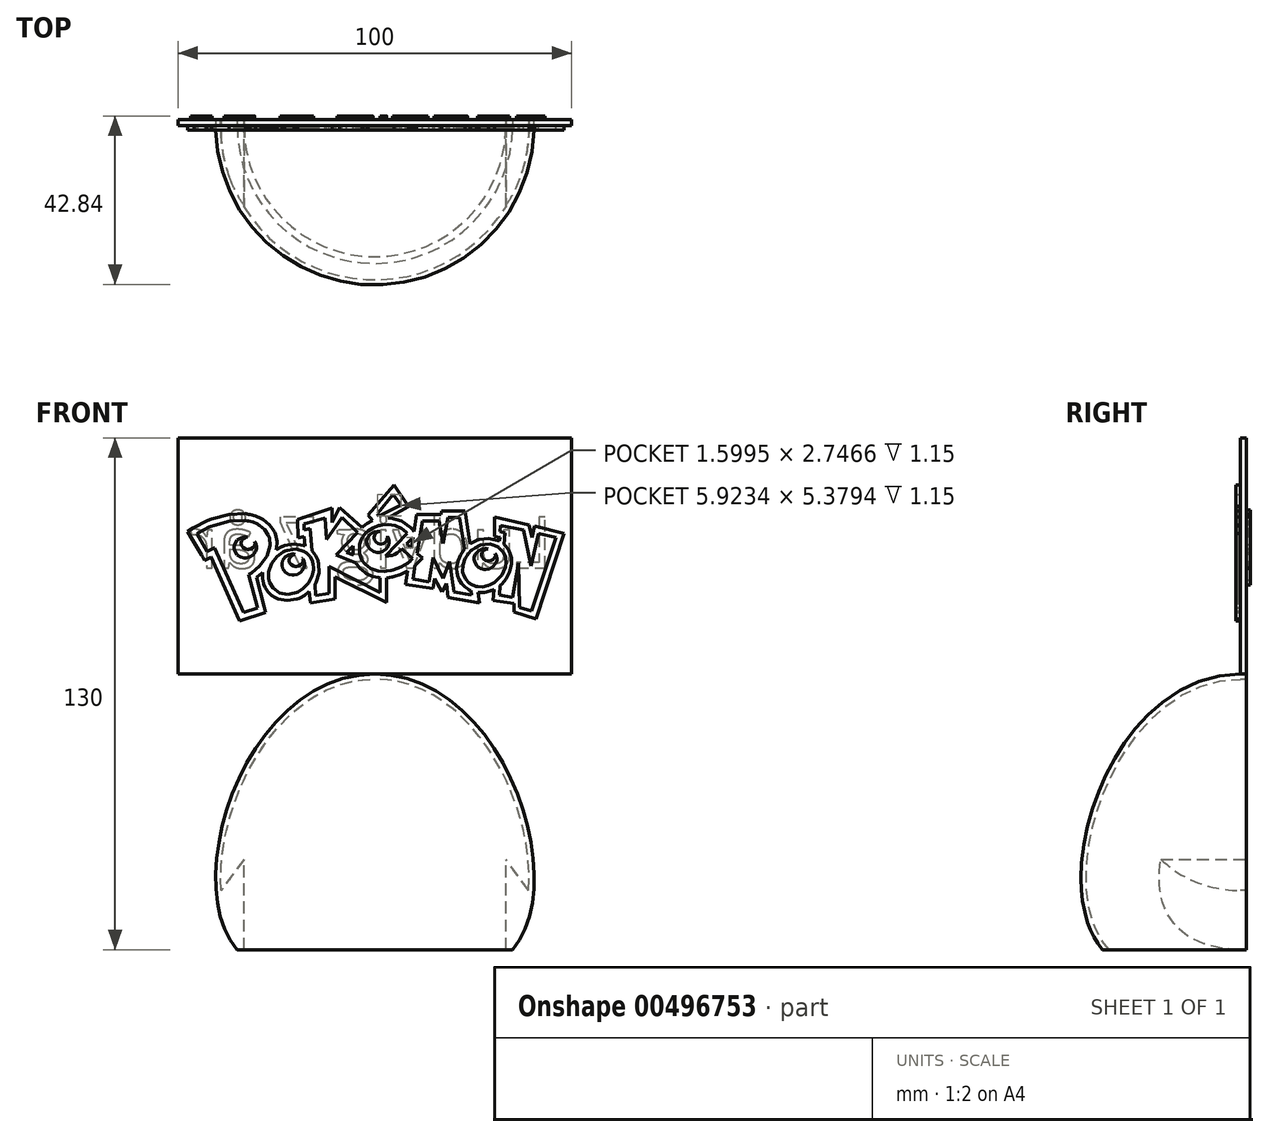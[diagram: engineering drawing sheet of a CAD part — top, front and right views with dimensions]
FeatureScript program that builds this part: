
annotation { "Feature Type Name" : "Feature", "Feature Type Description" : "" }
export const myFeature = defineFeature(function(context is Context, id is Id, definition is map)
    precondition{}
    {
        {
            var Q0;
            Q0=qCreatedBy(makeId("Front.planeOp"),FACE);
            var sketch = newSketch(context, id + "F0", { "sketchPlane" : qUnion([Q0])});
            skLineSegment(sketch, "E0.bottom", {"start": v(-50, 0) * mm, "end": v(50, 0) * mm});
            skLineSegment(sketch, "E0.top", {"start": v(-50, 130) * mm, "end": v(50, 130) * mm});
            skLineSegment(sketch, "E0.left", {"start": v(-50, 0) * mm, "end": v(-50, 130) * mm});
            skLineSegment(sketch, "E0.right", {"start": v(50, 0) * mm, "end": v(50, 130) * mm});
            skLineSegment(sketch, "E1.top", {"start": v(-50, 70) * mm, "end": v(50, 70) * mm});
            skLineSegment(sketch, "E1.left", {"start": v(-50, 0) * mm, "end": v(-50, 70) * mm});
            skLineSegment(sketch, "E1.right", {"start": v(50, 0) * mm, "end": v(50, 70) * mm});
            skPoint(sketch, "E2", {"position": v(35, 0) * mm});
            skFitSpline(sketch, "E3", {"points": [v(35, 0) * mm, v(0, 70) * mm], "startDerivative": vector(45, 52.54) * mm, "endDerivative": vector(-98.13, 0) * mm});
            skLineSegment(sketch, "E4", {"start": v(0, 70) * mm, "end": v(0, 0) * mm});
            skFitSpline(sketch, "E5.MirrorCS", {"points": [v(-35, 0) * mm, v(0, 70) * mm], "startDerivative": vector(-45, 52.54) * mm, "endDerivative": vector(98.13, 0) * mm});
            skSolve(sketch);
        }
        {
            var Q0;
            Q0=makeQuery(id+"F0.imprint","IMPRINT",FACE,{"disambiguationData":[TD([[makeQuery(id+"F0.imprint","IMPRINT",EDGE,{"derivedFrom":sQuery(id+"F0.wireOp",EDGE,"E0.top")}),-1.0]])]});
            var Q1;
            {var subQ0=sQuery(id+"F0.wireOp",EDGE,"E1.left");Q1=makeQuery(id+"F0.imprint","IMPRINT",FACE,{"disambiguationData":[TD([[makeQuery(id+"F0.imprint","IMPRINT",EDGE,{"derivedFrom":subQ0}),-1.0]])]});}
            var Q2;
            {var subQ0=sQuery(id+"F0.wireOp",EDGE,"E1.right");Q2=makeQuery(id+"F0.imprint","IMPRINT",FACE,{"disambiguationData":[TD([[makeQuery(id+"F0.imprint","IMPRINT",EDGE,{"derivedFrom":subQ0}),1.0]])]});}
            extrude(context, id + "F1", {"entities" : qUnion([Q0, Q1, Q2]), "oppositeDirection" : true, "depth" : 1.5 * mm});
        }
        {
            var Q0;
            Q0=makeQuery(id+"F1.opExtrude","CAP_FACE",FACE,{"disambiguationData":[OSD([sQuery(id+"F0.wireOp",EDGE,"E0.top"),sQuery(id+"F0.wireOp",EDGE,"E0.left"),sQuery(id+"F0.wireOp",EDGE,"E0.right"),sQuery(id+"F0.wireOp",EDGE,"E0.bottom"),sQuery(id+"F0.wireOp",EDGE,"E1.left"),sQuery(id+"F0.wireOp",EDGE,"E1.right")])],"isStart":true});
            var sketch = newSketch(context, id + "F2", { "sketchPlane" : qUnion([Q0])});
            skLineSegment(sketch, "E6", {"start": v(0.3, 95.2) * mm, "end": v(0.27, 95.07) * mm});
            skLineSegment(sketch, "E7", {"start": v(0.27, 95.07) * mm, "end": v(0.24, 95.2) * mm});
            skLineSegment(sketch, "E8", {"start": v(0.24, 95.2) * mm, "end": v(-0.14, 95.3) * mm});
            skLineSegment(sketch, "E9", {"start": v(-0.14, 95.3) * mm, "end": v(-0.14, 95.08) * mm});
            skLineSegment(sketch, "E10", {"start": v(-0.14, 95.08) * mm, "end": v(-0.08, 95.07) * mm});
            skLineSegment(sketch, "E11", {"start": v(-0.08, 95.07) * mm, "end": v(-0.08, 95.03) * mm});
            skLineSegment(sketch, "E12", {"start": v(-0.08, 95.03) * mm, "end": v(-0.08, 95.03) * mm});
            skLineSegment(sketch, "E13", {"start": v(-0.08, 95.03) * mm, "end": v(-0.09, 95.03) * mm});
            skLineSegment(sketch, "E14", {"start": v(-0.09, 95.03) * mm, "end": v(-0.09, 95.03) * mm});
            skLineSegment(sketch, "E15", {"start": v(-0.09, 95.03) * mm, "end": v(-0.1, 95.04) * mm});
            skLineSegment(sketch, "E16", {"start": v(-0.1, 95.04) * mm, "end": v(-0.2, 95.06) * mm});
            skLineSegment(sketch, "E17", {"start": v(-0.2, 95.06) * mm, "end": v(-0.3, 95.05) * mm});
            skLineSegment(sketch, "E18", {"start": v(-0.3, 95.05) * mm, "end": v(-0.33, 95.04) * mm});
            skLineSegment(sketch, "E19", {"start": v(-0.33, 95.04) * mm, "end": v(-0.34, 95.04) * mm});
            skLineSegment(sketch, "E20", {"start": v(-0.34, 95.04) * mm, "end": v(-0.4, 95) * mm});
            skLineSegment(sketch, "E21", {"start": v(-0.4, 95) * mm, "end": v(-0.4, 95) * mm});
            skLineSegment(sketch, "E22", {"start": v(-0.4, 95) * mm, "end": v(-0.47, 95.36) * mm});
            skLineSegment(sketch, "E23", {"start": v(-0.47, 95.36) * mm, "end": v(-0.72, 95.36) * mm});
            skLineSegment(sketch, "E24", {"start": v(-0.72, 95.36) * mm, "end": v(-0.73, 95.32) * mm});
            skLineSegment(sketch, "E25", {"start": v(-0.73, 95.32) * mm, "end": v(-1, 95.32) * mm});
            skLineSegment(sketch, "E26", {"start": v(-1, 95.32) * mm, "end": v(-1.03, 95.13) * mm});
            skLineSegment(sketch, "E27", {"start": v(-1.03, 95.13) * mm, "end": v(-1.05, 95.16) * mm});
            skLineSegment(sketch, "E28", {"start": v(-1.05, 95.16) * mm, "end": v(-1.07, 95.18) * mm});
            skLineSegment(sketch, "E29", {"start": v(-1.07, 95.18) * mm, "end": v(-1.17, 95.25) * mm});
            skLineSegment(sketch, "E30", {"start": v(-1.17, 95.25) * mm, "end": v(-1.3, 95.29) * mm});
            skLineSegment(sketch, "E31", {"start": v(-1.3, 95.29) * mm, "end": v(-1.32, 95.29) * mm});
            skLineSegment(sketch, "E32", {"start": v(-1.32, 95.29) * mm, "end": v(-1.09, 95.41) * mm});
            skLineSegment(sketch, "E33", {"start": v(-1.09, 95.41) * mm, "end": v(-1.25, 95.65) * mm});
            skLineSegment(sketch, "E34", {"start": v(-1.25, 95.65) * mm, "end": v(-1.53, 95.32) * mm});
            skLineSegment(sketch, "E35", {"start": v(-1.53, 95.32) * mm, "end": v(-1.49, 95.26) * mm});
            skLineSegment(sketch, "E36", {"start": v(-1.49, 95.26) * mm, "end": v(-1.5, 95.25) * mm});
            skLineSegment(sketch, "E37", {"start": v(-1.5, 95.25) * mm, "end": v(-1.55, 95.22) * mm});
            skLineSegment(sketch, "E38", {"start": v(-1.55, 95.22) * mm, "end": v(-1.6, 95.19) * mm});
            skLineSegment(sketch, "E39", {"start": v(-1.6, 95.19) * mm, "end": v(-1.6, 95.18) * mm});
            skLineSegment(sketch, "E40", {"start": v(-1.6, 95.18) * mm, "end": v(-1.85, 95.4) * mm});
            skLineSegment(sketch, "E41", {"start": v(-1.85, 95.4) * mm, "end": v(-1.94, 95.23) * mm});
            skLineSegment(sketch, "E42", {"start": v(-1.94, 95.23) * mm, "end": v(-1.93, 95.4) * mm});
            skLineSegment(sketch, "E43", {"start": v(-1.93, 95.4) * mm, "end": v(-2.32, 95.27) * mm});
            skLineSegment(sketch, "E44", {"start": v(-2.32, 95.27) * mm, "end": v(-2.3, 95.06) * mm});
            skLineSegment(sketch, "E45", {"start": v(-2.3, 95.06) * mm, "end": v(-2.24, 95.08) * mm});
            skLineSegment(sketch, "E46", {"start": v(-2.24, 95.08) * mm, "end": v(-2.23, 94.98) * mm});
            skLineSegment(sketch, "E47", {"start": v(-2.23, 94.98) * mm, "end": v(-2.25, 94.98) * mm});
            skLineSegment(sketch, "E48", {"start": v(-2.25, 94.98) * mm, "end": v(-2.35, 95) * mm});
            skLineSegment(sketch, "E49", {"start": v(-2.35, 95) * mm, "end": v(-2.46, 94.98) * mm});
            skLineSegment(sketch, "E50", {"start": v(-2.46, 94.98) * mm, "end": v(-2.48, 94.97) * mm});
            skLineSegment(sketch, "E51", {"start": v(-2.48, 94.97) * mm, "end": v(-2.49, 94.97) * mm});
            skLineSegment(sketch, "E52", {"start": v(-2.49, 94.97) * mm, "end": v(-2.55, 94.94) * mm});
            skLineSegment(sketch, "E53", {"start": v(-2.55, 94.94) * mm, "end": v(-2.55, 94.93) * mm});
            skLineSegment(sketch, "E54", {"start": v(-2.55, 94.93) * mm, "end": v(-2.55, 94.95) * mm});
            skLineSegment(sketch, "E55", {"start": v(-2.55, 94.95) * mm, "end": v(-2.54, 95.03) * mm});
            skLineSegment(sketch, "E56", {"start": v(-2.54, 95.03) * mm, "end": v(-2.56, 95.1) * mm});
            skLineSegment(sketch, "E57", {"start": v(-2.56, 95.1) * mm, "end": v(-2.56, 95.12) * mm});
            skLineSegment(sketch, "E58", {"start": v(-2.56, 95.12) * mm, "end": v(-2.57, 95.13) * mm});
            skLineSegment(sketch, "E59", {"start": v(-2.57, 95.13) * mm, "end": v(-2.59, 95.16) * mm});
            skLineSegment(sketch, "E60", {"start": v(-2.59, 95.16) * mm, "end": v(-2.62, 95.2) * mm});
            skLineSegment(sketch, "E61", {"start": v(-2.62, 95.2) * mm, "end": v(-2.66, 95.24) * mm});
            skLineSegment(sketch, "E62", {"start": v(-2.66, 95.24) * mm, "end": v(-2.7, 95.27) * mm});
            skLineSegment(sketch, "E63", {"start": v(-2.7, 95.27) * mm, "end": v(-2.7, 95.27) * mm});
            skLineSegment(sketch, "E64", {"start": v(-2.7, 95.27) * mm, "end": v(-2.72, 95.28) * mm});
            skLineSegment(sketch, "E65", {"start": v(-2.72, 95.28) * mm, "end": v(-2.78, 95.3) * mm});
            skLineSegment(sketch, "E66", {"start": v(-2.78, 95.3) * mm, "end": v(-2.84, 95.32) * mm});
            skLineSegment(sketch, "E67", {"start": v(-2.84, 95.32) * mm, "end": v(-2.86, 95.33) * mm});
            skLineSegment(sketch, "E68", {"start": v(-2.86, 95.33) * mm, "end": v(-2.89, 95.33) * mm});
            skLineSegment(sketch, "E69", {"start": v(-2.89, 95.33) * mm, "end": v(-3.07, 95.33) * mm});
            skLineSegment(sketch, "E70", {"start": v(-3.07, 95.33) * mm, "end": v(-3.27, 95.27) * mm});
            skLineSegment(sketch, "E71", {"start": v(-3.27, 95.27) * mm, "end": v(-3.3, 95.26) * mm});
            skLineSegment(sketch, "E72", {"start": v(-3.3, 95.26) * mm, "end": v(-3.32, 95.25) * mm});
            skLineSegment(sketch, "E73", {"start": v(-3.32, 95.25) * mm, "end": v(-3.46, 95.18) * mm});
            skLineSegment(sketch, "E74", {"start": v(-3.46, 95.18) * mm, "end": v(-3.47, 95.17) * mm});
            skLineSegment(sketch, "E75", {"start": v(-3.47, 95.17) * mm, "end": v(-3.53, 95.13) * mm});
            skLineSegment(sketch, "E76", {"start": v(-3.53, 95.13) * mm, "end": v(-3.5, 95.07) * mm});
            skLineSegment(sketch, "E77", {"start": v(-3.5, 95.07) * mm, "end": v(-3.38, 94.88) * mm});
            skLineSegment(sketch, "E78", {"start": v(-3.38, 94.88) * mm, "end": v(-3.37, 94.87) * mm});
            skLineSegment(sketch, "E79", {"start": v(-3.37, 94.87) * mm, "end": v(-3.36, 94.85) * mm});
            skLineSegment(sketch, "E80", {"start": v(-3.36, 94.85) * mm, "end": v(-3.35, 94.83) * mm});
            skLineSegment(sketch, "E81", {"start": v(-3.35, 94.83) * mm, "end": v(-3.34, 94.82) * mm});
            skLineSegment(sketch, "E82", {"start": v(-3.34, 94.82) * mm, "end": v(-3.34, 94.82) * mm});
            skLineSegment(sketch, "E83", {"start": v(-3.34, 94.82) * mm, "end": v(-3.28, 94.85) * mm});
            skLineSegment(sketch, "E84", {"start": v(-3.28, 94.85) * mm, "end": v(-3.27, 94.85) * mm});
            skLineSegment(sketch, "E85", {"start": v(-3.27, 94.85) * mm, "end": v(-2.98, 94.21) * mm});
            skLineSegment(sketch, "E86", {"start": v(-2.98, 94.21) * mm, "end": v(-2.96, 94.15) * mm});
            skLineSegment(sketch, "E87", {"start": v(-2.96, 94.15) * mm, "end": v(-2.9, 94.17) * mm});
            skLineSegment(sketch, "E88", {"start": v(-2.9, 94.17) * mm, "end": v(-2.74, 94.22) * mm});
            skLineSegment(sketch, "E89", {"start": v(-2.74, 94.22) * mm, "end": v(-2.67, 94.24) * mm});
            skLineSegment(sketch, "E90", {"start": v(-2.67, 94.24) * mm, "end": v(-2.69, 94.31) * mm});
            skLineSegment(sketch, "E91", {"start": v(-2.69, 94.31) * mm, "end": v(-2.77, 94.63) * mm});
            skLineSegment(sketch, "E92", {"start": v(-2.77, 94.63) * mm, "end": v(-2.76, 94.63) * mm});
            skLineSegment(sketch, "E93", {"start": v(-2.76, 94.63) * mm, "end": v(-2.7, 94.68) * mm});
            skLineSegment(sketch, "E94", {"start": v(-2.7, 94.68) * mm, "end": v(-2.7, 94.68) * mm});
            skLineSegment(sketch, "E95", {"start": v(-2.7, 94.68) * mm, "end": v(-2.7, 94.67) * mm});
            skLineSegment(sketch, "E96", {"start": v(-2.7, 94.67) * mm, "end": v(-2.7, 94.63) * mm});
            skLineSegment(sketch, "E97", {"start": v(-2.7, 94.63) * mm, "end": v(-2.7, 94.58) * mm});
            skLineSegment(sketch, "E98", {"start": v(-2.7, 94.58) * mm, "end": v(-2.7, 94.57) * mm});
            skLineSegment(sketch, "E99", {"start": v(-2.7, 94.57) * mm, "end": v(-2.69, 94.56) * mm});
            skLineSegment(sketch, "E100", {"start": v(-2.69, 94.56) * mm, "end": v(-2.67, 94.52) * mm});
            skLineSegment(sketch, "E101", {"start": v(-2.67, 94.52) * mm, "end": v(-2.64, 94.47) * mm});
            skLineSegment(sketch, "E102", {"start": v(-2.64, 94.47) * mm, "end": v(-2.6, 94.43) * mm});
            skLineSegment(sketch, "E103", {"start": v(-2.6, 94.43) * mm, "end": v(-2.56, 94.4) * mm});
            skLineSegment(sketch, "E104", {"start": v(-2.56, 94.4) * mm, "end": v(-2.55, 94.4) * mm});
            skLineSegment(sketch, "E105", {"start": v(-2.55, 94.4) * mm, "end": v(-2.53, 94.39) * mm});
            skLineSegment(sketch, "E106", {"start": v(-2.53, 94.39) * mm, "end": v(-2.43, 94.37) * mm});
            skLineSegment(sketch, "E107", {"start": v(-2.43, 94.37) * mm, "end": v(-2.32, 94.39) * mm});
            skLineSegment(sketch, "E108", {"start": v(-2.32, 94.39) * mm, "end": v(-2.3, 94.4) * mm});
            skLineSegment(sketch, "E109", {"start": v(-2.3, 94.4) * mm, "end": v(-2.29, 94.4) * mm});
            skLineSegment(sketch, "E110", {"start": v(-2.29, 94.4) * mm, "end": v(-2.24, 94.43) * mm});
            skLineSegment(sketch, "E111", {"start": v(-2.24, 94.43) * mm, "end": v(-2.2, 94.47) * mm});
            skLineSegment(sketch, "E112", {"start": v(-2.2, 94.47) * mm, "end": v(-2.19, 94.47) * mm});
            skLineSegment(sketch, "E113", {"start": v(-2.19, 94.47) * mm, "end": v(-2.17, 94.35) * mm});
            skLineSegment(sketch, "E114", {"start": v(-2.17, 94.35) * mm, "end": v(-1.9, 94.39) * mm});
            skLineSegment(sketch, "E115", {"start": v(-1.9, 94.39) * mm, "end": v(-1.9, 94.63) * mm});
            skLineSegment(sketch, "E116", {"start": v(-1.9, 94.63) * mm, "end": v(-1.33, 94.35) * mm});
            skLineSegment(sketch, "E117", {"start": v(-1.33, 94.35) * mm, "end": v(-1.33, 94.62) * mm});
            skLineSegment(sketch, "E118", {"start": v(-1.33, 94.62) * mm, "end": v(-1.33, 94.62) * mm});
            skLineSegment(sketch, "E119", {"start": v(-1.33, 94.62) * mm, "end": v(-1.27, 94.63) * mm});
            skLineSegment(sketch, "E120", {"start": v(-1.27, 94.63) * mm, "end": v(-1.26, 94.63) * mm});
            skLineSegment(sketch, "E121", {"start": v(-1.26, 94.63) * mm, "end": v(-1.25, 94.64) * mm});
            skLineSegment(sketch, "E122", {"start": v(-1.25, 94.64) * mm, "end": v(-1.18, 94.66) * mm});
            skLineSegment(sketch, "E123", {"start": v(-1.18, 94.66) * mm, "end": v(-1.11, 94.7) * mm});
            skLineSegment(sketch, "E124", {"start": v(-1.11, 94.7) * mm, "end": v(-1.1, 94.7) * mm});
            skLineSegment(sketch, "E125", {"start": v(-1.1, 94.7) * mm, "end": v(-1.12, 94.55) * mm});
            skLineSegment(sketch, "E126", {"start": v(-1.12, 94.55) * mm, "end": v(-0.82, 94.5) * mm});
            skLineSegment(sketch, "E127", {"start": v(-0.82, 94.5) * mm, "end": v(-0.8, 94.62) * mm});
            skLineSegment(sketch, "E128", {"start": v(-0.8, 94.62) * mm, "end": v(-0.72, 94.47) * mm});
            skLineSegment(sketch, "E129", {"start": v(-0.72, 94.47) * mm, "end": v(-0.67, 94.56) * mm});
            skLineSegment(sketch, "E130", {"start": v(-0.67, 94.56) * mm, "end": v(-0.65, 94.4) * mm});
            skLineSegment(sketch, "E131", {"start": v(-0.65, 94.4) * mm, "end": v(-0.3, 94.35) * mm});
            skLineSegment(sketch, "E132", {"start": v(-0.3, 94.35) * mm, "end": v(-0.32, 94.46) * mm});
            skLineSegment(sketch, "E133", {"start": v(-0.32, 94.46) * mm, "end": v(-0.31, 94.46) * mm});
            skLineSegment(sketch, "E134", {"start": v(-0.31, 94.46) * mm, "end": v(-0.25, 94.46) * mm});
            skLineSegment(sketch, "E135", {"start": v(-0.25, 94.46) * mm, "end": v(-0.2, 94.48) * mm});
            skLineSegment(sketch, "E136", {"start": v(-0.2, 94.48) * mm, "end": v(-0.18, 94.48) * mm});
            skLineSegment(sketch, "E137", {"start": v(-0.18, 94.48) * mm, "end": v(-0.18, 94.48) * mm});
            skLineSegment(sketch, "E138", {"start": v(-0.18, 94.48) * mm, "end": v(-0.15, 94.5) * mm});
            skLineSegment(sketch, "E139", {"start": v(-0.15, 94.5) * mm, "end": v(-0.14, 94.5) * mm});
            skLineSegment(sketch, "E140", {"start": v(-0.14, 94.5) * mm, "end": v(-0.16, 94.37) * mm});
            skLineSegment(sketch, "E141", {"start": v(-0.16, 94.37) * mm, "end": v(0.07, 94.34) * mm});
            skLineSegment(sketch, "E142", {"start": v(0.07, 94.34) * mm, "end": v(0.07, 94.24) * mm});
            skLineSegment(sketch, "E143", {"start": v(0.07, 94.24) * mm, "end": v(0.32, 94.17) * mm});
            skLineSegment(sketch, "E144", {"start": v(0.32, 94.17) * mm, "end": v(0.63, 95.12) * mm});
            skLineSegment(sketch, "E145", {"start": v(0.63, 95.12) * mm, "end": v(0.3, 95.2) * mm});
            skLineSegment(sketch, "E146", {"start": v(-1.06, 95.05) * mm, "end": v(-1.04, 95.07) * mm});
            skLineSegment(sketch, "E147", {"start": v(-1.04, 95.07) * mm, "end": v(-1.06, 94.95) * mm});
            skLineSegment(sketch, "E148", {"start": v(-1.06, 94.95) * mm, "end": v(-1.1, 95) * mm});
            skLineSegment(sketch, "E149", {"start": v(-1.1, 95) * mm, "end": v(-1.06, 95.05) * mm});
            skLineSegment(sketch, "E150", {"start": v(-1.26, 95.54) * mm, "end": v(-1.18, 95.43) * mm});
            skLineSegment(sketch, "E151", {"start": v(-1.18, 95.43) * mm, "end": v(-1.42, 95.3) * mm});
            skLineSegment(sketch, "E152", {"start": v(-1.42, 95.3) * mm, "end": v(-1.43, 95.33) * mm});
            skLineSegment(sketch, "E153", {"start": v(-1.43, 95.33) * mm, "end": v(-1.26, 95.54) * mm});
            skLineSegment(sketch, "E154", {"start": v(-2.85, 94.66) * mm, "end": v(-2.76, 94.3) * mm});
            skLineSegment(sketch, "E155", {"start": v(-2.76, 94.3) * mm, "end": v(-2.91, 94.24) * mm});
            skLineSegment(sketch, "E156", {"start": v(-2.91, 94.24) * mm, "end": v(-3.23, 94.95) * mm});
            skLineSegment(sketch, "E157", {"start": v(-3.23, 94.95) * mm, "end": v(-3.24, 94.95) * mm});
            skLineSegment(sketch, "E158", {"start": v(-3.24, 94.95) * mm, "end": v(-3.27, 94.94) * mm});
            skLineSegment(sketch, "E159", {"start": v(-3.27, 94.94) * mm, "end": v(-3.3, 94.92) * mm});
            skLineSegment(sketch, "E160", {"start": v(-3.3, 94.92) * mm, "end": v(-3.31, 94.92) * mm});
            skLineSegment(sketch, "E161", {"start": v(-3.31, 94.92) * mm, "end": v(-3.43, 95.11) * mm});
            skLineSegment(sketch, "E162", {"start": v(-3.43, 95.11) * mm, "end": v(-3.42, 95.12) * mm});
            skLineSegment(sketch, "E163", {"start": v(-3.42, 95.12) * mm, "end": v(-3.3, 95.18) * mm});
            skLineSegment(sketch, "E164", {"start": v(-3.3, 95.18) * mm, "end": v(-3.28, 95.19) * mm});
            skLineSegment(sketch, "E165", {"start": v(-3.28, 95.19) * mm, "end": v(-3.24, 95.2) * mm});
            skLineSegment(sketch, "E166", {"start": v(-3.24, 95.2) * mm, "end": v(-3.06, 95.25) * mm});
            skLineSegment(sketch, "E167", {"start": v(-3.06, 95.25) * mm, "end": v(-2.9, 95.26) * mm});
            skLineSegment(sketch, "E168", {"start": v(-2.9, 95.26) * mm, "end": v(-2.87, 95.25) * mm});
            skLineSegment(sketch, "E169", {"start": v(-2.87, 95.25) * mm, "end": v(-2.86, 95.25) * mm});
            skLineSegment(sketch, "E170", {"start": v(-2.86, 95.25) * mm, "end": v(-2.8, 95.24) * mm});
            skLineSegment(sketch, "E171", {"start": v(-2.8, 95.24) * mm, "end": v(-2.76, 95.22) * mm});
            skLineSegment(sketch, "E172", {"start": v(-2.76, 95.22) * mm, "end": v(-2.75, 95.2) * mm});
            skLineSegment(sketch, "E173", {"start": v(-2.75, 95.2) * mm, "end": v(-2.73, 95.2) * mm});
            skLineSegment(sketch, "E174", {"start": v(-2.73, 95.2) * mm, "end": v(-2.68, 95.16) * mm});
            skLineSegment(sketch, "E175", {"start": v(-2.68, 95.16) * mm, "end": v(-2.64, 95.1) * mm});
            skLineSegment(sketch, "E176", {"start": v(-2.64, 95.1) * mm, "end": v(-2.63, 95.09) * mm});
            skLineSegment(sketch, "E177", {"start": v(-2.63, 95.09) * mm, "end": v(-2.62, 95.06) * mm});
            skLineSegment(sketch, "E178", {"start": v(-2.62, 95.06) * mm, "end": v(-2.62, 94.98) * mm});
            skLineSegment(sketch, "E179", {"start": v(-2.62, 94.98) * mm, "end": v(-2.65, 94.87) * mm});
            skLineSegment(sketch, "E180", {"start": v(-2.65, 94.87) * mm, "end": v(-2.73, 94.76) * mm});
            skLineSegment(sketch, "E181", {"start": v(-2.73, 94.76) * mm, "end": v(-2.82, 94.68) * mm});
            skLineSegment(sketch, "E182", {"start": v(-2.82, 94.68) * mm, "end": v(-2.85, 94.66) * mm});
            skLineSegment(sketch, "E183", {"start": v(-2.14, 94.73) * mm, "end": v(-2.14, 94.71) * mm});
            skLineSegment(sketch, "E184", {"start": v(-2.14, 94.71) * mm, "end": v(-2.16, 94.64) * mm});
            skLineSegment(sketch, "E185", {"start": v(-2.16, 94.64) * mm, "end": v(-2.19, 94.58) * mm});
            skLineSegment(sketch, "E186", {"start": v(-2.19, 94.58) * mm, "end": v(-2.2, 94.57) * mm});
            skLineSegment(sketch, "E187", {"start": v(-2.2, 94.57) * mm, "end": v(-2.2, 94.56) * mm});
            skLineSegment(sketch, "E188", {"start": v(-2.2, 94.56) * mm, "end": v(-2.25, 94.5) * mm});
            skLineSegment(sketch, "E189", {"start": v(-2.25, 94.5) * mm, "end": v(-2.31, 94.47) * mm});
            skLineSegment(sketch, "E190", {"start": v(-2.31, 94.47) * mm, "end": v(-2.32, 94.46) * mm});
            skLineSegment(sketch, "E191", {"start": v(-2.32, 94.46) * mm, "end": v(-2.35, 94.45) * mm});
            skLineSegment(sketch, "E192", {"start": v(-2.35, 94.45) * mm, "end": v(-2.42, 94.44) * mm});
            skLineSegment(sketch, "E193", {"start": v(-2.42, 94.44) * mm, "end": v(-2.51, 94.46) * mm});
            skLineSegment(sketch, "E194", {"start": v(-2.51, 94.46) * mm, "end": v(-2.59, 94.51) * mm});
            skLineSegment(sketch, "E195", {"start": v(-2.59, 94.51) * mm, "end": v(-2.62, 94.57) * mm});
            skLineSegment(sketch, "E196", {"start": v(-2.62, 94.57) * mm, "end": v(-2.63, 94.6) * mm});
            skLineSegment(sketch, "E197", {"start": v(-2.63, 94.6) * mm, "end": v(-2.64, 94.61) * mm});
            skLineSegment(sketch, "E198", {"start": v(-2.64, 94.61) * mm, "end": v(-2.64, 94.69) * mm});
            skLineSegment(sketch, "E199", {"start": v(-2.64, 94.69) * mm, "end": v(-2.6, 94.78) * mm});
            skLineSegment(sketch, "E200", {"start": v(-2.6, 94.78) * mm, "end": v(-2.54, 94.86) * mm});
            skLineSegment(sketch, "E201", {"start": v(-2.54, 94.86) * mm, "end": v(-2.48, 94.9) * mm});
            skLineSegment(sketch, "E202", {"start": v(-2.48, 94.9) * mm, "end": v(-2.45, 94.92) * mm});
            skLineSegment(sketch, "E203", {"start": v(-2.45, 94.92) * mm, "end": v(-2.43, 94.93) * mm});
            skLineSegment(sketch, "E204", {"start": v(-2.43, 94.93) * mm, "end": v(-2.33, 94.94) * mm});
            skLineSegment(sketch, "E205", {"start": v(-2.33, 94.94) * mm, "end": v(-2.24, 94.92) * mm});
            skLineSegment(sketch, "E206", {"start": v(-2.24, 94.92) * mm, "end": v(-2.23, 94.9) * mm});
            skLineSegment(sketch, "E207", {"start": v(-2.23, 94.9) * mm, "end": v(-2.22, 94.9) * mm});
            skLineSegment(sketch, "E208", {"start": v(-2.22, 94.9) * mm, "end": v(-2.18, 94.86) * mm});
            skLineSegment(sketch, "E209", {"start": v(-2.18, 94.86) * mm, "end": v(-2.15, 94.8) * mm});
            skLineSegment(sketch, "E210", {"start": v(-2.15, 94.8) * mm, "end": v(-2.15, 94.8) * mm});
            skLineSegment(sketch, "E211", {"start": v(-2.15, 94.8) * mm, "end": v(-2.14, 94.78) * mm});
            skLineSegment(sketch, "E212", {"start": v(-2.14, 94.78) * mm, "end": v(-2.14, 94.78) * mm});
            skLineSegment(sketch, "E213", {"start": v(-2.14, 94.78) * mm, "end": v(-2.14, 94.73) * mm});
            skLineSegment(sketch, "E214", {"start": v(-2.14, 94.73) * mm, "end": v(-2.14, 94.73) * mm});
            skLineSegment(sketch, "E215", {"start": v(-1.4, 94.46) * mm, "end": v(-1.97, 94.75) * mm});
            skLineSegment(sketch, "E216", {"start": v(-1.97, 94.75) * mm, "end": v(-1.97, 94.45) * mm});
            skLineSegment(sketch, "E217", {"start": v(-1.97, 94.45) * mm, "end": v(-2.11, 94.43) * mm});
            skLineSegment(sketch, "E218", {"start": v(-2.11, 94.43) * mm, "end": v(-2.12, 94.55) * mm});
            skLineSegment(sketch, "E219", {"start": v(-2.12, 94.55) * mm, "end": v(-2.11, 94.57) * mm});
            skLineSegment(sketch, "E220", {"start": v(-2.11, 94.57) * mm, "end": v(-2.08, 94.68) * mm});
            skLineSegment(sketch, "E221", {"start": v(-2.08, 94.68) * mm, "end": v(-2.08, 94.78) * mm});
            skLineSegment(sketch, "E222", {"start": v(-2.08, 94.78) * mm, "end": v(-2.09, 94.8) * mm});
            skLineSegment(sketch, "E223", {"start": v(-2.09, 94.8) * mm, "end": v(-2.09, 94.82) * mm});
            skLineSegment(sketch, "E224", {"start": v(-2.09, 94.82) * mm, "end": v(-2.11, 94.87) * mm});
            skLineSegment(sketch, "E225", {"start": v(-2.11, 94.87) * mm, "end": v(-2.15, 94.91) * mm});
            skLineSegment(sketch, "E226", {"start": v(-2.15, 94.91) * mm, "end": v(-2.16, 94.92) * mm});
            skLineSegment(sketch, "E227", {"start": v(-2.16, 94.92) * mm, "end": v(-2.18, 95.17) * mm});
            skLineSegment(sketch, "E228", {"start": v(-2.18, 95.17) * mm, "end": v(-2.24, 95.15) * mm});
            skLineSegment(sketch, "E229", {"start": v(-2.24, 95.15) * mm, "end": v(-2.25, 95.22) * mm});
            skLineSegment(sketch, "E230", {"start": v(-2.25, 95.22) * mm, "end": v(-2.01, 95.29) * mm});
            skLineSegment(sketch, "E231", {"start": v(-2.01, 95.29) * mm, "end": v(-2, 95.05) * mm});
            skLineSegment(sketch, "E232", {"start": v(-2, 95.05) * mm, "end": v(-1.82, 95.29) * mm});
            skLineSegment(sketch, "E233", {"start": v(-1.82, 95.29) * mm, "end": v(-1.65, 95.13) * mm});
            skLineSegment(sketch, "E234", {"start": v(-1.65, 95.13) * mm, "end": v(-1.9, 94.88) * mm});
            skLineSegment(sketch, "E235", {"start": v(-1.9, 94.88) * mm, "end": v(-1.67, 94.8) * mm});
            skLineSegment(sketch, "E236", {"start": v(-1.67, 94.8) * mm, "end": v(-1.66, 94.78) * mm});
            skLineSegment(sketch, "E237", {"start": v(-1.66, 94.78) * mm, "end": v(-1.62, 94.73) * mm});
            skLineSegment(sketch, "E238", {"start": v(-1.62, 94.73) * mm, "end": v(-1.57, 94.68) * mm});
            skLineSegment(sketch, "E239", {"start": v(-1.57, 94.68) * mm, "end": v(-1.56, 94.67) * mm});
            skLineSegment(sketch, "E240", {"start": v(-1.56, 94.67) * mm, "end": v(-1.55, 94.67) * mm});
            skLineSegment(sketch, "E241", {"start": v(-1.55, 94.67) * mm, "end": v(-1.49, 94.64) * mm});
            skLineSegment(sketch, "E242", {"start": v(-1.49, 94.64) * mm, "end": v(-1.42, 94.63) * mm});
            skLineSegment(sketch, "E243", {"start": v(-1.42, 94.63) * mm, "end": v(-1.4, 94.62) * mm});
            skLineSegment(sketch, "E244", {"start": v(-1.4, 94.62) * mm, "end": v(-1.4, 94.46) * mm});
            skLineSegment(sketch, "E245", {"start": v(-1.7, 94.87) * mm, "end": v(-1.78, 94.9) * mm});
            skLineSegment(sketch, "E246", {"start": v(-1.78, 94.9) * mm, "end": v(-1.7, 94.98) * mm});
            skLineSegment(sketch, "E247", {"start": v(-1.7, 94.98) * mm, "end": v(-1.7, 94.97) * mm});
            skLineSegment(sketch, "E248", {"start": v(-1.7, 94.97) * mm, "end": v(-1.7, 94.88) * mm});
            skLineSegment(sketch, "E249", {"start": v(-1.7, 94.88) * mm, "end": v(-1.7, 94.87) * mm});
            skLineSegment(sketch, "E250", {"start": v(-1.08, 94.8) * mm, "end": v(-1.1, 94.79) * mm});
            skLineSegment(sketch, "E251", {"start": v(-1.1, 94.79) * mm, "end": v(-1.17, 94.74) * mm});
            skLineSegment(sketch, "E252", {"start": v(-1.17, 94.74) * mm, "end": v(-1.26, 94.71) * mm});
            skLineSegment(sketch, "E253", {"start": v(-1.26, 94.71) * mm, "end": v(-1.28, 94.7) * mm});
            skLineSegment(sketch, "E254", {"start": v(-1.28, 94.7) * mm, "end": v(-1.29, 94.7) * mm});
            skLineSegment(sketch, "E255", {"start": v(-1.29, 94.7) * mm, "end": v(-1.33, 94.7) * mm});
            skLineSegment(sketch, "E256", {"start": v(-1.33, 94.7) * mm, "end": v(-1.33, 94.7) * mm});
            skLineSegment(sketch, "E257", {"start": v(-1.33, 94.7) * mm, "end": v(-1.36, 94.7) * mm});
            skLineSegment(sketch, "E258", {"start": v(-1.36, 94.7) * mm, "end": v(-1.43, 94.7) * mm});
            skLineSegment(sketch, "E259", {"start": v(-1.43, 94.7) * mm, "end": v(-1.5, 94.73) * mm});
            skLineSegment(sketch, "E260", {"start": v(-1.5, 94.73) * mm, "end": v(-1.57, 94.78) * mm});
            skLineSegment(sketch, "E261", {"start": v(-1.57, 94.78) * mm, "end": v(-1.6, 94.82) * mm});
            skLineSegment(sketch, "E262", {"start": v(-1.6, 94.82) * mm, "end": v(-1.61, 94.84) * mm});
            skLineSegment(sketch, "E263", {"start": v(-1.61, 94.84) * mm, "end": v(-1.61, 94.84) * mm});
            skLineSegment(sketch, "E264", {"start": v(-1.61, 94.84) * mm, "end": v(-1.62, 94.87) * mm});
            skLineSegment(sketch, "E265", {"start": v(-1.62, 94.87) * mm, "end": v(-1.63, 94.88) * mm});
            skLineSegment(sketch, "E266", {"start": v(-1.63, 94.88) * mm, "end": v(-1.63, 94.9) * mm});
            skLineSegment(sketch, "E267", {"start": v(-1.63, 94.9) * mm, "end": v(-1.63, 94.94) * mm});
            skLineSegment(sketch, "E268", {"start": v(-1.63, 94.94) * mm, "end": v(-1.63, 95) * mm});
            skLineSegment(sketch, "E269", {"start": v(-1.63, 95) * mm, "end": v(-1.61, 95.04) * mm});
            skLineSegment(sketch, "E270", {"start": v(-1.61, 95.04) * mm, "end": v(-1.6, 95.08) * mm});
            skLineSegment(sketch, "E271", {"start": v(-1.6, 95.08) * mm, "end": v(-1.59, 95.09) * mm});
            skLineSegment(sketch, "E272", {"start": v(-1.59, 95.09) * mm, "end": v(-1.58, 95.1) * mm});
            skLineSegment(sketch, "E273", {"start": v(-1.58, 95.1) * mm, "end": v(-1.55, 95.13) * mm});
            skLineSegment(sketch, "E274", {"start": v(-1.55, 95.13) * mm, "end": v(-1.55, 95.13) * mm});
            skLineSegment(sketch, "E275", {"start": v(-1.55, 95.13) * mm, "end": v(-1.54, 95.14) * mm});
            skLineSegment(sketch, "E276", {"start": v(-1.54, 95.14) * mm, "end": v(-1.48, 95.18) * mm});
            skLineSegment(sketch, "E277", {"start": v(-1.48, 95.18) * mm, "end": v(-1.42, 95.2) * mm});
            skLineSegment(sketch, "E278", {"start": v(-1.42, 95.2) * mm, "end": v(-1.4, 95.2) * mm});
            skLineSegment(sketch, "E279", {"start": v(-1.4, 95.2) * mm, "end": v(-1.38, 95.2) * mm});
            skLineSegment(sketch, "E280", {"start": v(-1.38, 95.2) * mm, "end": v(-1.32, 95.21) * mm});
            skLineSegment(sketch, "E281", {"start": v(-1.32, 95.21) * mm, "end": v(-1.24, 95.2) * mm});
            skLineSegment(sketch, "E282", {"start": v(-1.24, 95.2) * mm, "end": v(-1.17, 95.17) * mm});
            skLineSegment(sketch, "E283", {"start": v(-1.17, 95.17) * mm, "end": v(-1.12, 95.13) * mm});
            skLineSegment(sketch, "E284", {"start": v(-1.12, 95.13) * mm, "end": v(-1.1, 95.11) * mm});
            skLineSegment(sketch, "E285", {"start": v(-1.1, 95.11) * mm, "end": v(-1.34, 94.86) * mm});
            skLineSegment(sketch, "E286", {"start": v(-1.34, 94.86) * mm, "end": v(-1.34, 94.86) * mm});
            skLineSegment(sketch, "E287", {"start": v(-1.34, 94.86) * mm, "end": v(-1.31, 94.86) * mm});
            skLineSegment(sketch, "E288", {"start": v(-1.31, 94.86) * mm, "end": v(-1.29, 94.87) * mm});
            skLineSegment(sketch, "E289", {"start": v(-1.29, 94.87) * mm, "end": v(-1.28, 94.87) * mm});
            skLineSegment(sketch, "E290", {"start": v(-1.28, 94.87) * mm, "end": v(-1.27, 94.87) * mm});
            skLineSegment(sketch, "E291", {"start": v(-1.27, 94.87) * mm, "end": v(-1.25, 94.88) * mm});
            skLineSegment(sketch, "E292", {"start": v(-1.25, 94.88) * mm, "end": v(-1.21, 94.9) * mm});
            skLineSegment(sketch, "E293", {"start": v(-1.21, 94.9) * mm, "end": v(-1.19, 94.92) * mm});
            skLineSegment(sketch, "E294", {"start": v(-1.19, 94.92) * mm, "end": v(-1.17, 94.94) * mm});
            skLineSegment(sketch, "E295", {"start": v(-1.17, 94.94) * mm, "end": v(-1.17, 94.95) * mm});
            skLineSegment(sketch, "E296", {"start": v(-1.17, 94.95) * mm, "end": v(-1.07, 94.86) * mm});
            skLineSegment(sketch, "E297", {"start": v(-1.07, 94.86) * mm, "end": v(-1.05, 94.84) * mm});
            skLineSegment(sketch, "E298", {"start": v(-1.05, 94.84) * mm, "end": v(-1.05, 94.83) * mm});
            skLineSegment(sketch, "E299", {"start": v(-1.05, 94.83) * mm, "end": v(-1.08, 94.8) * mm});
            skLineSegment(sketch, "E300", {"start": v(-1.08, 94.8) * mm, "end": v(-1.08, 94.8) * mm});
            skLineSegment(sketch, "E301", {"start": v(-0.59, 94.47) * mm, "end": v(-0.64, 94.8) * mm});
            skLineSegment(sketch, "E302", {"start": v(-0.64, 94.8) * mm, "end": v(-0.7, 94.62) * mm});
            skLineSegment(sketch, "E303", {"start": v(-0.7, 94.62) * mm, "end": v(-0.82, 94.85) * mm});
            skLineSegment(sketch, "E304", {"start": v(-0.82, 94.85) * mm, "end": v(-0.82, 94.85) * mm});
            skLineSegment(sketch, "E305", {"start": v(-0.82, 94.85) * mm, "end": v(-0.86, 94.58) * mm});
            skLineSegment(sketch, "E306", {"start": v(-0.86, 94.58) * mm, "end": v(-1.04, 94.61) * mm});
            skLineSegment(sketch, "E307", {"start": v(-1.04, 94.61) * mm, "end": v(-1.02, 94.76) * mm});
            skLineSegment(sketch, "E308", {"start": v(-1.02, 94.76) * mm, "end": v(-1.01, 94.76) * mm});
            skLineSegment(sketch, "E309", {"start": v(-1.01, 94.76) * mm, "end": v(-1, 94.78) * mm});
            skLineSegment(sketch, "E310", {"start": v(-1, 94.78) * mm, "end": v(-1, 94.78) * mm});
            skLineSegment(sketch, "E311", {"start": v(-1, 94.78) * mm, "end": v(-0.94, 94.84) * mm});
            skLineSegment(sketch, "E312", {"start": v(-0.94, 94.84) * mm, "end": v(-1, 94.9) * mm});
            skLineSegment(sketch, "E313", {"start": v(-1, 94.9) * mm, "end": v(-0.93, 95.25) * mm});
            skLineSegment(sketch, "E314", {"start": v(-0.93, 95.25) * mm, "end": v(-0.75, 95.25) * mm});
            skLineSegment(sketch, "E315", {"start": v(-0.75, 95.25) * mm, "end": v(-0.7, 95) * mm});
            skLineSegment(sketch, "E316", {"start": v(-0.7, 95) * mm, "end": v(-0.66, 95.3) * mm});
            skLineSegment(sketch, "E317", {"start": v(-0.66, 95.3) * mm, "end": v(-0.52, 95.3) * mm});
            skLineSegment(sketch, "E318", {"start": v(-0.52, 95.3) * mm, "end": v(-0.47, 94.94) * mm});
            skLineSegment(sketch, "E319", {"start": v(-0.47, 94.94) * mm, "end": v(-0.48, 94.93) * mm});
            skLineSegment(sketch, "E320", {"start": v(-0.48, 94.93) * mm, "end": v(-0.52, 94.88) * mm});
            skLineSegment(sketch, "E321", {"start": v(-0.52, 94.88) * mm, "end": v(-0.54, 94.8) * mm});
            skLineSegment(sketch, "E322", {"start": v(-0.54, 94.8) * mm, "end": v(-0.56, 94.73) * mm});
            skLineSegment(sketch, "E323", {"start": v(-0.56, 94.73) * mm, "end": v(-0.55, 94.68) * mm});
            skLineSegment(sketch, "E324", {"start": v(-0.55, 94.68) * mm, "end": v(-0.55, 94.66) * mm});
            skLineSegment(sketch, "E325", {"start": v(-0.55, 94.66) * mm, "end": v(-0.55, 94.65) * mm});
            skLineSegment(sketch, "E326", {"start": v(-0.55, 94.65) * mm, "end": v(-0.53, 94.6) * mm});
            skLineSegment(sketch, "E327", {"start": v(-0.53, 94.6) * mm, "end": v(-0.5, 94.56) * mm});
            skLineSegment(sketch, "E328", {"start": v(-0.5, 94.56) * mm, "end": v(-0.47, 94.52) * mm});
            skLineSegment(sketch, "E329", {"start": v(-0.47, 94.52) * mm, "end": v(-0.43, 94.5) * mm});
            skLineSegment(sketch, "E330", {"start": v(-0.43, 94.5) * mm, "end": v(-0.42, 94.5) * mm});
            skLineSegment(sketch, "E331", {"start": v(-0.42, 94.5) * mm, "end": v(-0.42, 94.5) * mm});
            skLineSegment(sketch, "E332", {"start": v(-0.42, 94.5) * mm, "end": v(-0.4, 94.48) * mm});
            skLineSegment(sketch, "E333", {"start": v(-0.4, 94.48) * mm, "end": v(-0.4, 94.48) * mm});
            skLineSegment(sketch, "E334", {"start": v(-0.4, 94.48) * mm, "end": v(-0.4, 94.44) * mm});
            skLineSegment(sketch, "E335", {"start": v(-0.4, 94.44) * mm, "end": v(-0.59, 94.47) * mm});
            skLineSegment(sketch, "E336", {"start": v(-0.14, 94.58) * mm, "end": v(-0.14, 94.57) * mm});
            skLineSegment(sketch, "E337", {"start": v(-0.14, 94.57) * mm, "end": v(-0.2, 94.54) * mm});
            skLineSegment(sketch, "E338", {"start": v(-0.2, 94.54) * mm, "end": v(-0.2, 94.54) * mm});
            skLineSegment(sketch, "E339", {"start": v(-0.2, 94.54) * mm, "end": v(-0.21, 94.54) * mm});
            skLineSegment(sketch, "E340", {"start": v(-0.21, 94.54) * mm, "end": v(-0.27, 94.52) * mm});
            skLineSegment(sketch, "E341", {"start": v(-0.27, 94.52) * mm, "end": v(-0.32, 94.53) * mm});
            skLineSegment(sketch, "E342", {"start": v(-0.32, 94.53) * mm, "end": v(-0.33, 94.53) * mm});
            skLineSegment(sketch, "E343", {"start": v(-0.33, 94.53) * mm, "end": v(-0.34, 94.53) * mm});
            skLineSegment(sketch, "E344", {"start": v(-0.34, 94.53) * mm, "end": v(-0.4, 94.56) * mm});
            skLineSegment(sketch, "E345", {"start": v(-0.4, 94.56) * mm, "end": v(-0.41, 94.56) * mm});
            skLineSegment(sketch, "E346", {"start": v(-0.41, 94.56) * mm, "end": v(-0.42, 94.57) * mm});
            skLineSegment(sketch, "E347", {"start": v(-0.42, 94.57) * mm, "end": v(-0.46, 94.6) * mm});
            skLineSegment(sketch, "E348", {"start": v(-0.46, 94.6) * mm, "end": v(-0.48, 94.66) * mm});
            skLineSegment(sketch, "E349", {"start": v(-0.48, 94.66) * mm, "end": v(-0.49, 94.67) * mm});
            skLineSegment(sketch, "E350", {"start": v(-0.49, 94.67) * mm, "end": v(-0.5, 94.69) * mm});
            skLineSegment(sketch, "E351", {"start": v(-0.5, 94.69) * mm, "end": v(-0.49, 94.76) * mm});
            skLineSegment(sketch, "E352", {"start": v(-0.49, 94.76) * mm, "end": v(-0.46, 94.84) * mm});
            skLineSegment(sketch, "E353", {"start": v(-0.46, 94.84) * mm, "end": v(-0.46, 94.85) * mm});
            skLineSegment(sketch, "E354", {"start": v(-0.46, 94.85) * mm, "end": v(-0.45, 94.86) * mm});
            skLineSegment(sketch, "E355", {"start": v(-0.45, 94.86) * mm, "end": v(-0.4, 94.92) * mm});
            skLineSegment(sketch, "E356", {"start": v(-0.4, 94.92) * mm, "end": v(-0.4, 94.92) * mm});
            skLineSegment(sketch, "E357", {"start": v(-0.4, 94.92) * mm, "end": v(-0.4, 94.93) * mm});
            skLineSegment(sketch, "E358", {"start": v(-0.4, 94.93) * mm, "end": v(-0.35, 94.96) * mm});
            skLineSegment(sketch, "E359", {"start": v(-0.35, 94.96) * mm, "end": v(-0.31, 94.98) * mm});
            skLineSegment(sketch, "E360", {"start": v(-0.31, 94.98) * mm, "end": v(-0.3, 94.98) * mm});
            skLineSegment(sketch, "E361", {"start": v(-0.3, 94.98) * mm, "end": v(-0.3, 94.99) * mm});
            skLineSegment(sketch, "E362", {"start": v(-0.3, 94.99) * mm, "end": v(-0.25, 95) * mm});
            skLineSegment(sketch, "E363", {"start": v(-0.25, 95) * mm, "end": v(-0.2, 95) * mm});
            skLineSegment(sketch, "E364", {"start": v(-0.2, 95) * mm, "end": v(-0.14, 94.98) * mm});
            skLineSegment(sketch, "E365", {"start": v(-0.14, 94.98) * mm, "end": v(-0.1, 94.97) * mm});
            skLineSegment(sketch, "E366", {"start": v(-0.1, 94.97) * mm, "end": v(-0.1, 94.96) * mm});
            skLineSegment(sketch, "E367", {"start": v(-0.1, 94.96) * mm, "end": v(-0.09, 94.96) * mm});
            skLineSegment(sketch, "E368", {"start": v(-0.09, 94.96) * mm, "end": v(-0.05, 94.91) * mm});
            skLineSegment(sketch, "E369", {"start": v(-0.05, 94.91) * mm, "end": v(-0.04, 94.9) * mm});
            skLineSegment(sketch, "E370", {"start": v(-0.04, 94.9) * mm, "end": v(-0.04, 94.9) * mm});
            skLineSegment(sketch, "E371", {"start": v(-0.04, 94.9) * mm, "end": v(-0.02, 94.85) * mm});
            skLineSegment(sketch, "E372", {"start": v(-0.02, 94.85) * mm, "end": v(-0.02, 94.85) * mm});
            skLineSegment(sketch, "E373", {"start": v(-0.02, 94.85) * mm, "end": v(-0.02, 94.84) * mm});
            skLineSegment(sketch, "E374", {"start": v(-0.02, 94.84) * mm, "end": v(-0.01, 94.8) * mm});
            skLineSegment(sketch, "E375", {"start": v(-0.01, 94.8) * mm, "end": v(-0.02, 94.74) * mm});
            skLineSegment(sketch, "E376", {"start": v(-0.02, 94.74) * mm, "end": v(-0.04, 94.7) * mm});
            skLineSegment(sketch, "E377", {"start": v(-0.04, 94.7) * mm, "end": v(-0.06, 94.66) * mm});
            skLineSegment(sketch, "E378", {"start": v(-0.06, 94.66) * mm, "end": v(-0.07, 94.64) * mm});
            skLineSegment(sketch, "E379", {"start": v(-0.07, 94.64) * mm, "end": v(-0.07, 94.64) * mm});
            skLineSegment(sketch, "E380", {"start": v(-0.07, 94.64) * mm, "end": v(-0.13, 94.58) * mm});
            skLineSegment(sketch, "E381", {"start": v(-0.13, 94.58) * mm, "end": v(-0.14, 94.58) * mm});
            skLineSegment(sketch, "E382", {"start": v(0.27, 94.26) * mm, "end": v(0.14, 94.3) * mm});
            skLineSegment(sketch, "E383", {"start": v(0.14, 94.3) * mm, "end": v(0.13, 94.79) * mm});
            skLineSegment(sketch, "E384", {"start": v(0.13, 94.79) * mm, "end": v(0.06, 94.4) * mm});
            skLineSegment(sketch, "E385", {"start": v(0.06, 94.4) * mm, "end": v(-0.09, 94.43) * mm});
            skLineSegment(sketch, "E386", {"start": v(-0.09, 94.43) * mm, "end": v(-0.08, 94.54) * mm});
            skLineSegment(sketch, "E387", {"start": v(-0.08, 94.54) * mm, "end": v(-0.06, 94.56) * mm});
            skLineSegment(sketch, "E388", {"start": v(-0.06, 94.56) * mm, "end": v(-0.01, 94.6) * mm});
            skLineSegment(sketch, "E389", {"start": v(-0.01, 94.6) * mm, "end": v(0.03, 94.69) * mm});
            skLineSegment(sketch, "E390", {"start": v(0.03, 94.69) * mm, "end": v(0.05, 94.78) * mm});
            skLineSegment(sketch, "E391", {"start": v(0.05, 94.78) * mm, "end": v(0.05, 94.84) * mm});
            skLineSegment(sketch, "E392", {"start": v(0.05, 94.84) * mm, "end": v(0.04, 94.86) * mm});
            skLineSegment(sketch, "E393", {"start": v(0.04, 94.86) * mm, "end": v(0.04, 94.88) * mm});
            skLineSegment(sketch, "E394", {"start": v(0.04, 94.88) * mm, "end": v(0.01, 94.93) * mm});
            skLineSegment(sketch, "E395", {"start": v(0.01, 94.93) * mm, "end": v(-0.02, 94.98) * mm});
            skLineSegment(sketch, "E396", {"start": v(-0.02, 94.98) * mm, "end": v(-0.03, 95) * mm});
            skLineSegment(sketch, "E397", {"start": v(-0.03, 95) * mm, "end": v(-0.02, 95.12) * mm});
            skLineSegment(sketch, "E398", {"start": v(-0.02, 95.12) * mm, "end": v(-0.08, 95.14) * mm});
            skLineSegment(sketch, "E399", {"start": v(-0.08, 95.14) * mm, "end": v(-0.07, 95.2) * mm});
            skLineSegment(sketch, "E400", {"start": v(-0.07, 95.2) * mm, "end": v(0.18, 95.15) * mm});
            skLineSegment(sketch, "E401", {"start": v(0.18, 95.15) * mm, "end": v(0.26, 94.75) * mm});
            skLineSegment(sketch, "E402", {"start": v(0.26, 94.75) * mm, "end": v(0.35, 95.11) * mm});
            skLineSegment(sketch, "E403", {"start": v(0.35, 95.11) * mm, "end": v(0.54, 95.07) * mm});
            skLineSegment(sketch, "E404", {"start": v(0.54, 95.07) * mm, "end": v(0.27, 94.26) * mm});
            skLineSegment(sketch, "E405", {"start": v(-0.13, 94.9) * mm, "end": v(-0.13, 94.9) * mm});
            skLineSegment(sketch, "E406", {"start": v(-0.13, 94.9) * mm, "end": v(-0.13, 94.88) * mm});
            skLineSegment(sketch, "E407", {"start": v(-0.13, 94.88) * mm, "end": v(-0.13, 94.87) * mm});
            skLineSegment(sketch, "E408", {"start": v(-0.13, 94.87) * mm, "end": v(-0.13, 94.87) * mm});
            skLineSegment(sketch, "E409", {"start": v(-0.13, 94.87) * mm, "end": v(-0.14, 94.85) * mm});
            skLineSegment(sketch, "E410", {"start": v(-0.14, 94.85) * mm, "end": v(-0.15, 94.83) * mm});
            skLineSegment(sketch, "E411", {"start": v(-0.15, 94.83) * mm, "end": v(-0.18, 94.81) * mm});
            skLineSegment(sketch, "E412", {"start": v(-0.18, 94.81) * mm, "end": v(-0.2, 94.8) * mm});
            skLineSegment(sketch, "E413", {"start": v(-0.2, 94.8) * mm, "end": v(-0.2, 94.8) * mm});
            skLineSegment(sketch, "E414", {"start": v(-0.2, 94.8) * mm, "end": v(-0.22, 94.8) * mm});
            skLineSegment(sketch, "E415", {"start": v(-0.22, 94.8) * mm, "end": v(-0.24, 94.82) * mm});
            skLineSegment(sketch, "E416", {"start": v(-0.24, 94.82) * mm, "end": v(-0.26, 94.83) * mm});
            skLineSegment(sketch, "E417", {"start": v(-0.26, 94.83) * mm, "end": v(-0.28, 94.85) * mm});
            skLineSegment(sketch, "E418", {"start": v(-0.28, 94.85) * mm, "end": v(-0.28, 94.87) * mm});
            skLineSegment(sketch, "E419", {"start": v(-0.28, 94.87) * mm, "end": v(-0.28, 94.88) * mm});
            skLineSegment(sketch, "E420", {"start": v(-0.28, 94.88) * mm, "end": v(-0.28, 94.89) * mm});
            skLineSegment(sketch, "E421", {"start": v(-0.28, 94.89) * mm, "end": v(-0.28, 94.9) * mm});
            skLineSegment(sketch, "E422", {"start": v(-0.28, 94.9) * mm, "end": v(-0.26, 94.92) * mm});
            skLineSegment(sketch, "E423", {"start": v(-0.26, 94.92) * mm, "end": v(-0.24, 94.94) * mm});
            skLineSegment(sketch, "E424", {"start": v(-0.24, 94.94) * mm, "end": v(-0.22, 94.94) * mm});
            skLineSegment(sketch, "E425", {"start": v(-0.22, 94.94) * mm, "end": v(-0.21, 94.94) * mm});
            skLineSegment(sketch, "E426", {"start": v(-0.21, 94.94) * mm, "end": v(-0.21, 94.94) * mm});
            skLineSegment(sketch, "E427", {"start": v(-0.21, 94.94) * mm, "end": v(-0.23, 94.95) * mm});
            skLineSegment(sketch, "E428", {"start": v(-0.23, 94.95) * mm, "end": v(-0.23, 94.95) * mm});
            skLineSegment(sketch, "E429", {"start": v(-0.23, 94.95) * mm, "end": v(-0.25, 94.95) * mm});
            skLineSegment(sketch, "E430", {"start": v(-0.25, 94.95) * mm, "end": v(-0.28, 94.94) * mm});
            skLineSegment(sketch, "E431", {"start": v(-0.28, 94.94) * mm, "end": v(-0.32, 94.92) * mm});
            skLineSegment(sketch, "E432", {"start": v(-0.32, 94.92) * mm, "end": v(-0.35, 94.88) * mm});
            skLineSegment(sketch, "E433", {"start": v(-0.35, 94.88) * mm, "end": v(-0.36, 94.85) * mm});
            skLineSegment(sketch, "E434", {"start": v(-0.36, 94.85) * mm, "end": v(-0.36, 94.84) * mm});
            skLineSegment(sketch, "E435", {"start": v(-0.36, 94.84) * mm, "end": v(-0.36, 94.83) * mm});
            skLineSegment(sketch, "E436", {"start": v(-0.36, 94.83) * mm, "end": v(-0.36, 94.8) * mm});
            skLineSegment(sketch, "E437", {"start": v(-0.36, 94.8) * mm, "end": v(-0.33, 94.75) * mm});
            skLineSegment(sketch, "E438", {"start": v(-0.33, 94.75) * mm, "end": v(-0.3, 94.73) * mm});
            skLineSegment(sketch, "E439", {"start": v(-0.3, 94.73) * mm, "end": v(-0.26, 94.72) * mm});
            skLineSegment(sketch, "E440", {"start": v(-0.26, 94.72) * mm, "end": v(-0.24, 94.72) * mm});
            skLineSegment(sketch, "E441", {"start": v(-0.24, 94.72) * mm, "end": v(-0.23, 94.72) * mm});
            skLineSegment(sketch, "E442", {"start": v(-0.23, 94.72) * mm, "end": v(-0.2, 94.72) * mm});
            skLineSegment(sketch, "E443", {"start": v(-0.2, 94.72) * mm, "end": v(-0.15, 94.75) * mm});
            skLineSegment(sketch, "E444", {"start": v(-0.15, 94.75) * mm, "end": v(-0.13, 94.78) * mm});
            skLineSegment(sketch, "E445", {"start": v(-0.13, 94.78) * mm, "end": v(-0.11, 94.82) * mm});
            skLineSegment(sketch, "E446", {"start": v(-0.11, 94.82) * mm, "end": v(-0.11, 94.83) * mm});
            skLineSegment(sketch, "E447", {"start": v(-0.11, 94.83) * mm, "end": v(-0.11, 94.83) * mm});
            skLineSegment(sketch, "E448", {"start": v(-0.11, 94.83) * mm, "end": v(-0.12, 94.86) * mm});
            skLineSegment(sketch, "E449", {"start": v(-0.12, 94.86) * mm, "end": v(-0.13, 94.89) * mm});
            skLineSegment(sketch, "E450", {"start": v(-0.13, 94.89) * mm, "end": v(-0.13, 94.9) * mm});
            skLineSegment(sketch, "E451", {"start": v(-2.26, 94.82) * mm, "end": v(-2.26, 94.8) * mm});
            skLineSegment(sketch, "E452", {"start": v(-2.26, 94.8) * mm, "end": v(-2.26, 94.8) * mm});
            skLineSegment(sketch, "E453", {"start": v(-2.26, 94.8) * mm, "end": v(-2.28, 94.77) * mm});
            skLineSegment(sketch, "E454", {"start": v(-2.28, 94.77) * mm, "end": v(-2.3, 94.75) * mm});
            skLineSegment(sketch, "E455", {"start": v(-2.3, 94.75) * mm, "end": v(-2.33, 94.75) * mm});
            skLineSegment(sketch, "E456", {"start": v(-2.33, 94.75) * mm, "end": v(-2.33, 94.75) * mm});
            skLineSegment(sketch, "E457", {"start": v(-2.33, 94.75) * mm, "end": v(-2.34, 94.75) * mm});
            skLineSegment(sketch, "E458", {"start": v(-2.34, 94.75) * mm, "end": v(-2.36, 94.75) * mm});
            skLineSegment(sketch, "E459", {"start": v(-2.36, 94.75) * mm, "end": v(-2.39, 94.77) * mm});
            skLineSegment(sketch, "E460", {"start": v(-2.39, 94.77) * mm, "end": v(-2.4, 94.8) * mm});
            skLineSegment(sketch, "E461", {"start": v(-2.4, 94.8) * mm, "end": v(-2.4, 94.8) * mm});
            skLineSegment(sketch, "E462", {"start": v(-2.4, 94.8) * mm, "end": v(-2.4, 94.82) * mm});
            skLineSegment(sketch, "E463", {"start": v(-2.4, 94.82) * mm, "end": v(-2.4, 94.82) * mm});
            skLineSegment(sketch, "E464", {"start": v(-2.4, 94.82) * mm, "end": v(-2.4, 94.84) * mm});
            skLineSegment(sketch, "E465", {"start": v(-2.4, 94.84) * mm, "end": v(-2.39, 94.86) * mm});
            skLineSegment(sketch, "E466", {"start": v(-2.39, 94.86) * mm, "end": v(-2.37, 94.88) * mm});
            skLineSegment(sketch, "E467", {"start": v(-2.37, 94.88) * mm, "end": v(-2.35, 94.88) * mm});
            skLineSegment(sketch, "E468", {"start": v(-2.35, 94.88) * mm, "end": v(-2.34, 94.88) * mm});
            skLineSegment(sketch, "E469", {"start": v(-2.34, 94.88) * mm, "end": v(-2.34, 94.88) * mm});
            skLineSegment(sketch, "E470", {"start": v(-2.34, 94.88) * mm, "end": v(-2.36, 94.89) * mm});
            skLineSegment(sketch, "E471", {"start": v(-2.36, 94.89) * mm, "end": v(-2.36, 94.89) * mm});
            skLineSegment(sketch, "E472", {"start": v(-2.36, 94.89) * mm, "end": v(-2.38, 94.89) * mm});
            skLineSegment(sketch, "E473", {"start": v(-2.38, 94.89) * mm, "end": v(-2.41, 94.88) * mm});
            skLineSegment(sketch, "E474", {"start": v(-2.41, 94.88) * mm, "end": v(-2.45, 94.85) * mm});
            skLineSegment(sketch, "E475", {"start": v(-2.45, 94.85) * mm, "end": v(-2.48, 94.82) * mm});
            skLineSegment(sketch, "E476", {"start": v(-2.48, 94.82) * mm, "end": v(-2.49, 94.78) * mm});
            skLineSegment(sketch, "E477", {"start": v(-2.49, 94.78) * mm, "end": v(-2.49, 94.77) * mm});
            skLineSegment(sketch, "E478", {"start": v(-2.49, 94.77) * mm, "end": v(-2.49, 94.76) * mm});
            skLineSegment(sketch, "E479", {"start": v(-2.49, 94.76) * mm, "end": v(-2.48, 94.73) * mm});
            skLineSegment(sketch, "E480", {"start": v(-2.48, 94.73) * mm, "end": v(-2.45, 94.69) * mm});
            skLineSegment(sketch, "E481", {"start": v(-2.45, 94.69) * mm, "end": v(-2.41, 94.66) * mm});
            skLineSegment(sketch, "E482", {"start": v(-2.41, 94.66) * mm, "end": v(-2.38, 94.65) * mm});
            skLineSegment(sketch, "E483", {"start": v(-2.38, 94.65) * mm, "end": v(-2.36, 94.65) * mm});
            skLineSegment(sketch, "E484", {"start": v(-2.36, 94.65) * mm, "end": v(-2.35, 94.65) * mm});
            skLineSegment(sketch, "E485", {"start": v(-2.35, 94.65) * mm, "end": v(-2.32, 94.66) * mm});
            skLineSegment(sketch, "E486", {"start": v(-2.32, 94.66) * mm, "end": v(-2.28, 94.69) * mm});
            skLineSegment(sketch, "E487", {"start": v(-2.28, 94.69) * mm, "end": v(-2.25, 94.73) * mm});
            skLineSegment(sketch, "E488", {"start": v(-2.25, 94.73) * mm, "end": v(-2.24, 94.76) * mm});
            skLineSegment(sketch, "E489", {"start": v(-2.24, 94.76) * mm, "end": v(-2.24, 94.77) * mm});
            skLineSegment(sketch, "E490", {"start": v(-2.24, 94.77) * mm, "end": v(-2.24, 94.78) * mm});
            skLineSegment(sketch, "E491", {"start": v(-2.24, 94.78) * mm, "end": v(-2.24, 94.8) * mm});
            skLineSegment(sketch, "E492", {"start": v(-2.24, 94.8) * mm, "end": v(-2.26, 94.83) * mm});
            skLineSegment(sketch, "E493", {"start": v(-2.26, 94.83) * mm, "end": v(-2.26, 94.83) * mm});
            skLineSegment(sketch, "E494", {"start": v(-2.26, 94.83) * mm, "end": v(-2.26, 94.82) * mm});
            skLineSegment(sketch, "E495", {"start": v(-2.26, 94.82) * mm, "end": v(-2.26, 94.82) * mm});
            skLineSegment(sketch, "E496", {"start": v(-1.2, 94.91) * mm, "end": v(-1.2, 94.91) * mm});
            skLineSegment(sketch, "E497", {"start": v(-1.2, 94.91) * mm, "end": v(-1.2, 94.9) * mm});
            skLineSegment(sketch, "E498", {"start": v(-1.2, 94.9) * mm, "end": v(-1.2, 94.9) * mm});
            skLineSegment(sketch, "E499", {"start": v(-1.2, 94.9) * mm, "end": v(-1.2, 94.91) * mm});
            skLineSegment(sketch, "E500", {"start": v(-1.78, 94.9) * mm, "end": v(-1.78, 94.9) * mm});
            skLineSegment(sketch, "E501", {"start": v(-1.32, 95.07) * mm, "end": v(-1.32, 95.06) * mm});
            skLineSegment(sketch, "E502", {"start": v(-1.32, 95.06) * mm, "end": v(-1.33, 95.04) * mm});
            skLineSegment(sketch, "E503", {"start": v(-1.33, 95.04) * mm, "end": v(-1.34, 95.02) * mm});
            skLineSegment(sketch, "E504", {"start": v(-1.34, 95.02) * mm, "end": v(-1.37, 95) * mm});
            skLineSegment(sketch, "E505", {"start": v(-1.37, 95) * mm, "end": v(-1.39, 95) * mm});
            skLineSegment(sketch, "E506", {"start": v(-1.39, 95) * mm, "end": v(-1.4, 95) * mm});
            skLineSegment(sketch, "E507", {"start": v(-1.4, 95) * mm, "end": v(-1.4, 95) * mm});
            skLineSegment(sketch, "E508", {"start": v(-1.4, 95) * mm, "end": v(-1.43, 95) * mm});
            skLineSegment(sketch, "E509", {"start": v(-1.43, 95) * mm, "end": v(-1.45, 95.02) * mm});
            skLineSegment(sketch, "E510", {"start": v(-1.45, 95.02) * mm, "end": v(-1.47, 95.04) * mm});
            skLineSegment(sketch, "E511", {"start": v(-1.47, 95.04) * mm, "end": v(-1.47, 95.06) * mm});
            skLineSegment(sketch, "E512", {"start": v(-1.47, 95.06) * mm, "end": v(-1.47, 95.07) * mm});
            skLineSegment(sketch, "E513", {"start": v(-1.47, 95.07) * mm, "end": v(-1.47, 95.07) * mm});
            skLineSegment(sketch, "E514", {"start": v(-1.47, 95.07) * mm, "end": v(-1.47, 95.1) * mm});
            skLineSegment(sketch, "E515", {"start": v(-1.47, 95.1) * mm, "end": v(-1.45, 95.11) * mm});
            skLineSegment(sketch, "E516", {"start": v(-1.45, 95.11) * mm, "end": v(-1.43, 95.13) * mm});
            skLineSegment(sketch, "E517", {"start": v(-1.43, 95.13) * mm, "end": v(-1.41, 95.13) * mm});
            skLineSegment(sketch, "E518", {"start": v(-1.41, 95.13) * mm, "end": v(-1.4, 95.14) * mm});
            skLineSegment(sketch, "E519", {"start": v(-1.4, 95.14) * mm, "end": v(-1.4, 95.14) * mm});
            skLineSegment(sketch, "E520", {"start": v(-1.4, 95.14) * mm, "end": v(-1.42, 95.14) * mm});
            skLineSegment(sketch, "E521", {"start": v(-1.42, 95.14) * mm, "end": v(-1.43, 95.14) * mm});
            skLineSegment(sketch, "E522", {"start": v(-1.43, 95.14) * mm, "end": v(-1.44, 95.14) * mm});
            skLineSegment(sketch, "E523", {"start": v(-1.44, 95.14) * mm, "end": v(-1.48, 95.13) * mm});
            skLineSegment(sketch, "E524", {"start": v(-1.48, 95.13) * mm, "end": v(-1.52, 95.1) * mm});
            skLineSegment(sketch, "E525", {"start": v(-1.52, 95.1) * mm, "end": v(-1.54, 95.07) * mm});
            skLineSegment(sketch, "E526", {"start": v(-1.54, 95.07) * mm, "end": v(-1.55, 95.03) * mm});
            skLineSegment(sketch, "E527", {"start": v(-1.55, 95.03) * mm, "end": v(-1.55, 95.02) * mm});
            skLineSegment(sketch, "E528", {"start": v(-1.55, 95.02) * mm, "end": v(-1.55, 95.01) * mm});
            skLineSegment(sketch, "E529", {"start": v(-1.55, 95.01) * mm, "end": v(-1.54, 94.98) * mm});
            skLineSegment(sketch, "E530", {"start": v(-1.54, 94.98) * mm, "end": v(-1.52, 94.94) * mm});
            skLineSegment(sketch, "E531", {"start": v(-1.52, 94.94) * mm, "end": v(-1.48, 94.91) * mm});
            skLineSegment(sketch, "E532", {"start": v(-1.48, 94.91) * mm, "end": v(-1.44, 94.9) * mm});
            skLineSegment(sketch, "E533", {"start": v(-1.44, 94.9) * mm, "end": v(-1.43, 94.9) * mm});
            skLineSegment(sketch, "E534", {"start": v(-1.43, 94.9) * mm, "end": v(-1.42, 94.9) * mm});
            skLineSegment(sketch, "E535", {"start": v(-1.42, 94.9) * mm, "end": v(-1.38, 94.91) * mm});
            skLineSegment(sketch, "E536", {"start": v(-1.38, 94.91) * mm, "end": v(-1.34, 94.94) * mm});
            skLineSegment(sketch, "E537", {"start": v(-1.34, 94.94) * mm, "end": v(-1.31, 94.98) * mm});
            skLineSegment(sketch, "E538", {"start": v(-1.31, 94.98) * mm, "end": v(-1.3, 95.01) * mm});
            skLineSegment(sketch, "E539", {"start": v(-1.3, 95.01) * mm, "end": v(-1.3, 95.02) * mm});
            skLineSegment(sketch, "E540", {"start": v(-1.3, 95.02) * mm, "end": v(-1.3, 95.03) * mm});
            skLineSegment(sketch, "E541", {"start": v(-1.3, 95.03) * mm, "end": v(-1.3, 95.06) * mm});
            skLineSegment(sketch, "E542", {"start": v(-1.3, 95.06) * mm, "end": v(-1.32, 95.08) * mm});
            skLineSegment(sketch, "E543", {"start": v(-1.32, 95.08) * mm, "end": v(-1.32, 95.09) * mm});
            skLineSegment(sketch, "E544", {"start": v(-1.32, 95.09) * mm, "end": v(-1.32, 95.08) * mm});
            skLineSegment(sketch, "E545", {"start": v(-1.32, 95.08) * mm, "end": v(-1.32, 95.07) * mm});
            skLineSegment(sketch, "E546", {"start": v(-1.32, 95.07) * mm, "end": v(-1.32, 95.07) * mm});
            skLineSegment(sketch, "E547", {"start": v(-2.79, 95) * mm, "end": v(-2.79, 95) * mm});
            skLineSegment(sketch, "E548", {"start": v(-2.79, 95) * mm, "end": v(-2.8, 94.98) * mm});
            skLineSegment(sketch, "E549", {"start": v(-2.8, 94.98) * mm, "end": v(-2.8, 94.96) * mm});
            skLineSegment(sketch, "E550", {"start": v(-2.8, 94.96) * mm, "end": v(-2.83, 94.94) * mm});
            skLineSegment(sketch, "E551", {"start": v(-2.83, 94.94) * mm, "end": v(-2.85, 94.94) * mm});
            skLineSegment(sketch, "E552", {"start": v(-2.85, 94.94) * mm, "end": v(-2.86, 94.94) * mm});
            skLineSegment(sketch, "E553", {"start": v(-2.86, 94.94) * mm, "end": v(-2.87, 94.94) * mm});
            skLineSegment(sketch, "E554", {"start": v(-2.87, 94.94) * mm, "end": v(-2.9, 94.94) * mm});
            skLineSegment(sketch, "E555", {"start": v(-2.9, 94.94) * mm, "end": v(-2.92, 94.96) * mm});
            skLineSegment(sketch, "E556", {"start": v(-2.92, 94.96) * mm, "end": v(-2.93, 94.98) * mm});
            skLineSegment(sketch, "E557", {"start": v(-2.93, 94.98) * mm, "end": v(-2.94, 95) * mm});
            skLineSegment(sketch, "E558", {"start": v(-2.94, 95) * mm, "end": v(-2.94, 95) * mm});
            skLineSegment(sketch, "E559", {"start": v(-2.94, 95) * mm, "end": v(-2.94, 95.01) * mm});
            skLineSegment(sketch, "E560", {"start": v(-2.94, 95.01) * mm, "end": v(-2.93, 95.03) * mm});
            skLineSegment(sketch, "E561", {"start": v(-2.93, 95.03) * mm, "end": v(-2.92, 95.05) * mm});
            skLineSegment(sketch, "E562", {"start": v(-2.92, 95.05) * mm, "end": v(-2.9, 95.07) * mm});
            skLineSegment(sketch, "E563", {"start": v(-2.9, 95.07) * mm, "end": v(-2.88, 95.07) * mm});
            skLineSegment(sketch, "E564", {"start": v(-2.88, 95.07) * mm, "end": v(-2.87, 95.07) * mm});
            skLineSegment(sketch, "E565", {"start": v(-2.87, 95.07) * mm, "end": v(-2.87, 95.07) * mm});
            skLineSegment(sketch, "E566", {"start": v(-2.87, 95.07) * mm, "end": v(-2.89, 95.08) * mm});
            skLineSegment(sketch, "E567", {"start": v(-2.89, 95.08) * mm, "end": v(-2.9, 95.08) * mm});
            skLineSegment(sketch, "E568", {"start": v(-2.9, 95.08) * mm, "end": v(-2.9, 95.08) * mm});
            skLineSegment(sketch, "E569", {"start": v(-2.9, 95.08) * mm, "end": v(-2.94, 95.07) * mm});
            skLineSegment(sketch, "E570", {"start": v(-2.94, 95.07) * mm, "end": v(-2.98, 95.04) * mm});
            skLineSegment(sketch, "E571", {"start": v(-2.98, 95.04) * mm, "end": v(-3, 95) * mm});
            skLineSegment(sketch, "E572", {"start": v(-3, 95) * mm, "end": v(-3.02, 94.97) * mm});
            skLineSegment(sketch, "E573", {"start": v(-3.02, 94.97) * mm, "end": v(-3.02, 94.96) * mm});
            skLineSegment(sketch, "E574", {"start": v(-3.02, 94.96) * mm, "end": v(-3.02, 94.95) * mm});
            skLineSegment(sketch, "E575", {"start": v(-3.02, 94.95) * mm, "end": v(-3, 94.92) * mm});
            skLineSegment(sketch, "E576", {"start": v(-3, 94.92) * mm, "end": v(-2.98, 94.88) * mm});
            skLineSegment(sketch, "E577", {"start": v(-2.98, 94.88) * mm, "end": v(-2.94, 94.85) * mm});
            skLineSegment(sketch, "E578", {"start": v(-2.94, 94.85) * mm, "end": v(-2.9, 94.84) * mm});
            skLineSegment(sketch, "E579", {"start": v(-2.9, 94.84) * mm, "end": v(-2.9, 94.84) * mm});
            skLineSegment(sketch, "E580", {"start": v(-2.9, 94.84) * mm, "end": v(-2.88, 94.84) * mm});
            skLineSegment(sketch, "E581", {"start": v(-2.88, 94.84) * mm, "end": v(-2.84, 94.85) * mm});
            skLineSegment(sketch, "E582", {"start": v(-2.84, 94.85) * mm, "end": v(-2.8, 94.88) * mm});
            skLineSegment(sketch, "E583", {"start": v(-2.8, 94.88) * mm, "end": v(-2.78, 94.92) * mm});
            skLineSegment(sketch, "E584", {"start": v(-2.78, 94.92) * mm, "end": v(-2.77, 94.95) * mm});
            skLineSegment(sketch, "E585", {"start": v(-2.77, 94.95) * mm, "end": v(-2.77, 94.96) * mm});
            skLineSegment(sketch, "E586", {"start": v(-2.77, 94.96) * mm, "end": v(-2.77, 94.97) * mm});
            skLineSegment(sketch, "E587", {"start": v(-2.77, 94.97) * mm, "end": v(-2.77, 95) * mm});
            skLineSegment(sketch, "E588", {"start": v(-2.77, 95) * mm, "end": v(-2.79, 95.02) * mm});
            skLineSegment(sketch, "E589", {"start": v(-2.79, 95.02) * mm, "end": v(-2.79, 95.02) * mm});
            skLineSegment(sketch, "E590", {"start": v(-2.79, 95.02) * mm, "end": v(-2.79, 95.01) * mm});
            skLineSegment(sketch, "E591", {"start": v(-2.79, 95.01) * mm, "end": v(-2.79, 95) * mm});
            skSolve(sketch);
        }
        {
            var Q0;
            Q0=makeQuery(id+"F2.imprint","IMPRINT",FACE,{"disambiguationData":[TD([[makeQuery(id+"F2.imprint","IMPRINT",EDGE,{"derivedFrom":sQuery(id+"F2.wireOp",EDGE,"E6")}),1.0]])]});
            var Q1;
            Q1=makeQuery(id+"F2.imprint","IMPRINT",FACE,{"disambiguationData":[TD([[makeQuery(id+"F2.imprint","IMPRINT",EDGE,{"derivedFrom":sQuery(id+"F2.wireOp",EDGE,"E451")}),1.0]])]});
            var Q2;
            Q2=makeQuery(id+"F2.imprint","IMPRINT",FACE,{"disambiguationData":[TD([[makeQuery(id+"F2.imprint","IMPRINT",EDGE,{"derivedFrom":sQuery(id+"F2.wireOp",EDGE,"E501")}),1.0]])]});
            var Q3;
            Q3=makeQuery(id+"F2.imprint","IMPRINT",FACE,{"disambiguationData":[TD([[makeQuery(id+"F2.imprint","IMPRINT",EDGE,{"derivedFrom":sQuery(id+"F2.wireOp",EDGE,"E405")}),1.0]])]});
            var Q4;
            Q4=makeQuery(id+"F2.imprint","IMPRINT",FACE,{"disambiguationData":[TD([[makeQuery(id+"F2.imprint","IMPRINT",EDGE,{"derivedFrom":sQuery(id+"F2.wireOp",EDGE,"E547")}),1.0]])]});
            extrude(context, id + "F3", {"entities" : qUnion([Q0, Q1, Q2, Q3, Q4]), "depth" : 0.05 * mm});
        }
        {
            var Q0;
            Q0=makeQuery(id+"F3.opExtrude","SWEPT_BODY",BODY,{"disambiguationData":[OSD([sQuery(id+"F2.wireOp",EDGE,"E6"),sQuery(id+"F2.wireOp",EDGE,"E7"),sQuery(id+"F2.wireOp",EDGE,"E8"),sQuery(id+"F2.wireOp",EDGE,"E9"),sQuery(id+"F2.wireOp",EDGE,"E10"),sQuery(id+"F2.wireOp",EDGE,"E11"),sQuery(id+"F2.wireOp",EDGE,"E12"),sQuery(id+"F2.wireOp",EDGE,"E13"),sQuery(id+"F2.wireOp",EDGE,"E15"),sQuery(id+"F2.wireOp",EDGE,"E16"),sQuery(id+"F2.wireOp",EDGE,"E17"),sQuery(id+"F2.wireOp",EDGE,"E18"),sQuery(id+"F2.wireOp",EDGE,"E19"),sQuery(id+"F2.wireOp",EDGE,"E20"),sQuery(id+"F2.wireOp",EDGE,"E21"),sQuery(id+"F2.wireOp",EDGE,"E22"),sQuery(id+"F2.wireOp",EDGE,"E23"),sQuery(id+"F2.wireOp",EDGE,"E24"),sQuery(id+"F2.wireOp",EDGE,"E25"),sQuery(id+"F2.wireOp",EDGE,"E26"),sQuery(id+"F2.wireOp",EDGE,"E27"),sQuery(id+"F2.wireOp",EDGE,"E28"),sQuery(id+"F2.wireOp",EDGE,"E29"),sQuery(id+"F2.wireOp",EDGE,"E30"),sQuery(id+"F2.wireOp",EDGE,"E31"),sQuery(id+"F2.wireOp",EDGE,"E32"),sQuery(id+"F2.wireOp",EDGE,"E33"),sQuery(id+"F2.wireOp",EDGE,"E34"),sQuery(id+"F2.wireOp",EDGE,"E35"),sQuery(id+"F2.wireOp",EDGE,"E36"),sQuery(id+"F2.wireOp",EDGE,"E37"),sQuery(id+"F2.wireOp",EDGE,"E38"),sQuery(id+"F2.wireOp",EDGE,"E39"),sQuery(id+"F2.wireOp",EDGE,"E40"),sQuery(id+"F2.wireOp",EDGE,"E41"),sQuery(id+"F2.wireOp",EDGE,"E42"),sQuery(id+"F2.wireOp",EDGE,"E43"),sQuery(id+"F2.wireOp",EDGE,"E44"),sQuery(id+"F2.wireOp",EDGE,"E45"),sQuery(id+"F2.wireOp",EDGE,"E46"),sQuery(id+"F2.wireOp",EDGE,"E47"),sQuery(id+"F2.wireOp",EDGE,"E48"),sQuery(id+"F2.wireOp",EDGE,"E49"),sQuery(id+"F2.wireOp",EDGE,"E50"),sQuery(id+"F2.wireOp",EDGE,"E51"),sQuery(id+"F2.wireOp",EDGE,"E52"),sQuery(id+"F2.wireOp",EDGE,"E53"),sQuery(id+"F2.wireOp",EDGE,"E54"),sQuery(id+"F2.wireOp",EDGE,"E55"),sQuery(id+"F2.wireOp",EDGE,"E56"),sQuery(id+"F2.wireOp",EDGE,"E57"),sQuery(id+"F2.wireOp",EDGE,"E58"),sQuery(id+"F2.wireOp",EDGE,"E59"),sQuery(id+"F2.wireOp",EDGE,"E60"),sQuery(id+"F2.wireOp",EDGE,"E61"),sQuery(id+"F2.wireOp",EDGE,"E62"),sQuery(id+"F2.wireOp",EDGE,"E63"),sQuery(id+"F2.wireOp",EDGE,"E64"),sQuery(id+"F2.wireOp",EDGE,"E65"),sQuery(id+"F2.wireOp",EDGE,"E66"),sQuery(id+"F2.wireOp",EDGE,"E67"),sQuery(id+"F2.wireOp",EDGE,"E68"),sQuery(id+"F2.wireOp",EDGE,"E69"),sQuery(id+"F2.wireOp",EDGE,"E70"),sQuery(id+"F2.wireOp",EDGE,"E71"),sQuery(id+"F2.wireOp",EDGE,"E72"),sQuery(id+"F2.wireOp",EDGE,"E73"),sQuery(id+"F2.wireOp",EDGE,"E74"),sQuery(id+"F2.wireOp",EDGE,"E75"),sQuery(id+"F2.wireOp",EDGE,"E76"),sQuery(id+"F2.wireOp",EDGE,"E77"),sQuery(id+"F2.wireOp",EDGE,"E78"),sQuery(id+"F2.wireOp",EDGE,"E79"),sQuery(id+"F2.wireOp",EDGE,"E80"),sQuery(id+"F2.wireOp",EDGE,"E81"),sQuery(id+"F2.wireOp",EDGE,"E83"),sQuery(id+"F2.wireOp",EDGE,"E84"),sQuery(id+"F2.wireOp",EDGE,"E85"),sQuery(id+"F2.wireOp",EDGE,"E86"),sQuery(id+"F2.wireOp",EDGE,"E87"),sQuery(id+"F2.wireOp",EDGE,"E88"),sQuery(id+"F2.wireOp",EDGE,"E89"),sQuery(id+"F2.wireOp",EDGE,"E90"),sQuery(id+"F2.wireOp",EDGE,"E91"),sQuery(id+"F2.wireOp",EDGE,"E92"),sQuery(id+"F2.wireOp",EDGE,"E93"),sQuery(id+"F2.wireOp",EDGE,"E94"),sQuery(id+"F2.wireOp",EDGE,"E95"),sQuery(id+"F2.wireOp",EDGE,"E96"),sQuery(id+"F2.wireOp",EDGE,"E97"),sQuery(id+"F2.wireOp",EDGE,"E98"),sQuery(id+"F2.wireOp",EDGE,"E99"),sQuery(id+"F2.wireOp",EDGE,"E100"),sQuery(id+"F2.wireOp",EDGE,"E101"),sQuery(id+"F2.wireOp",EDGE,"E102"),sQuery(id+"F2.wireOp",EDGE,"E103"),sQuery(id+"F2.wireOp",EDGE,"E104"),sQuery(id+"F2.wireOp",EDGE,"E105"),sQuery(id+"F2.wireOp",EDGE,"E106"),sQuery(id+"F2.wireOp",EDGE,"E107"),sQuery(id+"F2.wireOp",EDGE,"E108"),sQuery(id+"F2.wireOp",EDGE,"E109"),sQuery(id+"F2.wireOp",EDGE,"E110"),sQuery(id+"F2.wireOp",EDGE,"E111"),sQuery(id+"F2.wireOp",EDGE,"E112"),sQuery(id+"F2.wireOp",EDGE,"E113"),sQuery(id+"F2.wireOp",EDGE,"E114"),sQuery(id+"F2.wireOp",EDGE,"E115"),sQuery(id+"F2.wireOp",EDGE,"E116"),sQuery(id+"F2.wireOp",EDGE,"E117"),sQuery(id+"F2.wireOp",EDGE,"E118"),sQuery(id+"F2.wireOp",EDGE,"E119"),sQuery(id+"F2.wireOp",EDGE,"E120"),sQuery(id+"F2.wireOp",EDGE,"E121"),sQuery(id+"F2.wireOp",EDGE,"E122"),sQuery(id+"F2.wireOp",EDGE,"E123"),sQuery(id+"F2.wireOp",EDGE,"E124"),sQuery(id+"F2.wireOp",EDGE,"E125"),sQuery(id+"F2.wireOp",EDGE,"E126"),sQuery(id+"F2.wireOp",EDGE,"E127"),sQuery(id+"F2.wireOp",EDGE,"E128"),sQuery(id+"F2.wireOp",EDGE,"E129"),sQuery(id+"F2.wireOp",EDGE,"E130"),sQuery(id+"F2.wireOp",EDGE,"E131"),sQuery(id+"F2.wireOp",EDGE,"E132"),sQuery(id+"F2.wireOp",EDGE,"E133"),sQuery(id+"F2.wireOp",EDGE,"E134"),sQuery(id+"F2.wireOp",EDGE,"E135"),sQuery(id+"F2.wireOp",EDGE,"E136"),sQuery(id+"F2.wireOp",EDGE,"E137"),sQuery(id+"F2.wireOp",EDGE,"E138"),sQuery(id+"F2.wireOp",EDGE,"E139"),sQuery(id+"F2.wireOp",EDGE,"E140"),sQuery(id+"F2.wireOp",EDGE,"E141"),sQuery(id+"F2.wireOp",EDGE,"E142"),sQuery(id+"F2.wireOp",EDGE,"E143"),sQuery(id+"F2.wireOp",EDGE,"E144"),sQuery(id+"F2.wireOp",EDGE,"E145"),sQuery(id+"F2.wireOp",EDGE,"E146"),sQuery(id+"F2.wireOp",EDGE,"E147"),sQuery(id+"F2.wireOp",EDGE,"E148"),sQuery(id+"F2.wireOp",EDGE,"E149"),sQuery(id+"F2.wireOp",EDGE,"E150"),sQuery(id+"F2.wireOp",EDGE,"E151"),sQuery(id+"F2.wireOp",EDGE,"E152"),sQuery(id+"F2.wireOp",EDGE,"E153"),sQuery(id+"F2.wireOp",EDGE,"E154"),sQuery(id+"F2.wireOp",EDGE,"E155"),sQuery(id+"F2.wireOp",EDGE,"E156"),sQuery(id+"F2.wireOp",EDGE,"E157"),sQuery(id+"F2.wireOp",EDGE,"E158"),sQuery(id+"F2.wireOp",EDGE,"E159"),sQuery(id+"F2.wireOp",EDGE,"E160"),sQuery(id+"F2.wireOp",EDGE,"E161"),sQuery(id+"F2.wireOp",EDGE,"E162"),sQuery(id+"F2.wireOp",EDGE,"E163"),sQuery(id+"F2.wireOp",EDGE,"E164"),sQuery(id+"F2.wireOp",EDGE,"E165"),sQuery(id+"F2.wireOp",EDGE,"E166"),sQuery(id+"F2.wireOp",EDGE,"E167"),sQuery(id+"F2.wireOp",EDGE,"E168"),sQuery(id+"F2.wireOp",EDGE,"E169"),sQuery(id+"F2.wireOp",EDGE,"E170"),sQuery(id+"F2.wireOp",EDGE,"E171"),sQuery(id+"F2.wireOp",EDGE,"E172"),sQuery(id+"F2.wireOp",EDGE,"E173"),sQuery(id+"F2.wireOp",EDGE,"E174"),sQuery(id+"F2.wireOp",EDGE,"E175"),sQuery(id+"F2.wireOp",EDGE,"E176"),sQuery(id+"F2.wireOp",EDGE,"E177"),sQuery(id+"F2.wireOp",EDGE,"E178"),sQuery(id+"F2.wireOp",EDGE,"E179"),sQuery(id+"F2.wireOp",EDGE,"E180"),sQuery(id+"F2.wireOp",EDGE,"E181"),sQuery(id+"F2.wireOp",EDGE,"E182"),sQuery(id+"F2.wireOp",EDGE,"E183"),sQuery(id+"F2.wireOp",EDGE,"E184"),sQuery(id+"F2.wireOp",EDGE,"E185"),sQuery(id+"F2.wireOp",EDGE,"E186"),sQuery(id+"F2.wireOp",EDGE,"E187"),sQuery(id+"F2.wireOp",EDGE,"E188"),sQuery(id+"F2.wireOp",EDGE,"E189"),sQuery(id+"F2.wireOp",EDGE,"E190"),sQuery(id+"F2.wireOp",EDGE,"E191"),sQuery(id+"F2.wireOp",EDGE,"E192"),sQuery(id+"F2.wireOp",EDGE,"E193"),sQuery(id+"F2.wireOp",EDGE,"E194"),sQuery(id+"F2.wireOp",EDGE,"E195"),sQuery(id+"F2.wireOp",EDGE,"E196"),sQuery(id+"F2.wireOp",EDGE,"E197"),sQuery(id+"F2.wireOp",EDGE,"E198"),sQuery(id+"F2.wireOp",EDGE,"E199"),sQuery(id+"F2.wireOp",EDGE,"E200"),sQuery(id+"F2.wireOp",EDGE,"E201"),sQuery(id+"F2.wireOp",EDGE,"E202"),sQuery(id+"F2.wireOp",EDGE,"E203"),sQuery(id+"F2.wireOp",EDGE,"E204"),sQuery(id+"F2.wireOp",EDGE,"E205"),sQuery(id+"F2.wireOp",EDGE,"E206"),sQuery(id+"F2.wireOp",EDGE,"E207"),sQuery(id+"F2.wireOp",EDGE,"E208"),sQuery(id+"F2.wireOp",EDGE,"E209"),sQuery(id+"F2.wireOp",EDGE,"E210"),sQuery(id+"F2.wireOp",EDGE,"E210"),sQuery(id+"F2.wireOp",EDGE,"E211"),sQuery(id+"F2.wireOp",EDGE,"E212"),sQuery(id+"F2.wireOp",EDGE,"E212"),sQuery(id+"F2.wireOp",EDGE,"E213"),sQuery(id+"F2.wireOp",EDGE,"E214"),sQuery(id+"F2.wireOp",EDGE,"E215"),sQuery(id+"F2.wireOp",EDGE,"E216"),sQuery(id+"F2.wireOp",EDGE,"E217"),sQuery(id+"F2.wireOp",EDGE,"E218"),sQuery(id+"F2.wireOp",EDGE,"E219"),sQuery(id+"F2.wireOp",EDGE,"E220"),sQuery(id+"F2.wireOp",EDGE,"E221"),sQuery(id+"F2.wireOp",EDGE,"E222"),sQuery(id+"F2.wireOp",EDGE,"E223"),sQuery(id+"F2.wireOp",EDGE,"E224"),sQuery(id+"F2.wireOp",EDGE,"E225"),sQuery(id+"F2.wireOp",EDGE,"E226"),sQuery(id+"F2.wireOp",EDGE,"E227"),sQuery(id+"F2.wireOp",EDGE,"E228"),sQuery(id+"F2.wireOp",EDGE,"E229"),sQuery(id+"F2.wireOp",EDGE,"E230"),sQuery(id+"F2.wireOp",EDGE,"E231"),sQuery(id+"F2.wireOp",EDGE,"E232"),sQuery(id+"F2.wireOp",EDGE,"E233"),sQuery(id+"F2.wireOp",EDGE,"E234"),sQuery(id+"F2.wireOp",EDGE,"E235"),sQuery(id+"F2.wireOp",EDGE,"E236"),sQuery(id+"F2.wireOp",EDGE,"E237"),sQuery(id+"F2.wireOp",EDGE,"E238"),sQuery(id+"F2.wireOp",EDGE,"E239"),sQuery(id+"F2.wireOp",EDGE,"E240"),sQuery(id+"F2.wireOp",EDGE,"E241"),sQuery(id+"F2.wireOp",EDGE,"E242"),sQuery(id+"F2.wireOp",EDGE,"E243"),sQuery(id+"F2.wireOp",EDGE,"E244"),sQuery(id+"F2.wireOp",EDGE,"E245"),sQuery(id+"F2.wireOp",EDGE,"E246"),sQuery(id+"F2.wireOp",EDGE,"E247"),sQuery(id+"F2.wireOp",EDGE,"E248"),sQuery(id+"F2.wireOp",EDGE,"E249"),sQuery(id+"F2.wireOp",EDGE,"E250"),sQuery(id+"F2.wireOp",EDGE,"E251"),sQuery(id+"F2.wireOp",EDGE,"E252"),sQuery(id+"F2.wireOp",EDGE,"E253"),sQuery(id+"F2.wireOp",EDGE,"E254"),sQuery(id+"F2.wireOp",EDGE,"E255"),sQuery(id+"F2.wireOp",EDGE,"E256"),sQuery(id+"F2.wireOp",EDGE,"E257"),sQuery(id+"F2.wireOp",EDGE,"E258"),sQuery(id+"F2.wireOp",EDGE,"E259"),sQuery(id+"F2.wireOp",EDGE,"E260"),sQuery(id+"F2.wireOp",EDGE,"E261"),sQuery(id+"F2.wireOp",EDGE,"E262"),sQuery(id+"F2.wireOp",EDGE,"E263"),sQuery(id+"F2.wireOp",EDGE,"E264"),sQuery(id+"F2.wireOp",EDGE,"E265"),sQuery(id+"F2.wireOp",EDGE,"E266"),sQuery(id+"F2.wireOp",EDGE,"E267"),sQuery(id+"F2.wireOp",EDGE,"E268"),sQuery(id+"F2.wireOp",EDGE,"E269"),sQuery(id+"F2.wireOp",EDGE,"E270"),sQuery(id+"F2.wireOp",EDGE,"E271"),sQuery(id+"F2.wireOp",EDGE,"E272"),sQuery(id+"F2.wireOp",EDGE,"E273"),sQuery(id+"F2.wireOp",EDGE,"E274"),sQuery(id+"F2.wireOp",EDGE,"E275"),sQuery(id+"F2.wireOp",EDGE,"E276"),sQuery(id+"F2.wireOp",EDGE,"E277"),sQuery(id+"F2.wireOp",EDGE,"E278"),sQuery(id+"F2.wireOp",EDGE,"E279"),sQuery(id+"F2.wireOp",EDGE,"E280"),sQuery(id+"F2.wireOp",EDGE,"E281"),sQuery(id+"F2.wireOp",EDGE,"E282"),sQuery(id+"F2.wireOp",EDGE,"E283"),sQuery(id+"F2.wireOp",EDGE,"E284"),sQuery(id+"F2.wireOp",EDGE,"E285"),sQuery(id+"F2.wireOp",EDGE,"E286"),sQuery(id+"F2.wireOp",EDGE,"E287"),sQuery(id+"F2.wireOp",EDGE,"E288"),sQuery(id+"F2.wireOp",EDGE,"E289"),sQuery(id+"F2.wireOp",EDGE,"E290"),sQuery(id+"F2.wireOp",EDGE,"E291"),sQuery(id+"F2.wireOp",EDGE,"E292"),sQuery(id+"F2.wireOp",EDGE,"E293"),sQuery(id+"F2.wireOp",EDGE,"E294"),sQuery(id+"F2.wireOp",EDGE,"E295"),sQuery(id+"F2.wireOp",EDGE,"E296"),sQuery(id+"F2.wireOp",EDGE,"E297"),sQuery(id+"F2.wireOp",EDGE,"E298"),sQuery(id+"F2.wireOp",EDGE,"E299"),sQuery(id+"F2.wireOp",EDGE,"E300"),sQuery(id+"F2.wireOp",EDGE,"E301"),sQuery(id+"F2.wireOp",EDGE,"E302"),sQuery(id+"F2.wireOp",EDGE,"E303"),sQuery(id+"F2.wireOp",EDGE,"E304"),sQuery(id+"F2.wireOp",EDGE,"E305"),sQuery(id+"F2.wireOp",EDGE,"E306"),sQuery(id+"F2.wireOp",EDGE,"E307"),sQuery(id+"F2.wireOp",EDGE,"E308"),sQuery(id+"F2.wireOp",EDGE,"E309"),sQuery(id+"F2.wireOp",EDGE,"E310"),sQuery(id+"F2.wireOp",EDGE,"E311"),sQuery(id+"F2.wireOp",EDGE,"E312"),sQuery(id+"F2.wireOp",EDGE,"E313"),sQuery(id+"F2.wireOp",EDGE,"E314"),sQuery(id+"F2.wireOp",EDGE,"E315"),sQuery(id+"F2.wireOp",EDGE,"E316"),sQuery(id+"F2.wireOp",EDGE,"E317"),sQuery(id+"F2.wireOp",EDGE,"E318"),sQuery(id+"F2.wireOp",EDGE,"E319"),sQuery(id+"F2.wireOp",EDGE,"E320"),sQuery(id+"F2.wireOp",EDGE,"E321"),sQuery(id+"F2.wireOp",EDGE,"E322"),sQuery(id+"F2.wireOp",EDGE,"E323"),sQuery(id+"F2.wireOp",EDGE,"E324"),sQuery(id+"F2.wireOp",EDGE,"E325"),sQuery(id+"F2.wireOp",EDGE,"E326"),sQuery(id+"F2.wireOp",EDGE,"E327"),sQuery(id+"F2.wireOp",EDGE,"E328"),sQuery(id+"F2.wireOp",EDGE,"E329"),sQuery(id+"F2.wireOp",EDGE,"E330"),sQuery(id+"F2.wireOp",EDGE,"E331"),sQuery(id+"F2.wireOp",EDGE,"E332"),sQuery(id+"F2.wireOp",EDGE,"E333"),sQuery(id+"F2.wireOp",EDGE,"E334"),sQuery(id+"F2.wireOp",EDGE,"E335"),sQuery(id+"F2.wireOp",EDGE,"E336"),sQuery(id+"F2.wireOp",EDGE,"E337"),sQuery(id+"F2.wireOp",EDGE,"E338"),sQuery(id+"F2.wireOp",EDGE,"E339"),sQuery(id+"F2.wireOp",EDGE,"E340"),sQuery(id+"F2.wireOp",EDGE,"E341"),sQuery(id+"F2.wireOp",EDGE,"E342"),sQuery(id+"F2.wireOp",EDGE,"E343"),sQuery(id+"F2.wireOp",EDGE,"E344"),sQuery(id+"F2.wireOp",EDGE,"E345"),sQuery(id+"F2.wireOp",EDGE,"E346"),sQuery(id+"F2.wireOp",EDGE,"E347"),sQuery(id+"F2.wireOp",EDGE,"E348"),sQuery(id+"F2.wireOp",EDGE,"E349"),sQuery(id+"F2.wireOp",EDGE,"E350"),sQuery(id+"F2.wireOp",EDGE,"E351"),sQuery(id+"F2.wireOp",EDGE,"E352"),sQuery(id+"F2.wireOp",EDGE,"E353"),sQuery(id+"F2.wireOp",EDGE,"E354"),sQuery(id+"F2.wireOp",EDGE,"E355"),sQuery(id+"F2.wireOp",EDGE,"E356"),sQuery(id+"F2.wireOp",EDGE,"E357"),sQuery(id+"F2.wireOp",EDGE,"E358"),sQuery(id+"F2.wireOp",EDGE,"E359"),sQuery(id+"F2.wireOp",EDGE,"E360"),sQuery(id+"F2.wireOp",EDGE,"E361"),sQuery(id+"F2.wireOp",EDGE,"E362"),sQuery(id+"F2.wireOp",EDGE,"E363"),sQuery(id+"F2.wireOp",EDGE,"E364"),sQuery(id+"F2.wireOp",EDGE,"E365"),sQuery(id+"F2.wireOp",EDGE,"E366"),sQuery(id+"F2.wireOp",EDGE,"E367"),sQuery(id+"F2.wireOp",EDGE,"E368"),sQuery(id+"F2.wireOp",EDGE,"E369"),sQuery(id+"F2.wireOp",EDGE,"E370"),sQuery(id+"F2.wireOp",EDGE,"E371"),sQuery(id+"F2.wireOp",EDGE,"E372"),sQuery(id+"F2.wireOp",EDGE,"E373"),sQuery(id+"F2.wireOp",EDGE,"E374"),sQuery(id+"F2.wireOp",EDGE,"E375"),sQuery(id+"F2.wireOp",EDGE,"E376"),sQuery(id+"F2.wireOp",EDGE,"E377"),sQuery(id+"F2.wireOp",EDGE,"E378"),sQuery(id+"F2.wireOp",EDGE,"E379"),sQuery(id+"F2.wireOp",EDGE,"E380"),sQuery(id+"F2.wireOp",EDGE,"E381"),sQuery(id+"F2.wireOp",EDGE,"E382"),sQuery(id+"F2.wireOp",EDGE,"E383"),sQuery(id+"F2.wireOp",EDGE,"E384"),sQuery(id+"F2.wireOp",EDGE,"E385"),sQuery(id+"F2.wireOp",EDGE,"E386"),sQuery(id+"F2.wireOp",EDGE,"E387"),sQuery(id+"F2.wireOp",EDGE,"E388"),sQuery(id+"F2.wireOp",EDGE,"E389"),sQuery(id+"F2.wireOp",EDGE,"E390"),sQuery(id+"F2.wireOp",EDGE,"E391"),sQuery(id+"F2.wireOp",EDGE,"E392"),sQuery(id+"F2.wireOp",EDGE,"E393"),sQuery(id+"F2.wireOp",EDGE,"E394"),sQuery(id+"F2.wireOp",EDGE,"E395"),sQuery(id+"F2.wireOp",EDGE,"E396"),sQuery(id+"F2.wireOp",EDGE,"E397"),sQuery(id+"F2.wireOp",EDGE,"E398"),sQuery(id+"F2.wireOp",EDGE,"E399"),sQuery(id+"F2.wireOp",EDGE,"E400"),sQuery(id+"F2.wireOp",EDGE,"E401"),sQuery(id+"F2.wireOp",EDGE,"E402"),sQuery(id+"F2.wireOp",EDGE,"E403"),sQuery(id+"F2.wireOp",EDGE,"E404"),sQuery(id+"F2.wireOp",EDGE,"E500")])]});
            var Q1;
            Q1=makeQuery(id+"F3.opExtrude","SWEPT_BODY",BODY,{"disambiguationData":[OSD([sQuery(id+"F2.wireOp",EDGE,"E547"),sQuery(id+"F2.wireOp",EDGE,"E548"),sQuery(id+"F2.wireOp",EDGE,"E549"),sQuery(id+"F2.wireOp",EDGE,"E550"),sQuery(id+"F2.wireOp",EDGE,"E551"),sQuery(id+"F2.wireOp",EDGE,"E552"),sQuery(id+"F2.wireOp",EDGE,"E553"),sQuery(id+"F2.wireOp",EDGE,"E554"),sQuery(id+"F2.wireOp",EDGE,"E555"),sQuery(id+"F2.wireOp",EDGE,"E556"),sQuery(id+"F2.wireOp",EDGE,"E557"),sQuery(id+"F2.wireOp",EDGE,"E558"),sQuery(id+"F2.wireOp",EDGE,"E559"),sQuery(id+"F2.wireOp",EDGE,"E560"),sQuery(id+"F2.wireOp",EDGE,"E561"),sQuery(id+"F2.wireOp",EDGE,"E562"),sQuery(id+"F2.wireOp",EDGE,"E563"),sQuery(id+"F2.wireOp",EDGE,"E564"),sQuery(id+"F2.wireOp",EDGE,"E565"),sQuery(id+"F2.wireOp",EDGE,"E566"),sQuery(id+"F2.wireOp",EDGE,"E567"),sQuery(id+"F2.wireOp",EDGE,"E568"),sQuery(id+"F2.wireOp",EDGE,"E569"),sQuery(id+"F2.wireOp",EDGE,"E570"),sQuery(id+"F2.wireOp",EDGE,"E571"),sQuery(id+"F2.wireOp",EDGE,"E572"),sQuery(id+"F2.wireOp",EDGE,"E573"),sQuery(id+"F2.wireOp",EDGE,"E574"),sQuery(id+"F2.wireOp",EDGE,"E575"),sQuery(id+"F2.wireOp",EDGE,"E576"),sQuery(id+"F2.wireOp",EDGE,"E577"),sQuery(id+"F2.wireOp",EDGE,"E578"),sQuery(id+"F2.wireOp",EDGE,"E579"),sQuery(id+"F2.wireOp",EDGE,"E580"),sQuery(id+"F2.wireOp",EDGE,"E581"),sQuery(id+"F2.wireOp",EDGE,"E582"),sQuery(id+"F2.wireOp",EDGE,"E583"),sQuery(id+"F2.wireOp",EDGE,"E584"),sQuery(id+"F2.wireOp",EDGE,"E585"),sQuery(id+"F2.wireOp",EDGE,"E586"),sQuery(id+"F2.wireOp",EDGE,"E587"),sQuery(id+"F2.wireOp",EDGE,"E588"),sQuery(id+"F2.wireOp",EDGE,"E589"),sQuery(id+"F2.wireOp",EDGE,"E589"),sQuery(id+"F2.wireOp",EDGE,"E590"),sQuery(id+"F2.wireOp",EDGE,"E591")])]});
            var Q2;
            Q2=makeQuery(id+"F3.opExtrude","SWEPT_BODY",BODY,{"disambiguationData":[OSD([sQuery(id+"F2.wireOp",EDGE,"E451"),sQuery(id+"F2.wireOp",EDGE,"E452"),sQuery(id+"F2.wireOp",EDGE,"E453"),sQuery(id+"F2.wireOp",EDGE,"E454"),sQuery(id+"F2.wireOp",EDGE,"E455"),sQuery(id+"F2.wireOp",EDGE,"E456"),sQuery(id+"F2.wireOp",EDGE,"E457"),sQuery(id+"F2.wireOp",EDGE,"E458"),sQuery(id+"F2.wireOp",EDGE,"E459"),sQuery(id+"F2.wireOp",EDGE,"E460"),sQuery(id+"F2.wireOp",EDGE,"E461"),sQuery(id+"F2.wireOp",EDGE,"E462"),sQuery(id+"F2.wireOp",EDGE,"E463"),sQuery(id+"F2.wireOp",EDGE,"E464"),sQuery(id+"F2.wireOp",EDGE,"E465"),sQuery(id+"F2.wireOp",EDGE,"E466"),sQuery(id+"F2.wireOp",EDGE,"E467"),sQuery(id+"F2.wireOp",EDGE,"E468"),sQuery(id+"F2.wireOp",EDGE,"E469"),sQuery(id+"F2.wireOp",EDGE,"E470"),sQuery(id+"F2.wireOp",EDGE,"E471"),sQuery(id+"F2.wireOp",EDGE,"E472"),sQuery(id+"F2.wireOp",EDGE,"E473"),sQuery(id+"F2.wireOp",EDGE,"E474"),sQuery(id+"F2.wireOp",EDGE,"E475"),sQuery(id+"F2.wireOp",EDGE,"E476"),sQuery(id+"F2.wireOp",EDGE,"E477"),sQuery(id+"F2.wireOp",EDGE,"E478"),sQuery(id+"F2.wireOp",EDGE,"E479"),sQuery(id+"F2.wireOp",EDGE,"E480"),sQuery(id+"F2.wireOp",EDGE,"E481"),sQuery(id+"F2.wireOp",EDGE,"E482"),sQuery(id+"F2.wireOp",EDGE,"E483"),sQuery(id+"F2.wireOp",EDGE,"E484"),sQuery(id+"F2.wireOp",EDGE,"E485"),sQuery(id+"F2.wireOp",EDGE,"E486"),sQuery(id+"F2.wireOp",EDGE,"E487"),sQuery(id+"F2.wireOp",EDGE,"E488"),sQuery(id+"F2.wireOp",EDGE,"E489"),sQuery(id+"F2.wireOp",EDGE,"E490"),sQuery(id+"F2.wireOp",EDGE,"E491"),sQuery(id+"F2.wireOp",EDGE,"E492"),sQuery(id+"F2.wireOp",EDGE,"E493"),sQuery(id+"F2.wireOp",EDGE,"E493"),sQuery(id+"F2.wireOp",EDGE,"E494"),sQuery(id+"F2.wireOp",EDGE,"E495")])]});
            var Q3;
            Q3=makeQuery(id+"F3.opExtrude","SWEPT_BODY",BODY,{"disambiguationData":[OSD([sQuery(id+"F2.wireOp",EDGE,"E501"),sQuery(id+"F2.wireOp",EDGE,"E502"),sQuery(id+"F2.wireOp",EDGE,"E503"),sQuery(id+"F2.wireOp",EDGE,"E504"),sQuery(id+"F2.wireOp",EDGE,"E505"),sQuery(id+"F2.wireOp",EDGE,"E506"),sQuery(id+"F2.wireOp",EDGE,"E507"),sQuery(id+"F2.wireOp",EDGE,"E508"),sQuery(id+"F2.wireOp",EDGE,"E509"),sQuery(id+"F2.wireOp",EDGE,"E510"),sQuery(id+"F2.wireOp",EDGE,"E511"),sQuery(id+"F2.wireOp",EDGE,"E512"),sQuery(id+"F2.wireOp",EDGE,"E513"),sQuery(id+"F2.wireOp",EDGE,"E514"),sQuery(id+"F2.wireOp",EDGE,"E515"),sQuery(id+"F2.wireOp",EDGE,"E516"),sQuery(id+"F2.wireOp",EDGE,"E517"),sQuery(id+"F2.wireOp",EDGE,"E518"),sQuery(id+"F2.wireOp",EDGE,"E519"),sQuery(id+"F2.wireOp",EDGE,"E520"),sQuery(id+"F2.wireOp",EDGE,"E521"),sQuery(id+"F2.wireOp",EDGE,"E522"),sQuery(id+"F2.wireOp",EDGE,"E523"),sQuery(id+"F2.wireOp",EDGE,"E524"),sQuery(id+"F2.wireOp",EDGE,"E525"),sQuery(id+"F2.wireOp",EDGE,"E526"),sQuery(id+"F2.wireOp",EDGE,"E527"),sQuery(id+"F2.wireOp",EDGE,"E528"),sQuery(id+"F2.wireOp",EDGE,"E529"),sQuery(id+"F2.wireOp",EDGE,"E530"),sQuery(id+"F2.wireOp",EDGE,"E531"),sQuery(id+"F2.wireOp",EDGE,"E532"),sQuery(id+"F2.wireOp",EDGE,"E533"),sQuery(id+"F2.wireOp",EDGE,"E534"),sQuery(id+"F2.wireOp",EDGE,"E535"),sQuery(id+"F2.wireOp",EDGE,"E536"),sQuery(id+"F2.wireOp",EDGE,"E537"),sQuery(id+"F2.wireOp",EDGE,"E538"),sQuery(id+"F2.wireOp",EDGE,"E539"),sQuery(id+"F2.wireOp",EDGE,"E540"),sQuery(id+"F2.wireOp",EDGE,"E541"),sQuery(id+"F2.wireOp",EDGE,"E542"),sQuery(id+"F2.wireOp",EDGE,"E543"),sQuery(id+"F2.wireOp",EDGE,"E544"),sQuery(id+"F2.wireOp",EDGE,"E545"),sQuery(id+"F2.wireOp",EDGE,"E546")])]});
            var Q4;
            Q4=makeQuery(id+"F3.opExtrude","SWEPT_BODY",BODY,{"disambiguationData":[OSD([sQuery(id+"F2.wireOp",EDGE,"E405"),sQuery(id+"F2.wireOp",EDGE,"E406"),sQuery(id+"F2.wireOp",EDGE,"E407"),sQuery(id+"F2.wireOp",EDGE,"E408"),sQuery(id+"F2.wireOp",EDGE,"E409"),sQuery(id+"F2.wireOp",EDGE,"E410"),sQuery(id+"F2.wireOp",EDGE,"E411"),sQuery(id+"F2.wireOp",EDGE,"E412"),sQuery(id+"F2.wireOp",EDGE,"E413"),sQuery(id+"F2.wireOp",EDGE,"E414"),sQuery(id+"F2.wireOp",EDGE,"E415"),sQuery(id+"F2.wireOp",EDGE,"E416"),sQuery(id+"F2.wireOp",EDGE,"E417"),sQuery(id+"F2.wireOp",EDGE,"E418"),sQuery(id+"F2.wireOp",EDGE,"E419"),sQuery(id+"F2.wireOp",EDGE,"E420"),sQuery(id+"F2.wireOp",EDGE,"E421"),sQuery(id+"F2.wireOp",EDGE,"E422"),sQuery(id+"F2.wireOp",EDGE,"E423"),sQuery(id+"F2.wireOp",EDGE,"E424"),sQuery(id+"F2.wireOp",EDGE,"E425"),sQuery(id+"F2.wireOp",EDGE,"E426"),sQuery(id+"F2.wireOp",EDGE,"E427"),sQuery(id+"F2.wireOp",EDGE,"E428"),sQuery(id+"F2.wireOp",EDGE,"E429"),sQuery(id+"F2.wireOp",EDGE,"E430"),sQuery(id+"F2.wireOp",EDGE,"E431"),sQuery(id+"F2.wireOp",EDGE,"E432"),sQuery(id+"F2.wireOp",EDGE,"E433"),sQuery(id+"F2.wireOp",EDGE,"E434"),sQuery(id+"F2.wireOp",EDGE,"E435"),sQuery(id+"F2.wireOp",EDGE,"E436"),sQuery(id+"F2.wireOp",EDGE,"E437"),sQuery(id+"F2.wireOp",EDGE,"E438"),sQuery(id+"F2.wireOp",EDGE,"E439"),sQuery(id+"F2.wireOp",EDGE,"E440"),sQuery(id+"F2.wireOp",EDGE,"E441"),sQuery(id+"F2.wireOp",EDGE,"E442"),sQuery(id+"F2.wireOp",EDGE,"E443"),sQuery(id+"F2.wireOp",EDGE,"E444"),sQuery(id+"F2.wireOp",EDGE,"E445"),sQuery(id+"F2.wireOp",EDGE,"E446"),sQuery(id+"F2.wireOp",EDGE,"E447"),sQuery(id+"F2.wireOp",EDGE,"E448"),sQuery(id+"F2.wireOp",EDGE,"E449"),sQuery(id+"F2.wireOp",EDGE,"E450")])]});
            var Q5;
            Q5=makeQuery(id+"F3.opExtrude","CAP_VERTEX",VERTEX,{"disambiguationData":[OSD([sQuery(id+"F2.wireOp",EDGE,"E543"),sQuery(id+"F2.wireOp",EDGE,"E544")])],"isStart":true});
            transform(context, id + "F4", {"entities" : qUnion([Q0, Q1, Q2, Q3, Q4]), "transformType" : TransformType.SCALE_UNIFORMLY, "scale" : 23, "scalePoint" : qUnion([Q5]), "makeCopy" : false});
        }
        {
            var Q0;
            Q0=makeQuery(id+"F3.opExtrude","SWEPT_BODY",BODY,{"disambiguationData":[OSD([sQuery(id+"F2.wireOp",EDGE,"E6"),sQuery(id+"F2.wireOp",EDGE,"E7"),sQuery(id+"F2.wireOp",EDGE,"E8"),sQuery(id+"F2.wireOp",EDGE,"E9"),sQuery(id+"F2.wireOp",EDGE,"E10"),sQuery(id+"F2.wireOp",EDGE,"E11"),sQuery(id+"F2.wireOp",EDGE,"E12"),sQuery(id+"F2.wireOp",EDGE,"E13"),sQuery(id+"F2.wireOp",EDGE,"E15"),sQuery(id+"F2.wireOp",EDGE,"E16"),sQuery(id+"F2.wireOp",EDGE,"E17"),sQuery(id+"F2.wireOp",EDGE,"E18"),sQuery(id+"F2.wireOp",EDGE,"E19"),sQuery(id+"F2.wireOp",EDGE,"E20"),sQuery(id+"F2.wireOp",EDGE,"E21"),sQuery(id+"F2.wireOp",EDGE,"E22"),sQuery(id+"F2.wireOp",EDGE,"E23"),sQuery(id+"F2.wireOp",EDGE,"E24"),sQuery(id+"F2.wireOp",EDGE,"E25"),sQuery(id+"F2.wireOp",EDGE,"E26"),sQuery(id+"F2.wireOp",EDGE,"E27"),sQuery(id+"F2.wireOp",EDGE,"E28"),sQuery(id+"F2.wireOp",EDGE,"E29"),sQuery(id+"F2.wireOp",EDGE,"E30"),sQuery(id+"F2.wireOp",EDGE,"E31"),sQuery(id+"F2.wireOp",EDGE,"E32"),sQuery(id+"F2.wireOp",EDGE,"E33"),sQuery(id+"F2.wireOp",EDGE,"E34"),sQuery(id+"F2.wireOp",EDGE,"E35"),sQuery(id+"F2.wireOp",EDGE,"E36"),sQuery(id+"F2.wireOp",EDGE,"E37"),sQuery(id+"F2.wireOp",EDGE,"E38"),sQuery(id+"F2.wireOp",EDGE,"E39"),sQuery(id+"F2.wireOp",EDGE,"E40"),sQuery(id+"F2.wireOp",EDGE,"E41"),sQuery(id+"F2.wireOp",EDGE,"E42"),sQuery(id+"F2.wireOp",EDGE,"E43"),sQuery(id+"F2.wireOp",EDGE,"E44"),sQuery(id+"F2.wireOp",EDGE,"E45"),sQuery(id+"F2.wireOp",EDGE,"E46"),sQuery(id+"F2.wireOp",EDGE,"E47"),sQuery(id+"F2.wireOp",EDGE,"E48"),sQuery(id+"F2.wireOp",EDGE,"E49"),sQuery(id+"F2.wireOp",EDGE,"E50"),sQuery(id+"F2.wireOp",EDGE,"E51"),sQuery(id+"F2.wireOp",EDGE,"E52"),sQuery(id+"F2.wireOp",EDGE,"E53"),sQuery(id+"F2.wireOp",EDGE,"E54"),sQuery(id+"F2.wireOp",EDGE,"E55"),sQuery(id+"F2.wireOp",EDGE,"E56"),sQuery(id+"F2.wireOp",EDGE,"E57"),sQuery(id+"F2.wireOp",EDGE,"E58"),sQuery(id+"F2.wireOp",EDGE,"E59"),sQuery(id+"F2.wireOp",EDGE,"E60"),sQuery(id+"F2.wireOp",EDGE,"E61"),sQuery(id+"F2.wireOp",EDGE,"E62"),sQuery(id+"F2.wireOp",EDGE,"E63"),sQuery(id+"F2.wireOp",EDGE,"E64"),sQuery(id+"F2.wireOp",EDGE,"E65"),sQuery(id+"F2.wireOp",EDGE,"E66"),sQuery(id+"F2.wireOp",EDGE,"E67"),sQuery(id+"F2.wireOp",EDGE,"E68"),sQuery(id+"F2.wireOp",EDGE,"E69"),sQuery(id+"F2.wireOp",EDGE,"E70"),sQuery(id+"F2.wireOp",EDGE,"E71"),sQuery(id+"F2.wireOp",EDGE,"E72"),sQuery(id+"F2.wireOp",EDGE,"E73"),sQuery(id+"F2.wireOp",EDGE,"E74"),sQuery(id+"F2.wireOp",EDGE,"E75"),sQuery(id+"F2.wireOp",EDGE,"E76"),sQuery(id+"F2.wireOp",EDGE,"E77"),sQuery(id+"F2.wireOp",EDGE,"E78"),sQuery(id+"F2.wireOp",EDGE,"E79"),sQuery(id+"F2.wireOp",EDGE,"E80"),sQuery(id+"F2.wireOp",EDGE,"E81"),sQuery(id+"F2.wireOp",EDGE,"E83"),sQuery(id+"F2.wireOp",EDGE,"E84"),sQuery(id+"F2.wireOp",EDGE,"E85"),sQuery(id+"F2.wireOp",EDGE,"E86"),sQuery(id+"F2.wireOp",EDGE,"E87"),sQuery(id+"F2.wireOp",EDGE,"E88"),sQuery(id+"F2.wireOp",EDGE,"E89"),sQuery(id+"F2.wireOp",EDGE,"E90"),sQuery(id+"F2.wireOp",EDGE,"E91"),sQuery(id+"F2.wireOp",EDGE,"E92"),sQuery(id+"F2.wireOp",EDGE,"E93"),sQuery(id+"F2.wireOp",EDGE,"E94"),sQuery(id+"F2.wireOp",EDGE,"E95"),sQuery(id+"F2.wireOp",EDGE,"E96"),sQuery(id+"F2.wireOp",EDGE,"E97"),sQuery(id+"F2.wireOp",EDGE,"E98"),sQuery(id+"F2.wireOp",EDGE,"E99"),sQuery(id+"F2.wireOp",EDGE,"E100"),sQuery(id+"F2.wireOp",EDGE,"E101"),sQuery(id+"F2.wireOp",EDGE,"E102"),sQuery(id+"F2.wireOp",EDGE,"E103"),sQuery(id+"F2.wireOp",EDGE,"E104"),sQuery(id+"F2.wireOp",EDGE,"E105"),sQuery(id+"F2.wireOp",EDGE,"E106"),sQuery(id+"F2.wireOp",EDGE,"E107"),sQuery(id+"F2.wireOp",EDGE,"E108"),sQuery(id+"F2.wireOp",EDGE,"E109"),sQuery(id+"F2.wireOp",EDGE,"E110"),sQuery(id+"F2.wireOp",EDGE,"E111"),sQuery(id+"F2.wireOp",EDGE,"E112"),sQuery(id+"F2.wireOp",EDGE,"E113"),sQuery(id+"F2.wireOp",EDGE,"E114"),sQuery(id+"F2.wireOp",EDGE,"E115"),sQuery(id+"F2.wireOp",EDGE,"E116"),sQuery(id+"F2.wireOp",EDGE,"E117"),sQuery(id+"F2.wireOp",EDGE,"E118"),sQuery(id+"F2.wireOp",EDGE,"E119"),sQuery(id+"F2.wireOp",EDGE,"E120"),sQuery(id+"F2.wireOp",EDGE,"E121"),sQuery(id+"F2.wireOp",EDGE,"E122"),sQuery(id+"F2.wireOp",EDGE,"E123"),sQuery(id+"F2.wireOp",EDGE,"E124"),sQuery(id+"F2.wireOp",EDGE,"E125"),sQuery(id+"F2.wireOp",EDGE,"E126"),sQuery(id+"F2.wireOp",EDGE,"E127"),sQuery(id+"F2.wireOp",EDGE,"E128"),sQuery(id+"F2.wireOp",EDGE,"E129"),sQuery(id+"F2.wireOp",EDGE,"E130"),sQuery(id+"F2.wireOp",EDGE,"E131"),sQuery(id+"F2.wireOp",EDGE,"E132"),sQuery(id+"F2.wireOp",EDGE,"E133"),sQuery(id+"F2.wireOp",EDGE,"E134"),sQuery(id+"F2.wireOp",EDGE,"E135"),sQuery(id+"F2.wireOp",EDGE,"E136"),sQuery(id+"F2.wireOp",EDGE,"E137"),sQuery(id+"F2.wireOp",EDGE,"E138"),sQuery(id+"F2.wireOp",EDGE,"E139"),sQuery(id+"F2.wireOp",EDGE,"E140"),sQuery(id+"F2.wireOp",EDGE,"E141"),sQuery(id+"F2.wireOp",EDGE,"E142"),sQuery(id+"F2.wireOp",EDGE,"E143"),sQuery(id+"F2.wireOp",EDGE,"E144"),sQuery(id+"F2.wireOp",EDGE,"E145"),sQuery(id+"F2.wireOp",EDGE,"E146"),sQuery(id+"F2.wireOp",EDGE,"E147"),sQuery(id+"F2.wireOp",EDGE,"E148"),sQuery(id+"F2.wireOp",EDGE,"E149"),sQuery(id+"F2.wireOp",EDGE,"E150"),sQuery(id+"F2.wireOp",EDGE,"E151"),sQuery(id+"F2.wireOp",EDGE,"E152"),sQuery(id+"F2.wireOp",EDGE,"E153"),sQuery(id+"F2.wireOp",EDGE,"E154"),sQuery(id+"F2.wireOp",EDGE,"E155"),sQuery(id+"F2.wireOp",EDGE,"E156"),sQuery(id+"F2.wireOp",EDGE,"E157"),sQuery(id+"F2.wireOp",EDGE,"E158"),sQuery(id+"F2.wireOp",EDGE,"E159"),sQuery(id+"F2.wireOp",EDGE,"E160"),sQuery(id+"F2.wireOp",EDGE,"E161"),sQuery(id+"F2.wireOp",EDGE,"E162"),sQuery(id+"F2.wireOp",EDGE,"E163"),sQuery(id+"F2.wireOp",EDGE,"E164"),sQuery(id+"F2.wireOp",EDGE,"E165"),sQuery(id+"F2.wireOp",EDGE,"E166"),sQuery(id+"F2.wireOp",EDGE,"E167"),sQuery(id+"F2.wireOp",EDGE,"E168"),sQuery(id+"F2.wireOp",EDGE,"E169"),sQuery(id+"F2.wireOp",EDGE,"E170"),sQuery(id+"F2.wireOp",EDGE,"E171"),sQuery(id+"F2.wireOp",EDGE,"E172"),sQuery(id+"F2.wireOp",EDGE,"E173"),sQuery(id+"F2.wireOp",EDGE,"E174"),sQuery(id+"F2.wireOp",EDGE,"E175"),sQuery(id+"F2.wireOp",EDGE,"E176"),sQuery(id+"F2.wireOp",EDGE,"E177"),sQuery(id+"F2.wireOp",EDGE,"E178"),sQuery(id+"F2.wireOp",EDGE,"E179"),sQuery(id+"F2.wireOp",EDGE,"E180"),sQuery(id+"F2.wireOp",EDGE,"E181"),sQuery(id+"F2.wireOp",EDGE,"E182"),sQuery(id+"F2.wireOp",EDGE,"E183"),sQuery(id+"F2.wireOp",EDGE,"E184"),sQuery(id+"F2.wireOp",EDGE,"E185"),sQuery(id+"F2.wireOp",EDGE,"E186"),sQuery(id+"F2.wireOp",EDGE,"E187"),sQuery(id+"F2.wireOp",EDGE,"E188"),sQuery(id+"F2.wireOp",EDGE,"E189"),sQuery(id+"F2.wireOp",EDGE,"E190"),sQuery(id+"F2.wireOp",EDGE,"E191"),sQuery(id+"F2.wireOp",EDGE,"E192"),sQuery(id+"F2.wireOp",EDGE,"E193"),sQuery(id+"F2.wireOp",EDGE,"E194"),sQuery(id+"F2.wireOp",EDGE,"E195"),sQuery(id+"F2.wireOp",EDGE,"E196"),sQuery(id+"F2.wireOp",EDGE,"E197"),sQuery(id+"F2.wireOp",EDGE,"E198"),sQuery(id+"F2.wireOp",EDGE,"E199"),sQuery(id+"F2.wireOp",EDGE,"E200"),sQuery(id+"F2.wireOp",EDGE,"E201"),sQuery(id+"F2.wireOp",EDGE,"E202"),sQuery(id+"F2.wireOp",EDGE,"E203"),sQuery(id+"F2.wireOp",EDGE,"E204"),sQuery(id+"F2.wireOp",EDGE,"E205"),sQuery(id+"F2.wireOp",EDGE,"E206"),sQuery(id+"F2.wireOp",EDGE,"E207"),sQuery(id+"F2.wireOp",EDGE,"E208"),sQuery(id+"F2.wireOp",EDGE,"E209"),sQuery(id+"F2.wireOp",EDGE,"E210"),sQuery(id+"F2.wireOp",EDGE,"E210"),sQuery(id+"F2.wireOp",EDGE,"E211"),sQuery(id+"F2.wireOp",EDGE,"E212"),sQuery(id+"F2.wireOp",EDGE,"E212"),sQuery(id+"F2.wireOp",EDGE,"E213"),sQuery(id+"F2.wireOp",EDGE,"E214"),sQuery(id+"F2.wireOp",EDGE,"E215"),sQuery(id+"F2.wireOp",EDGE,"E216"),sQuery(id+"F2.wireOp",EDGE,"E217"),sQuery(id+"F2.wireOp",EDGE,"E218"),sQuery(id+"F2.wireOp",EDGE,"E219"),sQuery(id+"F2.wireOp",EDGE,"E220"),sQuery(id+"F2.wireOp",EDGE,"E221"),sQuery(id+"F2.wireOp",EDGE,"E222"),sQuery(id+"F2.wireOp",EDGE,"E223"),sQuery(id+"F2.wireOp",EDGE,"E224"),sQuery(id+"F2.wireOp",EDGE,"E225"),sQuery(id+"F2.wireOp",EDGE,"E226"),sQuery(id+"F2.wireOp",EDGE,"E227"),sQuery(id+"F2.wireOp",EDGE,"E228"),sQuery(id+"F2.wireOp",EDGE,"E229"),sQuery(id+"F2.wireOp",EDGE,"E230"),sQuery(id+"F2.wireOp",EDGE,"E231"),sQuery(id+"F2.wireOp",EDGE,"E232"),sQuery(id+"F2.wireOp",EDGE,"E233"),sQuery(id+"F2.wireOp",EDGE,"E234"),sQuery(id+"F2.wireOp",EDGE,"E235"),sQuery(id+"F2.wireOp",EDGE,"E236"),sQuery(id+"F2.wireOp",EDGE,"E237"),sQuery(id+"F2.wireOp",EDGE,"E238"),sQuery(id+"F2.wireOp",EDGE,"E239"),sQuery(id+"F2.wireOp",EDGE,"E240"),sQuery(id+"F2.wireOp",EDGE,"E241"),sQuery(id+"F2.wireOp",EDGE,"E242"),sQuery(id+"F2.wireOp",EDGE,"E243"),sQuery(id+"F2.wireOp",EDGE,"E244"),sQuery(id+"F2.wireOp",EDGE,"E245"),sQuery(id+"F2.wireOp",EDGE,"E246"),sQuery(id+"F2.wireOp",EDGE,"E247"),sQuery(id+"F2.wireOp",EDGE,"E248"),sQuery(id+"F2.wireOp",EDGE,"E249"),sQuery(id+"F2.wireOp",EDGE,"E250"),sQuery(id+"F2.wireOp",EDGE,"E251"),sQuery(id+"F2.wireOp",EDGE,"E252"),sQuery(id+"F2.wireOp",EDGE,"E253"),sQuery(id+"F2.wireOp",EDGE,"E254"),sQuery(id+"F2.wireOp",EDGE,"E255"),sQuery(id+"F2.wireOp",EDGE,"E256"),sQuery(id+"F2.wireOp",EDGE,"E257"),sQuery(id+"F2.wireOp",EDGE,"E258"),sQuery(id+"F2.wireOp",EDGE,"E259"),sQuery(id+"F2.wireOp",EDGE,"E260"),sQuery(id+"F2.wireOp",EDGE,"E261"),sQuery(id+"F2.wireOp",EDGE,"E262"),sQuery(id+"F2.wireOp",EDGE,"E263"),sQuery(id+"F2.wireOp",EDGE,"E264"),sQuery(id+"F2.wireOp",EDGE,"E265"),sQuery(id+"F2.wireOp",EDGE,"E266"),sQuery(id+"F2.wireOp",EDGE,"E267"),sQuery(id+"F2.wireOp",EDGE,"E268"),sQuery(id+"F2.wireOp",EDGE,"E269"),sQuery(id+"F2.wireOp",EDGE,"E270"),sQuery(id+"F2.wireOp",EDGE,"E271"),sQuery(id+"F2.wireOp",EDGE,"E272"),sQuery(id+"F2.wireOp",EDGE,"E273"),sQuery(id+"F2.wireOp",EDGE,"E274"),sQuery(id+"F2.wireOp",EDGE,"E275"),sQuery(id+"F2.wireOp",EDGE,"E276"),sQuery(id+"F2.wireOp",EDGE,"E277"),sQuery(id+"F2.wireOp",EDGE,"E278"),sQuery(id+"F2.wireOp",EDGE,"E279"),sQuery(id+"F2.wireOp",EDGE,"E280"),sQuery(id+"F2.wireOp",EDGE,"E281"),sQuery(id+"F2.wireOp",EDGE,"E282"),sQuery(id+"F2.wireOp",EDGE,"E283"),sQuery(id+"F2.wireOp",EDGE,"E284"),sQuery(id+"F2.wireOp",EDGE,"E285"),sQuery(id+"F2.wireOp",EDGE,"E286"),sQuery(id+"F2.wireOp",EDGE,"E287"),sQuery(id+"F2.wireOp",EDGE,"E288"),sQuery(id+"F2.wireOp",EDGE,"E289"),sQuery(id+"F2.wireOp",EDGE,"E290"),sQuery(id+"F2.wireOp",EDGE,"E291"),sQuery(id+"F2.wireOp",EDGE,"E292"),sQuery(id+"F2.wireOp",EDGE,"E293"),sQuery(id+"F2.wireOp",EDGE,"E294"),sQuery(id+"F2.wireOp",EDGE,"E295"),sQuery(id+"F2.wireOp",EDGE,"E296"),sQuery(id+"F2.wireOp",EDGE,"E297"),sQuery(id+"F2.wireOp",EDGE,"E298"),sQuery(id+"F2.wireOp",EDGE,"E299"),sQuery(id+"F2.wireOp",EDGE,"E300"),sQuery(id+"F2.wireOp",EDGE,"E301"),sQuery(id+"F2.wireOp",EDGE,"E302"),sQuery(id+"F2.wireOp",EDGE,"E303"),sQuery(id+"F2.wireOp",EDGE,"E304"),sQuery(id+"F2.wireOp",EDGE,"E305"),sQuery(id+"F2.wireOp",EDGE,"E306"),sQuery(id+"F2.wireOp",EDGE,"E307"),sQuery(id+"F2.wireOp",EDGE,"E308"),sQuery(id+"F2.wireOp",EDGE,"E309"),sQuery(id+"F2.wireOp",EDGE,"E310"),sQuery(id+"F2.wireOp",EDGE,"E311"),sQuery(id+"F2.wireOp",EDGE,"E312"),sQuery(id+"F2.wireOp",EDGE,"E313"),sQuery(id+"F2.wireOp",EDGE,"E314"),sQuery(id+"F2.wireOp",EDGE,"E315"),sQuery(id+"F2.wireOp",EDGE,"E316"),sQuery(id+"F2.wireOp",EDGE,"E317"),sQuery(id+"F2.wireOp",EDGE,"E318"),sQuery(id+"F2.wireOp",EDGE,"E319"),sQuery(id+"F2.wireOp",EDGE,"E320"),sQuery(id+"F2.wireOp",EDGE,"E321"),sQuery(id+"F2.wireOp",EDGE,"E322"),sQuery(id+"F2.wireOp",EDGE,"E323"),sQuery(id+"F2.wireOp",EDGE,"E324"),sQuery(id+"F2.wireOp",EDGE,"E325"),sQuery(id+"F2.wireOp",EDGE,"E326"),sQuery(id+"F2.wireOp",EDGE,"E327"),sQuery(id+"F2.wireOp",EDGE,"E328"),sQuery(id+"F2.wireOp",EDGE,"E329"),sQuery(id+"F2.wireOp",EDGE,"E330"),sQuery(id+"F2.wireOp",EDGE,"E331"),sQuery(id+"F2.wireOp",EDGE,"E332"),sQuery(id+"F2.wireOp",EDGE,"E333"),sQuery(id+"F2.wireOp",EDGE,"E334"),sQuery(id+"F2.wireOp",EDGE,"E335"),sQuery(id+"F2.wireOp",EDGE,"E336"),sQuery(id+"F2.wireOp",EDGE,"E337"),sQuery(id+"F2.wireOp",EDGE,"E338"),sQuery(id+"F2.wireOp",EDGE,"E339"),sQuery(id+"F2.wireOp",EDGE,"E340"),sQuery(id+"F2.wireOp",EDGE,"E341"),sQuery(id+"F2.wireOp",EDGE,"E342"),sQuery(id+"F2.wireOp",EDGE,"E343"),sQuery(id+"F2.wireOp",EDGE,"E344"),sQuery(id+"F2.wireOp",EDGE,"E345"),sQuery(id+"F2.wireOp",EDGE,"E346"),sQuery(id+"F2.wireOp",EDGE,"E347"),sQuery(id+"F2.wireOp",EDGE,"E348"),sQuery(id+"F2.wireOp",EDGE,"E349"),sQuery(id+"F2.wireOp",EDGE,"E350"),sQuery(id+"F2.wireOp",EDGE,"E351"),sQuery(id+"F2.wireOp",EDGE,"E352"),sQuery(id+"F2.wireOp",EDGE,"E353"),sQuery(id+"F2.wireOp",EDGE,"E354"),sQuery(id+"F2.wireOp",EDGE,"E355"),sQuery(id+"F2.wireOp",EDGE,"E356"),sQuery(id+"F2.wireOp",EDGE,"E357"),sQuery(id+"F2.wireOp",EDGE,"E358"),sQuery(id+"F2.wireOp",EDGE,"E359"),sQuery(id+"F2.wireOp",EDGE,"E360"),sQuery(id+"F2.wireOp",EDGE,"E361"),sQuery(id+"F2.wireOp",EDGE,"E362"),sQuery(id+"F2.wireOp",EDGE,"E363"),sQuery(id+"F2.wireOp",EDGE,"E364"),sQuery(id+"F2.wireOp",EDGE,"E365"),sQuery(id+"F2.wireOp",EDGE,"E366"),sQuery(id+"F2.wireOp",EDGE,"E367"),sQuery(id+"F2.wireOp",EDGE,"E368"),sQuery(id+"F2.wireOp",EDGE,"E369"),sQuery(id+"F2.wireOp",EDGE,"E370"),sQuery(id+"F2.wireOp",EDGE,"E371"),sQuery(id+"F2.wireOp",EDGE,"E372"),sQuery(id+"F2.wireOp",EDGE,"E373"),sQuery(id+"F2.wireOp",EDGE,"E374"),sQuery(id+"F2.wireOp",EDGE,"E375"),sQuery(id+"F2.wireOp",EDGE,"E376"),sQuery(id+"F2.wireOp",EDGE,"E377"),sQuery(id+"F2.wireOp",EDGE,"E378"),sQuery(id+"F2.wireOp",EDGE,"E379"),sQuery(id+"F2.wireOp",EDGE,"E380"),sQuery(id+"F2.wireOp",EDGE,"E381"),sQuery(id+"F2.wireOp",EDGE,"E382"),sQuery(id+"F2.wireOp",EDGE,"E383"),sQuery(id+"F2.wireOp",EDGE,"E384"),sQuery(id+"F2.wireOp",EDGE,"E385"),sQuery(id+"F2.wireOp",EDGE,"E386"),sQuery(id+"F2.wireOp",EDGE,"E387"),sQuery(id+"F2.wireOp",EDGE,"E388"),sQuery(id+"F2.wireOp",EDGE,"E389"),sQuery(id+"F2.wireOp",EDGE,"E390"),sQuery(id+"F2.wireOp",EDGE,"E391"),sQuery(id+"F2.wireOp",EDGE,"E392"),sQuery(id+"F2.wireOp",EDGE,"E393"),sQuery(id+"F2.wireOp",EDGE,"E394"),sQuery(id+"F2.wireOp",EDGE,"E395"),sQuery(id+"F2.wireOp",EDGE,"E396"),sQuery(id+"F2.wireOp",EDGE,"E397"),sQuery(id+"F2.wireOp",EDGE,"E398"),sQuery(id+"F2.wireOp",EDGE,"E399"),sQuery(id+"F2.wireOp",EDGE,"E400"),sQuery(id+"F2.wireOp",EDGE,"E401"),sQuery(id+"F2.wireOp",EDGE,"E402"),sQuery(id+"F2.wireOp",EDGE,"E403"),sQuery(id+"F2.wireOp",EDGE,"E404"),sQuery(id+"F2.wireOp",EDGE,"E500")])]});
            var Q1;
            Q1=makeQuery(id+"F3.opExtrude","SWEPT_BODY",BODY,{"disambiguationData":[OSD([sQuery(id+"F2.wireOp",EDGE,"E547"),sQuery(id+"F2.wireOp",EDGE,"E548"),sQuery(id+"F2.wireOp",EDGE,"E549"),sQuery(id+"F2.wireOp",EDGE,"E550"),sQuery(id+"F2.wireOp",EDGE,"E551"),sQuery(id+"F2.wireOp",EDGE,"E552"),sQuery(id+"F2.wireOp",EDGE,"E553"),sQuery(id+"F2.wireOp",EDGE,"E554"),sQuery(id+"F2.wireOp",EDGE,"E555"),sQuery(id+"F2.wireOp",EDGE,"E556"),sQuery(id+"F2.wireOp",EDGE,"E557"),sQuery(id+"F2.wireOp",EDGE,"E558"),sQuery(id+"F2.wireOp",EDGE,"E559"),sQuery(id+"F2.wireOp",EDGE,"E560"),sQuery(id+"F2.wireOp",EDGE,"E561"),sQuery(id+"F2.wireOp",EDGE,"E562"),sQuery(id+"F2.wireOp",EDGE,"E563"),sQuery(id+"F2.wireOp",EDGE,"E564"),sQuery(id+"F2.wireOp",EDGE,"E565"),sQuery(id+"F2.wireOp",EDGE,"E566"),sQuery(id+"F2.wireOp",EDGE,"E567"),sQuery(id+"F2.wireOp",EDGE,"E568"),sQuery(id+"F2.wireOp",EDGE,"E569"),sQuery(id+"F2.wireOp",EDGE,"E570"),sQuery(id+"F2.wireOp",EDGE,"E571"),sQuery(id+"F2.wireOp",EDGE,"E572"),sQuery(id+"F2.wireOp",EDGE,"E573"),sQuery(id+"F2.wireOp",EDGE,"E574"),sQuery(id+"F2.wireOp",EDGE,"E575"),sQuery(id+"F2.wireOp",EDGE,"E576"),sQuery(id+"F2.wireOp",EDGE,"E577"),sQuery(id+"F2.wireOp",EDGE,"E578"),sQuery(id+"F2.wireOp",EDGE,"E579"),sQuery(id+"F2.wireOp",EDGE,"E580"),sQuery(id+"F2.wireOp",EDGE,"E581"),sQuery(id+"F2.wireOp",EDGE,"E582"),sQuery(id+"F2.wireOp",EDGE,"E583"),sQuery(id+"F2.wireOp",EDGE,"E584"),sQuery(id+"F2.wireOp",EDGE,"E585"),sQuery(id+"F2.wireOp",EDGE,"E586"),sQuery(id+"F2.wireOp",EDGE,"E587"),sQuery(id+"F2.wireOp",EDGE,"E588"),sQuery(id+"F2.wireOp",EDGE,"E589"),sQuery(id+"F2.wireOp",EDGE,"E589"),sQuery(id+"F2.wireOp",EDGE,"E590"),sQuery(id+"F2.wireOp",EDGE,"E591")])]});
            var Q2;
            Q2=makeQuery(id+"F3.opExtrude","SWEPT_BODY",BODY,{"disambiguationData":[OSD([sQuery(id+"F2.wireOp",EDGE,"E451"),sQuery(id+"F2.wireOp",EDGE,"E452"),sQuery(id+"F2.wireOp",EDGE,"E453"),sQuery(id+"F2.wireOp",EDGE,"E454"),sQuery(id+"F2.wireOp",EDGE,"E455"),sQuery(id+"F2.wireOp",EDGE,"E456"),sQuery(id+"F2.wireOp",EDGE,"E457"),sQuery(id+"F2.wireOp",EDGE,"E458"),sQuery(id+"F2.wireOp",EDGE,"E459"),sQuery(id+"F2.wireOp",EDGE,"E460"),sQuery(id+"F2.wireOp",EDGE,"E461"),sQuery(id+"F2.wireOp",EDGE,"E462"),sQuery(id+"F2.wireOp",EDGE,"E463"),sQuery(id+"F2.wireOp",EDGE,"E464"),sQuery(id+"F2.wireOp",EDGE,"E465"),sQuery(id+"F2.wireOp",EDGE,"E466"),sQuery(id+"F2.wireOp",EDGE,"E467"),sQuery(id+"F2.wireOp",EDGE,"E468"),sQuery(id+"F2.wireOp",EDGE,"E469"),sQuery(id+"F2.wireOp",EDGE,"E470"),sQuery(id+"F2.wireOp",EDGE,"E471"),sQuery(id+"F2.wireOp",EDGE,"E472"),sQuery(id+"F2.wireOp",EDGE,"E473"),sQuery(id+"F2.wireOp",EDGE,"E474"),sQuery(id+"F2.wireOp",EDGE,"E475"),sQuery(id+"F2.wireOp",EDGE,"E476"),sQuery(id+"F2.wireOp",EDGE,"E477"),sQuery(id+"F2.wireOp",EDGE,"E478"),sQuery(id+"F2.wireOp",EDGE,"E479"),sQuery(id+"F2.wireOp",EDGE,"E480"),sQuery(id+"F2.wireOp",EDGE,"E481"),sQuery(id+"F2.wireOp",EDGE,"E482"),sQuery(id+"F2.wireOp",EDGE,"E483"),sQuery(id+"F2.wireOp",EDGE,"E484"),sQuery(id+"F2.wireOp",EDGE,"E485"),sQuery(id+"F2.wireOp",EDGE,"E486"),sQuery(id+"F2.wireOp",EDGE,"E487"),sQuery(id+"F2.wireOp",EDGE,"E488"),sQuery(id+"F2.wireOp",EDGE,"E489"),sQuery(id+"F2.wireOp",EDGE,"E490"),sQuery(id+"F2.wireOp",EDGE,"E491"),sQuery(id+"F2.wireOp",EDGE,"E492"),sQuery(id+"F2.wireOp",EDGE,"E493"),sQuery(id+"F2.wireOp",EDGE,"E493"),sQuery(id+"F2.wireOp",EDGE,"E494"),sQuery(id+"F2.wireOp",EDGE,"E495")])]});
            var Q3;
            Q3=makeQuery(id+"F3.opExtrude","SWEPT_BODY",BODY,{"disambiguationData":[OSD([sQuery(id+"F2.wireOp",EDGE,"E501"),sQuery(id+"F2.wireOp",EDGE,"E502"),sQuery(id+"F2.wireOp",EDGE,"E503"),sQuery(id+"F2.wireOp",EDGE,"E504"),sQuery(id+"F2.wireOp",EDGE,"E505"),sQuery(id+"F2.wireOp",EDGE,"E506"),sQuery(id+"F2.wireOp",EDGE,"E507"),sQuery(id+"F2.wireOp",EDGE,"E508"),sQuery(id+"F2.wireOp",EDGE,"E509"),sQuery(id+"F2.wireOp",EDGE,"E510"),sQuery(id+"F2.wireOp",EDGE,"E511"),sQuery(id+"F2.wireOp",EDGE,"E512"),sQuery(id+"F2.wireOp",EDGE,"E513"),sQuery(id+"F2.wireOp",EDGE,"E514"),sQuery(id+"F2.wireOp",EDGE,"E515"),sQuery(id+"F2.wireOp",EDGE,"E516"),sQuery(id+"F2.wireOp",EDGE,"E517"),sQuery(id+"F2.wireOp",EDGE,"E518"),sQuery(id+"F2.wireOp",EDGE,"E519"),sQuery(id+"F2.wireOp",EDGE,"E520"),sQuery(id+"F2.wireOp",EDGE,"E521"),sQuery(id+"F2.wireOp",EDGE,"E522"),sQuery(id+"F2.wireOp",EDGE,"E523"),sQuery(id+"F2.wireOp",EDGE,"E524"),sQuery(id+"F2.wireOp",EDGE,"E525"),sQuery(id+"F2.wireOp",EDGE,"E526"),sQuery(id+"F2.wireOp",EDGE,"E527"),sQuery(id+"F2.wireOp",EDGE,"E528"),sQuery(id+"F2.wireOp",EDGE,"E529"),sQuery(id+"F2.wireOp",EDGE,"E530"),sQuery(id+"F2.wireOp",EDGE,"E531"),sQuery(id+"F2.wireOp",EDGE,"E532"),sQuery(id+"F2.wireOp",EDGE,"E533"),sQuery(id+"F2.wireOp",EDGE,"E534"),sQuery(id+"F2.wireOp",EDGE,"E535"),sQuery(id+"F2.wireOp",EDGE,"E536"),sQuery(id+"F2.wireOp",EDGE,"E537"),sQuery(id+"F2.wireOp",EDGE,"E538"),sQuery(id+"F2.wireOp",EDGE,"E539"),sQuery(id+"F2.wireOp",EDGE,"E540"),sQuery(id+"F2.wireOp",EDGE,"E541"),sQuery(id+"F2.wireOp",EDGE,"E542"),sQuery(id+"F2.wireOp",EDGE,"E543"),sQuery(id+"F2.wireOp",EDGE,"E544"),sQuery(id+"F2.wireOp",EDGE,"E545"),sQuery(id+"F2.wireOp",EDGE,"E546")])]});
            var Q4;
            Q4=makeQuery(id+"F3.opExtrude","SWEPT_BODY",BODY,{"disambiguationData":[OSD([sQuery(id+"F2.wireOp",EDGE,"E405"),sQuery(id+"F2.wireOp",EDGE,"E406"),sQuery(id+"F2.wireOp",EDGE,"E407"),sQuery(id+"F2.wireOp",EDGE,"E408"),sQuery(id+"F2.wireOp",EDGE,"E409"),sQuery(id+"F2.wireOp",EDGE,"E410"),sQuery(id+"F2.wireOp",EDGE,"E411"),sQuery(id+"F2.wireOp",EDGE,"E412"),sQuery(id+"F2.wireOp",EDGE,"E413"),sQuery(id+"F2.wireOp",EDGE,"E414"),sQuery(id+"F2.wireOp",EDGE,"E415"),sQuery(id+"F2.wireOp",EDGE,"E416"),sQuery(id+"F2.wireOp",EDGE,"E417"),sQuery(id+"F2.wireOp",EDGE,"E418"),sQuery(id+"F2.wireOp",EDGE,"E419"),sQuery(id+"F2.wireOp",EDGE,"E420"),sQuery(id+"F2.wireOp",EDGE,"E421"),sQuery(id+"F2.wireOp",EDGE,"E422"),sQuery(id+"F2.wireOp",EDGE,"E423"),sQuery(id+"F2.wireOp",EDGE,"E424"),sQuery(id+"F2.wireOp",EDGE,"E425"),sQuery(id+"F2.wireOp",EDGE,"E426"),sQuery(id+"F2.wireOp",EDGE,"E427"),sQuery(id+"F2.wireOp",EDGE,"E428"),sQuery(id+"F2.wireOp",EDGE,"E429"),sQuery(id+"F2.wireOp",EDGE,"E430"),sQuery(id+"F2.wireOp",EDGE,"E431"),sQuery(id+"F2.wireOp",EDGE,"E432"),sQuery(id+"F2.wireOp",EDGE,"E433"),sQuery(id+"F2.wireOp",EDGE,"E434"),sQuery(id+"F2.wireOp",EDGE,"E435"),sQuery(id+"F2.wireOp",EDGE,"E436"),sQuery(id+"F2.wireOp",EDGE,"E437"),sQuery(id+"F2.wireOp",EDGE,"E438"),sQuery(id+"F2.wireOp",EDGE,"E439"),sQuery(id+"F2.wireOp",EDGE,"E440"),sQuery(id+"F2.wireOp",EDGE,"E441"),sQuery(id+"F2.wireOp",EDGE,"E442"),sQuery(id+"F2.wireOp",EDGE,"E443"),sQuery(id+"F2.wireOp",EDGE,"E444"),sQuery(id+"F2.wireOp",EDGE,"E445"),sQuery(id+"F2.wireOp",EDGE,"E446"),sQuery(id+"F2.wireOp",EDGE,"E447"),sQuery(id+"F2.wireOp",EDGE,"E448"),sQuery(id+"F2.wireOp",EDGE,"E449"),sQuery(id+"F2.wireOp",EDGE,"E450")])]});
            transform(context, id + "F5", {"entities" : qUnion([Q0, Q1, Q2, Q3, Q4]), "transformType" : TransformType.TRANSLATION_3D, "dx" : 4.5 * mm, "dy" : 0 * mm, "dz" : 10 * mm, "makeCopy" : false});
        }
        {
            var Q0;
            {var subQ0=sQuery(id+"F0.wireOp",EDGE,"E3");Q0=makeQuery(id+"F0.imprint","IMPRINT",FACE,{"disambiguationData":[TD([[makeQuery(id+"F0.imprint","IMPRINT",EDGE,{"derivedFrom":subQ0}),1.0]])]});}
            var Q1;
            Q1=sQuery(id+"F0.wireOp",EDGE,"E4");
            revolve(context, id + "F6", {"entities" : qUnion([Q0]), "axis" : qUnion([Q1]), "revolveType" : RevolveType.ONE_DIRECTION, "angle" : 180 * degree});
        }
        {
            var Q0;
            Q0=makeQuery(id+"F6.opRevolve","CAP_FACE",FACE,{"disambiguationData":[OSD([sQuery(id+"F0.wireOp",EDGE,"E0.bottom"),sQuery(id+"F0.wireOp",EDGE,"E3"),sQuery(id+"F0.wireOp",EDGE,"E4")])],"isStart":false});
            extrude(context, id + "F7", {"entities" : qUnion([Q0]), "operationType" : NewBodyOperationType.ADD, "depth" : 1.5 * mm});
        }
        {
            var Q0;
            Q0=makeQuery(id+"F7.opExtrude","CAP_FACE",FACE,{"disambiguationData":[OSD([sQuery(id+"F0.wireOp",EDGE,"E0.bottom"),sQuery(id+"F0.wireOp",EDGE,"E3"),sQuery(id+"F0.wireOp",EDGE,"E4")])],"isStart":false});
            var Q1;
            {var subQ0=sQuery(id+"F0.wireOp",EDGE,"E0.bottom");Q1=makeQuery(id+"F7.boolean.opBoolean","MERGE",FACE,{"derivedFrom":[makeQuery(id+"F6.opRevolve","SWEPT_FACE",FACE,{"disambiguationData":[OSD([subQ0])]}),makeQuery(id+"F7.opExtrude","SWEPT_FACE",FACE,{"disambiguationData":[OSD([subQ0])]})]});}
            shell(context, id + "F8", {"entities" : qUnion([Q0, Q1]), "thickness" : 1.3 * mm});
        }
        {
            var Q0;
            Q0=makeQuery(id+"F1.opExtrude","SWEPT_BODY",BODY,{"disambiguationData":[OSD([sQuery(id+"F0.wireOp",EDGE,"E0.top"),sQuery(id+"F0.wireOp",EDGE,"E0.left"),sQuery(id+"F0.wireOp",EDGE,"E0.right"),sQuery(id+"F0.wireOp",EDGE,"E0.bottom"),sQuery(id+"F0.wireOp",EDGE,"E1.left"),sQuery(id+"F0.wireOp",EDGE,"E1.right"),sQuery(id+"F0.wireOp",EDGE,"E3"),sQuery(id+"F0.wireOp",EDGE,"E5.MirrorCS")])]});
            var Q1;
            Q1=makeQuery(id+"F6.opRevolve","SWEPT_BODY",BODY,{"disambiguationData":[OSD([sQuery(id+"F0.wireOp",EDGE,"E0.bottom"),sQuery(id+"F0.wireOp",EDGE,"E3"),sQuery(id+"F0.wireOp",EDGE,"E4")])]});
            var Q2;
            Q2=makeQuery(id+"F3.opExtrude","SWEPT_BODY",BODY,{"disambiguationData":[OSD([sQuery(id+"F2.wireOp",EDGE,"E547"),sQuery(id+"F2.wireOp",EDGE,"E548"),sQuery(id+"F2.wireOp",EDGE,"E549"),sQuery(id+"F2.wireOp",EDGE,"E550"),sQuery(id+"F2.wireOp",EDGE,"E551"),sQuery(id+"F2.wireOp",EDGE,"E552"),sQuery(id+"F2.wireOp",EDGE,"E553"),sQuery(id+"F2.wireOp",EDGE,"E554"),sQuery(id+"F2.wireOp",EDGE,"E555"),sQuery(id+"F2.wireOp",EDGE,"E556"),sQuery(id+"F2.wireOp",EDGE,"E557"),sQuery(id+"F2.wireOp",EDGE,"E558"),sQuery(id+"F2.wireOp",EDGE,"E559"),sQuery(id+"F2.wireOp",EDGE,"E560"),sQuery(id+"F2.wireOp",EDGE,"E561"),sQuery(id+"F2.wireOp",EDGE,"E562"),sQuery(id+"F2.wireOp",EDGE,"E563"),sQuery(id+"F2.wireOp",EDGE,"E564"),sQuery(id+"F2.wireOp",EDGE,"E565"),sQuery(id+"F2.wireOp",EDGE,"E566"),sQuery(id+"F2.wireOp",EDGE,"E567"),sQuery(id+"F2.wireOp",EDGE,"E568"),sQuery(id+"F2.wireOp",EDGE,"E569"),sQuery(id+"F2.wireOp",EDGE,"E570"),sQuery(id+"F2.wireOp",EDGE,"E571"),sQuery(id+"F2.wireOp",EDGE,"E572"),sQuery(id+"F2.wireOp",EDGE,"E573"),sQuery(id+"F2.wireOp",EDGE,"E574"),sQuery(id+"F2.wireOp",EDGE,"E575"),sQuery(id+"F2.wireOp",EDGE,"E576"),sQuery(id+"F2.wireOp",EDGE,"E577"),sQuery(id+"F2.wireOp",EDGE,"E578"),sQuery(id+"F2.wireOp",EDGE,"E579"),sQuery(id+"F2.wireOp",EDGE,"E580"),sQuery(id+"F2.wireOp",EDGE,"E581"),sQuery(id+"F2.wireOp",EDGE,"E582"),sQuery(id+"F2.wireOp",EDGE,"E583"),sQuery(id+"F2.wireOp",EDGE,"E584"),sQuery(id+"F2.wireOp",EDGE,"E585"),sQuery(id+"F2.wireOp",EDGE,"E586"),sQuery(id+"F2.wireOp",EDGE,"E587"),sQuery(id+"F2.wireOp",EDGE,"E588"),sQuery(id+"F2.wireOp",EDGE,"E589"),sQuery(id+"F2.wireOp",EDGE,"E589"),sQuery(id+"F2.wireOp",EDGE,"E590"),sQuery(id+"F2.wireOp",EDGE,"E591")])]});
            var Q3;
            Q3=makeQuery(id+"F3.opExtrude","SWEPT_BODY",BODY,{"disambiguationData":[OSD([sQuery(id+"F2.wireOp",EDGE,"E451"),sQuery(id+"F2.wireOp",EDGE,"E452"),sQuery(id+"F2.wireOp",EDGE,"E453"),sQuery(id+"F2.wireOp",EDGE,"E454"),sQuery(id+"F2.wireOp",EDGE,"E455"),sQuery(id+"F2.wireOp",EDGE,"E456"),sQuery(id+"F2.wireOp",EDGE,"E457"),sQuery(id+"F2.wireOp",EDGE,"E458"),sQuery(id+"F2.wireOp",EDGE,"E459"),sQuery(id+"F2.wireOp",EDGE,"E460"),sQuery(id+"F2.wireOp",EDGE,"E461"),sQuery(id+"F2.wireOp",EDGE,"E462"),sQuery(id+"F2.wireOp",EDGE,"E463"),sQuery(id+"F2.wireOp",EDGE,"E464"),sQuery(id+"F2.wireOp",EDGE,"E465"),sQuery(id+"F2.wireOp",EDGE,"E466"),sQuery(id+"F2.wireOp",EDGE,"E467"),sQuery(id+"F2.wireOp",EDGE,"E468"),sQuery(id+"F2.wireOp",EDGE,"E469"),sQuery(id+"F2.wireOp",EDGE,"E470"),sQuery(id+"F2.wireOp",EDGE,"E471"),sQuery(id+"F2.wireOp",EDGE,"E472"),sQuery(id+"F2.wireOp",EDGE,"E473"),sQuery(id+"F2.wireOp",EDGE,"E474"),sQuery(id+"F2.wireOp",EDGE,"E475"),sQuery(id+"F2.wireOp",EDGE,"E476"),sQuery(id+"F2.wireOp",EDGE,"E477"),sQuery(id+"F2.wireOp",EDGE,"E478"),sQuery(id+"F2.wireOp",EDGE,"E479"),sQuery(id+"F2.wireOp",EDGE,"E480"),sQuery(id+"F2.wireOp",EDGE,"E481"),sQuery(id+"F2.wireOp",EDGE,"E482"),sQuery(id+"F2.wireOp",EDGE,"E483"),sQuery(id+"F2.wireOp",EDGE,"E484"),sQuery(id+"F2.wireOp",EDGE,"E485"),sQuery(id+"F2.wireOp",EDGE,"E486"),sQuery(id+"F2.wireOp",EDGE,"E487"),sQuery(id+"F2.wireOp",EDGE,"E488"),sQuery(id+"F2.wireOp",EDGE,"E489"),sQuery(id+"F2.wireOp",EDGE,"E490"),sQuery(id+"F2.wireOp",EDGE,"E491"),sQuery(id+"F2.wireOp",EDGE,"E492"),sQuery(id+"F2.wireOp",EDGE,"E493"),sQuery(id+"F2.wireOp",EDGE,"E493"),sQuery(id+"F2.wireOp",EDGE,"E494"),sQuery(id+"F2.wireOp",EDGE,"E495")])]});
            var Q4;
            Q4=makeQuery(id+"F3.opExtrude","SWEPT_BODY",BODY,{"disambiguationData":[OSD([sQuery(id+"F2.wireOp",EDGE,"E501"),sQuery(id+"F2.wireOp",EDGE,"E502"),sQuery(id+"F2.wireOp",EDGE,"E503"),sQuery(id+"F2.wireOp",EDGE,"E504"),sQuery(id+"F2.wireOp",EDGE,"E505"),sQuery(id+"F2.wireOp",EDGE,"E506"),sQuery(id+"F2.wireOp",EDGE,"E507"),sQuery(id+"F2.wireOp",EDGE,"E508"),sQuery(id+"F2.wireOp",EDGE,"E509"),sQuery(id+"F2.wireOp",EDGE,"E510"),sQuery(id+"F2.wireOp",EDGE,"E511"),sQuery(id+"F2.wireOp",EDGE,"E512"),sQuery(id+"F2.wireOp",EDGE,"E513"),sQuery(id+"F2.wireOp",EDGE,"E514"),sQuery(id+"F2.wireOp",EDGE,"E515"),sQuery(id+"F2.wireOp",EDGE,"E516"),sQuery(id+"F2.wireOp",EDGE,"E517"),sQuery(id+"F2.wireOp",EDGE,"E518"),sQuery(id+"F2.wireOp",EDGE,"E519"),sQuery(id+"F2.wireOp",EDGE,"E520"),sQuery(id+"F2.wireOp",EDGE,"E521"),sQuery(id+"F2.wireOp",EDGE,"E522"),sQuery(id+"F2.wireOp",EDGE,"E523"),sQuery(id+"F2.wireOp",EDGE,"E524"),sQuery(id+"F2.wireOp",EDGE,"E525"),sQuery(id+"F2.wireOp",EDGE,"E526"),sQuery(id+"F2.wireOp",EDGE,"E527"),sQuery(id+"F2.wireOp",EDGE,"E528"),sQuery(id+"F2.wireOp",EDGE,"E529"),sQuery(id+"F2.wireOp",EDGE,"E530"),sQuery(id+"F2.wireOp",EDGE,"E531"),sQuery(id+"F2.wireOp",EDGE,"E532"),sQuery(id+"F2.wireOp",EDGE,"E533"),sQuery(id+"F2.wireOp",EDGE,"E534"),sQuery(id+"F2.wireOp",EDGE,"E535"),sQuery(id+"F2.wireOp",EDGE,"E536"),sQuery(id+"F2.wireOp",EDGE,"E537"),sQuery(id+"F2.wireOp",EDGE,"E538"),sQuery(id+"F2.wireOp",EDGE,"E539"),sQuery(id+"F2.wireOp",EDGE,"E540"),sQuery(id+"F2.wireOp",EDGE,"E541"),sQuery(id+"F2.wireOp",EDGE,"E542"),sQuery(id+"F2.wireOp",EDGE,"E543"),sQuery(id+"F2.wireOp",EDGE,"E544"),sQuery(id+"F2.wireOp",EDGE,"E545"),sQuery(id+"F2.wireOp",EDGE,"E546")])]});
            var Q5;
            Q5=makeQuery(id+"F3.opExtrude","SWEPT_BODY",BODY,{"disambiguationData":[OSD([sQuery(id+"F2.wireOp",EDGE,"E405"),sQuery(id+"F2.wireOp",EDGE,"E406"),sQuery(id+"F2.wireOp",EDGE,"E407"),sQuery(id+"F2.wireOp",EDGE,"E408"),sQuery(id+"F2.wireOp",EDGE,"E409"),sQuery(id+"F2.wireOp",EDGE,"E410"),sQuery(id+"F2.wireOp",EDGE,"E411"),sQuery(id+"F2.wireOp",EDGE,"E412"),sQuery(id+"F2.wireOp",EDGE,"E413"),sQuery(id+"F2.wireOp",EDGE,"E414"),sQuery(id+"F2.wireOp",EDGE,"E415"),sQuery(id+"F2.wireOp",EDGE,"E416"),sQuery(id+"F2.wireOp",EDGE,"E417"),sQuery(id+"F2.wireOp",EDGE,"E418"),sQuery(id+"F2.wireOp",EDGE,"E419"),sQuery(id+"F2.wireOp",EDGE,"E420"),sQuery(id+"F2.wireOp",EDGE,"E421"),sQuery(id+"F2.wireOp",EDGE,"E422"),sQuery(id+"F2.wireOp",EDGE,"E423"),sQuery(id+"F2.wireOp",EDGE,"E424"),sQuery(id+"F2.wireOp",EDGE,"E425"),sQuery(id+"F2.wireOp",EDGE,"E426"),sQuery(id+"F2.wireOp",EDGE,"E427"),sQuery(id+"F2.wireOp",EDGE,"E428"),sQuery(id+"F2.wireOp",EDGE,"E429"),sQuery(id+"F2.wireOp",EDGE,"E430"),sQuery(id+"F2.wireOp",EDGE,"E431"),sQuery(id+"F2.wireOp",EDGE,"E432"),sQuery(id+"F2.wireOp",EDGE,"E433"),sQuery(id+"F2.wireOp",EDGE,"E434"),sQuery(id+"F2.wireOp",EDGE,"E435"),sQuery(id+"F2.wireOp",EDGE,"E436"),sQuery(id+"F2.wireOp",EDGE,"E437"),sQuery(id+"F2.wireOp",EDGE,"E438"),sQuery(id+"F2.wireOp",EDGE,"E439"),sQuery(id+"F2.wireOp",EDGE,"E440"),sQuery(id+"F2.wireOp",EDGE,"E441"),sQuery(id+"F2.wireOp",EDGE,"E442"),sQuery(id+"F2.wireOp",EDGE,"E443"),sQuery(id+"F2.wireOp",EDGE,"E444"),sQuery(id+"F2.wireOp",EDGE,"E445"),sQuery(id+"F2.wireOp",EDGE,"E446"),sQuery(id+"F2.wireOp",EDGE,"E447"),sQuery(id+"F2.wireOp",EDGE,"E448"),sQuery(id+"F2.wireOp",EDGE,"E449"),sQuery(id+"F2.wireOp",EDGE,"E450")])]});
            var Q6;
            Q6=makeQuery(id+"F3.opExtrude","SWEPT_BODY",BODY,{"disambiguationData":[OSD([sQuery(id+"F2.wireOp",EDGE,"E6"),sQuery(id+"F2.wireOp",EDGE,"E7"),sQuery(id+"F2.wireOp",EDGE,"E8"),sQuery(id+"F2.wireOp",EDGE,"E9"),sQuery(id+"F2.wireOp",EDGE,"E10"),sQuery(id+"F2.wireOp",EDGE,"E11"),sQuery(id+"F2.wireOp",EDGE,"E12"),sQuery(id+"F2.wireOp",EDGE,"E13"),sQuery(id+"F2.wireOp",EDGE,"E15"),sQuery(id+"F2.wireOp",EDGE,"E16"),sQuery(id+"F2.wireOp",EDGE,"E17"),sQuery(id+"F2.wireOp",EDGE,"E18"),sQuery(id+"F2.wireOp",EDGE,"E19"),sQuery(id+"F2.wireOp",EDGE,"E20"),sQuery(id+"F2.wireOp",EDGE,"E21"),sQuery(id+"F2.wireOp",EDGE,"E22"),sQuery(id+"F2.wireOp",EDGE,"E23"),sQuery(id+"F2.wireOp",EDGE,"E24"),sQuery(id+"F2.wireOp",EDGE,"E25"),sQuery(id+"F2.wireOp",EDGE,"E26"),sQuery(id+"F2.wireOp",EDGE,"E27"),sQuery(id+"F2.wireOp",EDGE,"E28"),sQuery(id+"F2.wireOp",EDGE,"E29"),sQuery(id+"F2.wireOp",EDGE,"E30"),sQuery(id+"F2.wireOp",EDGE,"E31"),sQuery(id+"F2.wireOp",EDGE,"E32"),sQuery(id+"F2.wireOp",EDGE,"E33"),sQuery(id+"F2.wireOp",EDGE,"E34"),sQuery(id+"F2.wireOp",EDGE,"E35"),sQuery(id+"F2.wireOp",EDGE,"E36"),sQuery(id+"F2.wireOp",EDGE,"E37"),sQuery(id+"F2.wireOp",EDGE,"E38"),sQuery(id+"F2.wireOp",EDGE,"E39"),sQuery(id+"F2.wireOp",EDGE,"E40"),sQuery(id+"F2.wireOp",EDGE,"E41"),sQuery(id+"F2.wireOp",EDGE,"E42"),sQuery(id+"F2.wireOp",EDGE,"E43"),sQuery(id+"F2.wireOp",EDGE,"E44"),sQuery(id+"F2.wireOp",EDGE,"E45"),sQuery(id+"F2.wireOp",EDGE,"E46"),sQuery(id+"F2.wireOp",EDGE,"E47"),sQuery(id+"F2.wireOp",EDGE,"E48"),sQuery(id+"F2.wireOp",EDGE,"E49"),sQuery(id+"F2.wireOp",EDGE,"E50"),sQuery(id+"F2.wireOp",EDGE,"E51"),sQuery(id+"F2.wireOp",EDGE,"E52"),sQuery(id+"F2.wireOp",EDGE,"E53"),sQuery(id+"F2.wireOp",EDGE,"E54"),sQuery(id+"F2.wireOp",EDGE,"E55"),sQuery(id+"F2.wireOp",EDGE,"E56"),sQuery(id+"F2.wireOp",EDGE,"E57"),sQuery(id+"F2.wireOp",EDGE,"E58"),sQuery(id+"F2.wireOp",EDGE,"E59"),sQuery(id+"F2.wireOp",EDGE,"E60"),sQuery(id+"F2.wireOp",EDGE,"E61"),sQuery(id+"F2.wireOp",EDGE,"E62"),sQuery(id+"F2.wireOp",EDGE,"E63"),sQuery(id+"F2.wireOp",EDGE,"E64"),sQuery(id+"F2.wireOp",EDGE,"E65"),sQuery(id+"F2.wireOp",EDGE,"E66"),sQuery(id+"F2.wireOp",EDGE,"E67"),sQuery(id+"F2.wireOp",EDGE,"E68"),sQuery(id+"F2.wireOp",EDGE,"E69"),sQuery(id+"F2.wireOp",EDGE,"E70"),sQuery(id+"F2.wireOp",EDGE,"E71"),sQuery(id+"F2.wireOp",EDGE,"E72"),sQuery(id+"F2.wireOp",EDGE,"E73"),sQuery(id+"F2.wireOp",EDGE,"E74"),sQuery(id+"F2.wireOp",EDGE,"E75"),sQuery(id+"F2.wireOp",EDGE,"E76"),sQuery(id+"F2.wireOp",EDGE,"E77"),sQuery(id+"F2.wireOp",EDGE,"E78"),sQuery(id+"F2.wireOp",EDGE,"E79"),sQuery(id+"F2.wireOp",EDGE,"E80"),sQuery(id+"F2.wireOp",EDGE,"E81"),sQuery(id+"F2.wireOp",EDGE,"E83"),sQuery(id+"F2.wireOp",EDGE,"E84"),sQuery(id+"F2.wireOp",EDGE,"E85"),sQuery(id+"F2.wireOp",EDGE,"E86"),sQuery(id+"F2.wireOp",EDGE,"E87"),sQuery(id+"F2.wireOp",EDGE,"E88"),sQuery(id+"F2.wireOp",EDGE,"E89"),sQuery(id+"F2.wireOp",EDGE,"E90"),sQuery(id+"F2.wireOp",EDGE,"E91"),sQuery(id+"F2.wireOp",EDGE,"E92"),sQuery(id+"F2.wireOp",EDGE,"E93"),sQuery(id+"F2.wireOp",EDGE,"E94"),sQuery(id+"F2.wireOp",EDGE,"E95"),sQuery(id+"F2.wireOp",EDGE,"E96"),sQuery(id+"F2.wireOp",EDGE,"E97"),sQuery(id+"F2.wireOp",EDGE,"E98"),sQuery(id+"F2.wireOp",EDGE,"E99"),sQuery(id+"F2.wireOp",EDGE,"E100"),sQuery(id+"F2.wireOp",EDGE,"E101"),sQuery(id+"F2.wireOp",EDGE,"E102"),sQuery(id+"F2.wireOp",EDGE,"E103"),sQuery(id+"F2.wireOp",EDGE,"E104"),sQuery(id+"F2.wireOp",EDGE,"E105"),sQuery(id+"F2.wireOp",EDGE,"E106"),sQuery(id+"F2.wireOp",EDGE,"E107"),sQuery(id+"F2.wireOp",EDGE,"E108"),sQuery(id+"F2.wireOp",EDGE,"E109"),sQuery(id+"F2.wireOp",EDGE,"E110"),sQuery(id+"F2.wireOp",EDGE,"E111"),sQuery(id+"F2.wireOp",EDGE,"E112"),sQuery(id+"F2.wireOp",EDGE,"E113"),sQuery(id+"F2.wireOp",EDGE,"E114"),sQuery(id+"F2.wireOp",EDGE,"E115"),sQuery(id+"F2.wireOp",EDGE,"E116"),sQuery(id+"F2.wireOp",EDGE,"E117"),sQuery(id+"F2.wireOp",EDGE,"E118"),sQuery(id+"F2.wireOp",EDGE,"E119"),sQuery(id+"F2.wireOp",EDGE,"E120"),sQuery(id+"F2.wireOp",EDGE,"E121"),sQuery(id+"F2.wireOp",EDGE,"E122"),sQuery(id+"F2.wireOp",EDGE,"E123"),sQuery(id+"F2.wireOp",EDGE,"E124"),sQuery(id+"F2.wireOp",EDGE,"E125"),sQuery(id+"F2.wireOp",EDGE,"E126"),sQuery(id+"F2.wireOp",EDGE,"E127"),sQuery(id+"F2.wireOp",EDGE,"E128"),sQuery(id+"F2.wireOp",EDGE,"E129"),sQuery(id+"F2.wireOp",EDGE,"E130"),sQuery(id+"F2.wireOp",EDGE,"E131"),sQuery(id+"F2.wireOp",EDGE,"E132"),sQuery(id+"F2.wireOp",EDGE,"E133"),sQuery(id+"F2.wireOp",EDGE,"E134"),sQuery(id+"F2.wireOp",EDGE,"E135"),sQuery(id+"F2.wireOp",EDGE,"E136"),sQuery(id+"F2.wireOp",EDGE,"E137"),sQuery(id+"F2.wireOp",EDGE,"E138"),sQuery(id+"F2.wireOp",EDGE,"E139"),sQuery(id+"F2.wireOp",EDGE,"E140"),sQuery(id+"F2.wireOp",EDGE,"E141"),sQuery(id+"F2.wireOp",EDGE,"E142"),sQuery(id+"F2.wireOp",EDGE,"E143"),sQuery(id+"F2.wireOp",EDGE,"E144"),sQuery(id+"F2.wireOp",EDGE,"E145"),sQuery(id+"F2.wireOp",EDGE,"E146"),sQuery(id+"F2.wireOp",EDGE,"E147"),sQuery(id+"F2.wireOp",EDGE,"E148"),sQuery(id+"F2.wireOp",EDGE,"E149"),sQuery(id+"F2.wireOp",EDGE,"E150"),sQuery(id+"F2.wireOp",EDGE,"E151"),sQuery(id+"F2.wireOp",EDGE,"E152"),sQuery(id+"F2.wireOp",EDGE,"E153"),sQuery(id+"F2.wireOp",EDGE,"E154"),sQuery(id+"F2.wireOp",EDGE,"E155"),sQuery(id+"F2.wireOp",EDGE,"E156"),sQuery(id+"F2.wireOp",EDGE,"E157"),sQuery(id+"F2.wireOp",EDGE,"E158"),sQuery(id+"F2.wireOp",EDGE,"E159"),sQuery(id+"F2.wireOp",EDGE,"E160"),sQuery(id+"F2.wireOp",EDGE,"E161"),sQuery(id+"F2.wireOp",EDGE,"E162"),sQuery(id+"F2.wireOp",EDGE,"E163"),sQuery(id+"F2.wireOp",EDGE,"E164"),sQuery(id+"F2.wireOp",EDGE,"E165"),sQuery(id+"F2.wireOp",EDGE,"E166"),sQuery(id+"F2.wireOp",EDGE,"E167"),sQuery(id+"F2.wireOp",EDGE,"E168"),sQuery(id+"F2.wireOp",EDGE,"E169"),sQuery(id+"F2.wireOp",EDGE,"E170"),sQuery(id+"F2.wireOp",EDGE,"E171"),sQuery(id+"F2.wireOp",EDGE,"E172"),sQuery(id+"F2.wireOp",EDGE,"E173"),sQuery(id+"F2.wireOp",EDGE,"E174"),sQuery(id+"F2.wireOp",EDGE,"E175"),sQuery(id+"F2.wireOp",EDGE,"E176"),sQuery(id+"F2.wireOp",EDGE,"E177"),sQuery(id+"F2.wireOp",EDGE,"E178"),sQuery(id+"F2.wireOp",EDGE,"E179"),sQuery(id+"F2.wireOp",EDGE,"E180"),sQuery(id+"F2.wireOp",EDGE,"E181"),sQuery(id+"F2.wireOp",EDGE,"E182"),sQuery(id+"F2.wireOp",EDGE,"E183"),sQuery(id+"F2.wireOp",EDGE,"E184"),sQuery(id+"F2.wireOp",EDGE,"E185"),sQuery(id+"F2.wireOp",EDGE,"E186"),sQuery(id+"F2.wireOp",EDGE,"E187"),sQuery(id+"F2.wireOp",EDGE,"E188"),sQuery(id+"F2.wireOp",EDGE,"E189"),sQuery(id+"F2.wireOp",EDGE,"E190"),sQuery(id+"F2.wireOp",EDGE,"E191"),sQuery(id+"F2.wireOp",EDGE,"E192"),sQuery(id+"F2.wireOp",EDGE,"E193"),sQuery(id+"F2.wireOp",EDGE,"E194"),sQuery(id+"F2.wireOp",EDGE,"E195"),sQuery(id+"F2.wireOp",EDGE,"E196"),sQuery(id+"F2.wireOp",EDGE,"E197"),sQuery(id+"F2.wireOp",EDGE,"E198"),sQuery(id+"F2.wireOp",EDGE,"E199"),sQuery(id+"F2.wireOp",EDGE,"E200"),sQuery(id+"F2.wireOp",EDGE,"E201"),sQuery(id+"F2.wireOp",EDGE,"E202"),sQuery(id+"F2.wireOp",EDGE,"E203"),sQuery(id+"F2.wireOp",EDGE,"E204"),sQuery(id+"F2.wireOp",EDGE,"E205"),sQuery(id+"F2.wireOp",EDGE,"E206"),sQuery(id+"F2.wireOp",EDGE,"E207"),sQuery(id+"F2.wireOp",EDGE,"E208"),sQuery(id+"F2.wireOp",EDGE,"E209"),sQuery(id+"F2.wireOp",EDGE,"E210"),sQuery(id+"F2.wireOp",EDGE,"E210"),sQuery(id+"F2.wireOp",EDGE,"E211"),sQuery(id+"F2.wireOp",EDGE,"E212"),sQuery(id+"F2.wireOp",EDGE,"E212"),sQuery(id+"F2.wireOp",EDGE,"E213"),sQuery(id+"F2.wireOp",EDGE,"E214"),sQuery(id+"F2.wireOp",EDGE,"E215"),sQuery(id+"F2.wireOp",EDGE,"E216"),sQuery(id+"F2.wireOp",EDGE,"E217"),sQuery(id+"F2.wireOp",EDGE,"E218"),sQuery(id+"F2.wireOp",EDGE,"E219"),sQuery(id+"F2.wireOp",EDGE,"E220"),sQuery(id+"F2.wireOp",EDGE,"E221"),sQuery(id+"F2.wireOp",EDGE,"E222"),sQuery(id+"F2.wireOp",EDGE,"E223"),sQuery(id+"F2.wireOp",EDGE,"E224"),sQuery(id+"F2.wireOp",EDGE,"E225"),sQuery(id+"F2.wireOp",EDGE,"E226"),sQuery(id+"F2.wireOp",EDGE,"E227"),sQuery(id+"F2.wireOp",EDGE,"E228"),sQuery(id+"F2.wireOp",EDGE,"E229"),sQuery(id+"F2.wireOp",EDGE,"E230"),sQuery(id+"F2.wireOp",EDGE,"E231"),sQuery(id+"F2.wireOp",EDGE,"E232"),sQuery(id+"F2.wireOp",EDGE,"E233"),sQuery(id+"F2.wireOp",EDGE,"E234"),sQuery(id+"F2.wireOp",EDGE,"E235"),sQuery(id+"F2.wireOp",EDGE,"E236"),sQuery(id+"F2.wireOp",EDGE,"E237"),sQuery(id+"F2.wireOp",EDGE,"E238"),sQuery(id+"F2.wireOp",EDGE,"E239"),sQuery(id+"F2.wireOp",EDGE,"E240"),sQuery(id+"F2.wireOp",EDGE,"E241"),sQuery(id+"F2.wireOp",EDGE,"E242"),sQuery(id+"F2.wireOp",EDGE,"E243"),sQuery(id+"F2.wireOp",EDGE,"E244"),sQuery(id+"F2.wireOp",EDGE,"E245"),sQuery(id+"F2.wireOp",EDGE,"E246"),sQuery(id+"F2.wireOp",EDGE,"E247"),sQuery(id+"F2.wireOp",EDGE,"E248"),sQuery(id+"F2.wireOp",EDGE,"E249"),sQuery(id+"F2.wireOp",EDGE,"E250"),sQuery(id+"F2.wireOp",EDGE,"E251"),sQuery(id+"F2.wireOp",EDGE,"E252"),sQuery(id+"F2.wireOp",EDGE,"E253"),sQuery(id+"F2.wireOp",EDGE,"E254"),sQuery(id+"F2.wireOp",EDGE,"E255"),sQuery(id+"F2.wireOp",EDGE,"E256"),sQuery(id+"F2.wireOp",EDGE,"E257"),sQuery(id+"F2.wireOp",EDGE,"E258"),sQuery(id+"F2.wireOp",EDGE,"E259"),sQuery(id+"F2.wireOp",EDGE,"E260"),sQuery(id+"F2.wireOp",EDGE,"E261"),sQuery(id+"F2.wireOp",EDGE,"E262"),sQuery(id+"F2.wireOp",EDGE,"E263"),sQuery(id+"F2.wireOp",EDGE,"E264"),sQuery(id+"F2.wireOp",EDGE,"E265"),sQuery(id+"F2.wireOp",EDGE,"E266"),sQuery(id+"F2.wireOp",EDGE,"E267"),sQuery(id+"F2.wireOp",EDGE,"E268"),sQuery(id+"F2.wireOp",EDGE,"E269"),sQuery(id+"F2.wireOp",EDGE,"E270"),sQuery(id+"F2.wireOp",EDGE,"E271"),sQuery(id+"F2.wireOp",EDGE,"E272"),sQuery(id+"F2.wireOp",EDGE,"E273"),sQuery(id+"F2.wireOp",EDGE,"E274"),sQuery(id+"F2.wireOp",EDGE,"E275"),sQuery(id+"F2.wireOp",EDGE,"E276"),sQuery(id+"F2.wireOp",EDGE,"E277"),sQuery(id+"F2.wireOp",EDGE,"E278"),sQuery(id+"F2.wireOp",EDGE,"E279"),sQuery(id+"F2.wireOp",EDGE,"E280"),sQuery(id+"F2.wireOp",EDGE,"E281"),sQuery(id+"F2.wireOp",EDGE,"E282"),sQuery(id+"F2.wireOp",EDGE,"E283"),sQuery(id+"F2.wireOp",EDGE,"E284"),sQuery(id+"F2.wireOp",EDGE,"E285"),sQuery(id+"F2.wireOp",EDGE,"E286"),sQuery(id+"F2.wireOp",EDGE,"E287"),sQuery(id+"F2.wireOp",EDGE,"E288"),sQuery(id+"F2.wireOp",EDGE,"E289"),sQuery(id+"F2.wireOp",EDGE,"E290"),sQuery(id+"F2.wireOp",EDGE,"E291"),sQuery(id+"F2.wireOp",EDGE,"E292"),sQuery(id+"F2.wireOp",EDGE,"E293"),sQuery(id+"F2.wireOp",EDGE,"E294"),sQuery(id+"F2.wireOp",EDGE,"E295"),sQuery(id+"F2.wireOp",EDGE,"E296"),sQuery(id+"F2.wireOp",EDGE,"E297"),sQuery(id+"F2.wireOp",EDGE,"E298"),sQuery(id+"F2.wireOp",EDGE,"E299"),sQuery(id+"F2.wireOp",EDGE,"E300"),sQuery(id+"F2.wireOp",EDGE,"E301"),sQuery(id+"F2.wireOp",EDGE,"E302"),sQuery(id+"F2.wireOp",EDGE,"E303"),sQuery(id+"F2.wireOp",EDGE,"E304"),sQuery(id+"F2.wireOp",EDGE,"E305"),sQuery(id+"F2.wireOp",EDGE,"E306"),sQuery(id+"F2.wireOp",EDGE,"E307"),sQuery(id+"F2.wireOp",EDGE,"E308"),sQuery(id+"F2.wireOp",EDGE,"E309"),sQuery(id+"F2.wireOp",EDGE,"E310"),sQuery(id+"F2.wireOp",EDGE,"E311"),sQuery(id+"F2.wireOp",EDGE,"E312"),sQuery(id+"F2.wireOp",EDGE,"E313"),sQuery(id+"F2.wireOp",EDGE,"E314"),sQuery(id+"F2.wireOp",EDGE,"E315"),sQuery(id+"F2.wireOp",EDGE,"E316"),sQuery(id+"F2.wireOp",EDGE,"E317"),sQuery(id+"F2.wireOp",EDGE,"E318"),sQuery(id+"F2.wireOp",EDGE,"E319"),sQuery(id+"F2.wireOp",EDGE,"E320"),sQuery(id+"F2.wireOp",EDGE,"E321"),sQuery(id+"F2.wireOp",EDGE,"E322"),sQuery(id+"F2.wireOp",EDGE,"E323"),sQuery(id+"F2.wireOp",EDGE,"E324"),sQuery(id+"F2.wireOp",EDGE,"E325"),sQuery(id+"F2.wireOp",EDGE,"E326"),sQuery(id+"F2.wireOp",EDGE,"E327"),sQuery(id+"F2.wireOp",EDGE,"E328"),sQuery(id+"F2.wireOp",EDGE,"E329"),sQuery(id+"F2.wireOp",EDGE,"E330"),sQuery(id+"F2.wireOp",EDGE,"E331"),sQuery(id+"F2.wireOp",EDGE,"E332"),sQuery(id+"F2.wireOp",EDGE,"E333"),sQuery(id+"F2.wireOp",EDGE,"E334"),sQuery(id+"F2.wireOp",EDGE,"E335"),sQuery(id+"F2.wireOp",EDGE,"E336"),sQuery(id+"F2.wireOp",EDGE,"E337"),sQuery(id+"F2.wireOp",EDGE,"E338"),sQuery(id+"F2.wireOp",EDGE,"E339"),sQuery(id+"F2.wireOp",EDGE,"E340"),sQuery(id+"F2.wireOp",EDGE,"E341"),sQuery(id+"F2.wireOp",EDGE,"E342"),sQuery(id+"F2.wireOp",EDGE,"E343"),sQuery(id+"F2.wireOp",EDGE,"E344"),sQuery(id+"F2.wireOp",EDGE,"E345"),sQuery(id+"F2.wireOp",EDGE,"E346"),sQuery(id+"F2.wireOp",EDGE,"E347"),sQuery(id+"F2.wireOp",EDGE,"E348"),sQuery(id+"F2.wireOp",EDGE,"E349"),sQuery(id+"F2.wireOp",EDGE,"E350"),sQuery(id+"F2.wireOp",EDGE,"E351"),sQuery(id+"F2.wireOp",EDGE,"E352"),sQuery(id+"F2.wireOp",EDGE,"E353"),sQuery(id+"F2.wireOp",EDGE,"E354"),sQuery(id+"F2.wireOp",EDGE,"E355"),sQuery(id+"F2.wireOp",EDGE,"E356"),sQuery(id+"F2.wireOp",EDGE,"E357"),sQuery(id+"F2.wireOp",EDGE,"E358"),sQuery(id+"F2.wireOp",EDGE,"E359"),sQuery(id+"F2.wireOp",EDGE,"E360"),sQuery(id+"F2.wireOp",EDGE,"E361"),sQuery(id+"F2.wireOp",EDGE,"E362"),sQuery(id+"F2.wireOp",EDGE,"E363"),sQuery(id+"F2.wireOp",EDGE,"E364"),sQuery(id+"F2.wireOp",EDGE,"E365"),sQuery(id+"F2.wireOp",EDGE,"E366"),sQuery(id+"F2.wireOp",EDGE,"E367"),sQuery(id+"F2.wireOp",EDGE,"E368"),sQuery(id+"F2.wireOp",EDGE,"E369"),sQuery(id+"F2.wireOp",EDGE,"E370"),sQuery(id+"F2.wireOp",EDGE,"E371"),sQuery(id+"F2.wireOp",EDGE,"E372"),sQuery(id+"F2.wireOp",EDGE,"E373"),sQuery(id+"F2.wireOp",EDGE,"E374"),sQuery(id+"F2.wireOp",EDGE,"E375"),sQuery(id+"F2.wireOp",EDGE,"E376"),sQuery(id+"F2.wireOp",EDGE,"E377"),sQuery(id+"F2.wireOp",EDGE,"E378"),sQuery(id+"F2.wireOp",EDGE,"E379"),sQuery(id+"F2.wireOp",EDGE,"E380"),sQuery(id+"F2.wireOp",EDGE,"E381"),sQuery(id+"F2.wireOp",EDGE,"E382"),sQuery(id+"F2.wireOp",EDGE,"E383"),sQuery(id+"F2.wireOp",EDGE,"E384"),sQuery(id+"F2.wireOp",EDGE,"E385"),sQuery(id+"F2.wireOp",EDGE,"E386"),sQuery(id+"F2.wireOp",EDGE,"E387"),sQuery(id+"F2.wireOp",EDGE,"E388"),sQuery(id+"F2.wireOp",EDGE,"E389"),sQuery(id+"F2.wireOp",EDGE,"E390"),sQuery(id+"F2.wireOp",EDGE,"E391"),sQuery(id+"F2.wireOp",EDGE,"E392"),sQuery(id+"F2.wireOp",EDGE,"E393"),sQuery(id+"F2.wireOp",EDGE,"E394"),sQuery(id+"F2.wireOp",EDGE,"E395"),sQuery(id+"F2.wireOp",EDGE,"E396"),sQuery(id+"F2.wireOp",EDGE,"E397"),sQuery(id+"F2.wireOp",EDGE,"E398"),sQuery(id+"F2.wireOp",EDGE,"E399"),sQuery(id+"F2.wireOp",EDGE,"E400"),sQuery(id+"F2.wireOp",EDGE,"E401"),sQuery(id+"F2.wireOp",EDGE,"E402"),sQuery(id+"F2.wireOp",EDGE,"E403"),sQuery(id+"F2.wireOp",EDGE,"E404"),sQuery(id+"F2.wireOp",EDGE,"E500")])]});
            booleanBodies(context, id + "F9", {"operationType" : BooleanOperationType.UNION, "tools" : qUnion([Q0, Q1, Q2, Q3, Q4, Q5, Q6])});
        }
        {
            var Q0;
            Q0=makeQuery(id+"F1.opExtrude","CAP_FACE",FACE,{"disambiguationData":[OSD([sQuery(id+"F0.wireOp",EDGE,"E0.top"),sQuery(id+"F0.wireOp",EDGE,"E0.left"),sQuery(id+"F0.wireOp",EDGE,"E0.right"),sQuery(id+"F0.wireOp",EDGE,"E0.bottom"),sQuery(id+"F0.wireOp",EDGE,"E1.left"),sQuery(id+"F0.wireOp",EDGE,"E1.right"),sQuery(id+"F0.wireOp",EDGE,"E3"),sQuery(id+"F0.wireOp",EDGE,"E5.MirrorCS")])],"isStart":false});
            var sketch = newSketch(context, id + "F10", { "sketchPlane" : qUnion([Q0])});
            skText(sketch, "E592", { "text": "Ludvig 7 år", "fontName": "OpenSans-Regular.ttf"});
            const initialGuessF10  = {"E592": [-0.045, 0.097, 1, 0, 0.013]};
            skSetInitialGuess(sketch, initialGuessF10);
            skSolve(sketch);
        }
        {
            var Q0;
            Q0 = qSketchRegion(id + "F10", true);
            extrude(context, id + "F11", {"entities" : qUnion([Q0]), "operationType" : NewBodyOperationType.ADD, "depth" : 1 * mm});
        }
        {
            var Q0;
            {var subQ0=sQuery(id+"F0.wireOp",EDGE,"E1.right");var subQ1=sQuery(id+"F0.wireOp",EDGE,"E0.bottom");var subQ2=sQuery(id+"F0.wireOp",EDGE,"E3");var subQ3=sQuery(id+"F0.wireOp",EDGE,"E1.left");var subQ4=sQuery(id+"F0.wireOp",EDGE,"E5.MirrorCS");var subQ5=sQuery(id+"F0.wireOp",EDGE,"E0.right");var subQ6=sQuery(id+"F0.wireOp",EDGE,"E0.left");var subQ7=sQuery(id+"F0.wireOp",EDGE,"E0.top");Q0=makeQuery(id+"F11.boolean.opBoolean","SPLIT",FACE,{"disambiguationData":[TD([makeQuery(id+"F1.opExtrude","SWEPT_FACE",FACE,{"disambiguationData":[OSD([subQ7])]})])],"derivedFrom":makeQuery(id+"F9.opBoolean","MERGE",FACE,{"derivedFrom":[makeQuery(id+"F1.opExtrude","CAP_FACE",FACE,{"disambiguationData":[OSD([subQ7,subQ6,subQ5,subQ1,subQ3,subQ0,subQ2,subQ4])],"isStart":false}),makeQuery(id+"F7.opExtrude","CAP_FACE",FACE,{"disambiguationData":[OSD([subQ1,subQ2,sQuery(id+"F0.wireOp",EDGE,"E4")])],"isStart":false})]})});}
            var sketch = newSketch(context, id + "F12", { "sketchPlane" : qUnion([Q0])});
            skLineSegment(sketch, "E593", {"start": v(-50, 0) * mm, "end": v(0, 68.7) * mm});
            skLineSegment(sketch, "E594", {"start": v(0, 68.7) * mm, "end": v(50, 0) * mm});
            skLineSegment(sketch, "E595", {"start": v(50, 0) * mm, "end": v(-50, 0) * mm});
            skLineSegment(sketch, "E596", {"start": v(-33.29, 0) * mm, "end": v(-33.29, 22.96) * mm});
            skLineSegment(sketch, "E597", {"start": v(33.29, 0) * mm, "end": v(33.29, 22.96) * mm});
            skSolve(sketch);
        }
        {
            var Q0;
            {var subQ0=sQuery(id+"F12.wireOp",EDGE,"E593");var subQ1=sQuery(id+"F0.wireOp",EDGE,"E3");var subQ2=makeQuery(id+"F8.opShell","OFFSET_EDGE",EDGE,{"disambiguationData":[OSD([subQ1]),TDD([makeQuery(id+"F7.opExtrude","CAP_EDGE",EDGE,{"disambiguationData":[OSD([subQ1]),TDD([makeQuery(id+"F6.opRevolve","CAP_EDGE",EDGE,{"disambiguationData":[OSD([subQ1])],"isStart":true})])],"isStart":false})])]});var subQ4=makeQuery(id+"F12.imprint","INTERSECT",VERTEX,{"derivedFrom":[subQ2,subQ0]});Q0=makeQuery(id+"F12.imprint","IMPRINT",FACE,{"disambiguationData":[TD([[makeQuery(id+"F12.imprint","IMPRINT",EDGE,{"disambiguationData":[TD([[subQ4,-1.0]])],"derivedFrom":subQ0}),1.0]])]});}
            var Q1;
            {var subQ0=sQuery(id+"F12.wireOp",EDGE,"E594");var subQ1=sQuery(id+"F0.wireOp",EDGE,"E3");var subQ2=makeQuery(id+"F8.opShell","OFFSET_EDGE",EDGE,{"disambiguationData":[OSD([subQ1]),TDD([makeQuery(id+"F7.opExtrude","CAP_EDGE",EDGE,{"disambiguationData":[OSD([subQ1]),TDD([makeQuery(id+"F6.opRevolve","CAP_EDGE",EDGE,{"disambiguationData":[OSD([subQ1])],"isStart":false})])],"isStart":false})])]});var subQ4=makeQuery(id+"F12.imprint","INTERSECT",VERTEX,{"derivedFrom":[subQ2,subQ0]});Q1=makeQuery(id+"F12.imprint","IMPRINT",FACE,{"disambiguationData":[TD([[makeQuery(id+"F12.imprint","IMPRINT",EDGE,{"disambiguationData":[TD([[subQ4,1.0]])],"derivedFrom":subQ0}),1.0]])]});}
            var Q2;
            {var subQ0=sQuery(id+"F12.wireOp",EDGE,"E596");Q2=makeQuery(id+"F12.imprint","IMPRINT",FACE,{"disambiguationData":[TD([[makeQuery(id+"F12.imprint","IMPRINT",EDGE,{"derivedFrom":subQ0}),1.0]])]});}
            var Q3;
            {var subQ0=sQuery(id+"F12.wireOp",EDGE,"E597");Q3=makeQuery(id+"F12.imprint","IMPRINT",FACE,{"disambiguationData":[TD([[makeQuery(id+"F12.imprint","IMPRINT",EDGE,{"derivedFrom":subQ0}),-1.0]])]});}
            var Q4;
            Q4=makeQuery(id+"F6.opRevolve","SWEPT_FACE",FACE,{"disambiguationData":[OSD([sQuery(id+"F0.wireOp",EDGE,"E3")])]});
            extrude(context, id + "F13", {"entities" : qUnion([Q0, Q1, Q2, Q3]), "operationType" : NewBodyOperationType.ADD, "endBound" : BoundingType.UP_TO_SURFACE, "oppositeDirection" : true, "endBoundEntityFace" : qUnion([Q4]), "depth" : 40 * mm});
        }
    });
